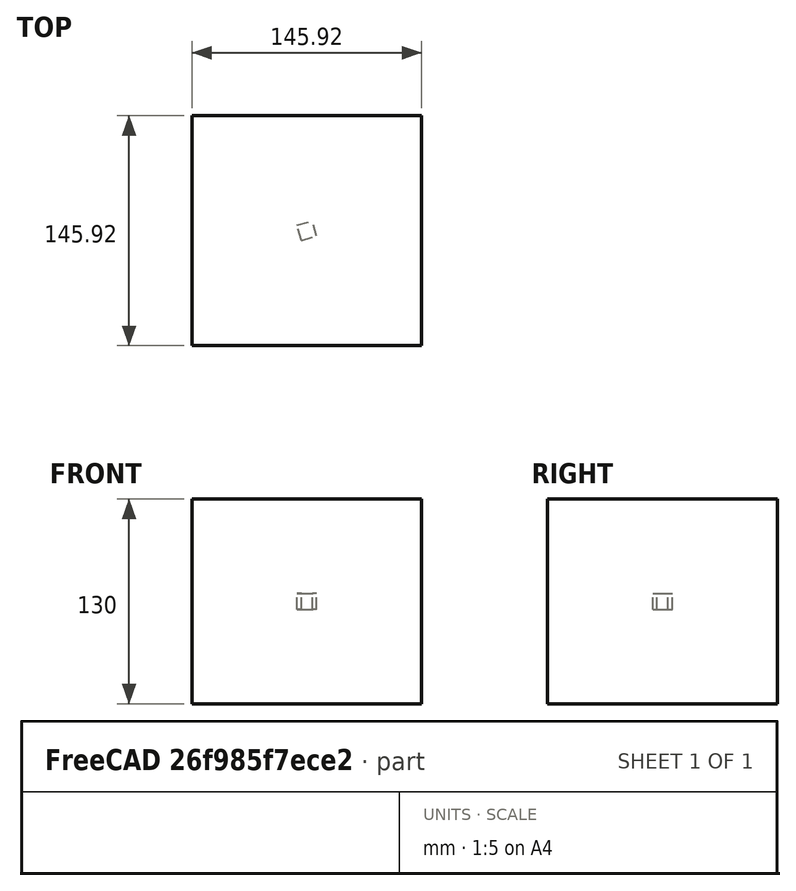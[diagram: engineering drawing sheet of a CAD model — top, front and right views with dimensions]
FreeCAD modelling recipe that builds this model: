
FCSTD DOCUMENT  (FreeCAD 0.20RUnknown)
Label: array-rotation-test-c
License: All rights reserved
objects: App::DocumentObjectGroupPython×1251, Part::FeaturePython×3, App::Part×2
note: 2 computed .brp shape members not serialized (recipe doc carries the construction recipe); baked Part::Feature solids carry a one-line shape summary decoded from their .brp

FEATURE [App::DocumentObjectGroupPython] HALFPI  # scripted group (container) (typed FeaturePython)
  name = HALFPI
  value = pi/2.
FEATURE [App::DocumentObjectGroupPython] PI  # scripted group (container) (typed FeaturePython)
  name = PI
  value = 1.*pi
FEATURE [App::DocumentObjectGroupPython] TWOPI  # scripted group (container) (typed FeaturePython)
  name = TWOPI
  value = 2.*pi
FEATURE [App::DocumentObjectGroupPython] Constants  # scripted group (container) (typed FeaturePython)
  Group = -> [HALFPI,PI,TWOPI]
FEATURE [App::DocumentObjectGroupPython] Variables  # scripted group (container) (typed FeaturePython)
FEATURE [App::DocumentObjectGroupPython] Quantities  # scripted group (container) (typed FeaturePython)
FEATURE [App::DocumentObjectGroupPython] Isotopes  # scripted group (container) (typed FeaturePython)
FEATURE [App::DocumentObjectGroupPython] Elements  # scripted group (container) (typed FeaturePython)
FEATURE [App::DocumentObjectGroupPython] Matrix  # scripted group (container) (typed FeaturePython)
FEATURE [App::DocumentObjectGroupPython] Surfaces  # scripted group (container) (typed FeaturePython)
FEATURE [App::DocumentObjectGroupPython] Opticals  # scripted group (container) (typed FeaturePython)
  Group = -> [Matrix,Surfaces]
FEATURE [App::DocumentObjectGroupPython] G4Isotopes  # scripted group (container) (typed FeaturePython)
FEATURE [App::DocumentObjectGroupPython] H_element  # scripted group (container) (typed FeaturePython)
  Z = 1
  atom_value = 1.008
  formula = H
  name = H_element
FEATURE [App::DocumentObjectGroupPython] He_element  # scripted group (container) (typed FeaturePython)
  Z = 2
  atom_value = 4.0026
  formula = He
  name = He_element
FEATURE [App::DocumentObjectGroupPython] Li_element  # scripted group (container) (typed FeaturePython)
  Z = 3
  atom_value = 6.94
  formula = Li
  name = Li_element
FEATURE [App::DocumentObjectGroupPython] Be_element  # scripted group (container) (typed FeaturePython)
  Z = 4
  atom_value = 9.01218
  formula = Be
  name = Be_element
FEATURE [App::DocumentObjectGroupPython] B_element  # scripted group (container) (typed FeaturePython)
  Z = 5
  atom_value = 10.81
  formula = B
  name = B_element
FEATURE [App::DocumentObjectGroupPython] C_element  # scripted group (container) (typed FeaturePython)
  Z = 6
  atom_value = 12.011
  formula = C
  name = C_element
FEATURE [App::DocumentObjectGroupPython] N_element  # scripted group (container) (typed FeaturePython)
  Z = 7
  atom_value = 14.007
  formula = N
  name = N_element
FEATURE [App::DocumentObjectGroupPython] O_element  # scripted group (container) (typed FeaturePython)
  Z = 8
  atom_value = 15.999
  formula = O
  name = O_element
FEATURE [App::DocumentObjectGroupPython] F_element  # scripted group (container) (typed FeaturePython)
  Z = 9
  atom_value = 18.9984
  formula = F
  name = F_element
FEATURE [App::DocumentObjectGroupPython] Ne_element  # scripted group (container) (typed FeaturePython)
  Z = 10
  atom_value = 20.1797
  formula = Ne
  name = Ne_element
FEATURE [App::DocumentObjectGroupPython] Na_element  # scripted group (container) (typed FeaturePython)
  Z = 11
  atom_value = 22.9898
  formula = Na
  name = Na_element
FEATURE [App::DocumentObjectGroupPython] Mg_element  # scripted group (container) (typed FeaturePython)
  Z = 12
  atom_value = 24.305
  formula = Mg
  name = Mg_element
FEATURE [App::DocumentObjectGroupPython] Al_element  # scripted group (container) (typed FeaturePython)
  Z = 13
  atom_value = 26.9815
  formula = Al
  name = Al_element
FEATURE [App::DocumentObjectGroupPython] Si_element  # scripted group (container) (typed FeaturePython)
  Z = 14
  atom_value = 28.085
  formula = Si
  name = Si_element
FEATURE [App::DocumentObjectGroupPython] P_element  # scripted group (container) (typed FeaturePython)
  Z = 15
  atom_value = 30.9738
  formula = P
  name = P_element
FEATURE [App::DocumentObjectGroupPython] S_element  # scripted group (container) (typed FeaturePython)
  Z = 16
  atom_value = 32.06
  formula = S
  name = S_element
FEATURE [App::DocumentObjectGroupPython] Cl_element  # scripted group (container) (typed FeaturePython)
  Z = 17
  atom_value = 35.45
  formula = Cl
  name = Cl_element
FEATURE [App::DocumentObjectGroupPython] Ar_element  # scripted group (container) (typed FeaturePython)
  Z = 18
  atom_value = 39.95
  formula = Ar
  name = Ar_element
FEATURE [App::DocumentObjectGroupPython] K_element  # scripted group (container) (typed FeaturePython)
  Z = 19
  atom_value = 39.0983
  formula = K
  name = K_element
FEATURE [App::DocumentObjectGroupPython] Ca_element  # scripted group (container) (typed FeaturePython)
  Z = 20
  atom_value = 40.078
  formula = Ca
  name = Ca_element
FEATURE [App::DocumentObjectGroupPython] Sc_element  # scripted group (container) (typed FeaturePython)
  Z = 21
  atom_value = 44.9559
  formula = Sc
  name = Sc_element
FEATURE [App::DocumentObjectGroupPython] Ti_element  # scripted group (container) (typed FeaturePython)
  Z = 22
  atom_value = 47.867
  formula = Ti
  name = Ti_element
FEATURE [App::DocumentObjectGroupPython] V_element  # scripted group (container) (typed FeaturePython)
  Z = 23
  atom_value = 50.9415
  formula = V
  name = V_element
FEATURE [App::DocumentObjectGroupPython] Cr_element  # scripted group (container) (typed FeaturePython)
  Z = 24
  atom_value = 51.9961
  formula = Cr
  name = Cr_element
FEATURE [App::DocumentObjectGroupPython] Mn_element  # scripted group (container) (typed FeaturePython)
  Z = 25
  atom_value = 54.938
  formula = Mn
  name = Mn_element
FEATURE [App::DocumentObjectGroupPython] Fe_element  # scripted group (container) (typed FeaturePython)
  Z = 26
  atom_value = 55.845
  formula = Fe
  name = Fe_element
FEATURE [App::DocumentObjectGroupPython] Co_element  # scripted group (container) (typed FeaturePython)
  Z = 27
  atom_value = 58.9332
  formula = Co
  name = Co_element
FEATURE [App::DocumentObjectGroupPython] Ni_element  # scripted group (container) (typed FeaturePython)
  Z = 28
  atom_value = 58.6934
  formula = Ni
  name = Ni_element
FEATURE [App::DocumentObjectGroupPython] Cu_element  # scripted group (container) (typed FeaturePython)
  Z = 29
  atom_value = 63.546
  formula = Cu
  name = Cu_element
FEATURE [App::DocumentObjectGroupPython] Zn_element  # scripted group (container) (typed FeaturePython)
  Z = 30
  atom_value = 65.38
  formula = Zn
  name = Zn_element
FEATURE [App::DocumentObjectGroupPython] Ga_element  # scripted group (container) (typed FeaturePython)
  Z = 31
  atom_value = 69.723
  formula = Ga
  name = Ga_element
FEATURE [App::DocumentObjectGroupPython] Ge_element  # scripted group (container) (typed FeaturePython)
  Z = 32
  atom_value = 72.63
  formula = Ge
  name = Ge_element
FEATURE [App::DocumentObjectGroupPython] As_element  # scripted group (container) (typed FeaturePython)
  Z = 33
  atom_value = 74.9216
  formula = As
  name = As_element
FEATURE [App::DocumentObjectGroupPython] Se_element  # scripted group (container) (typed FeaturePython)
  Z = 34
  atom_value = 78.971
  formula = Se
  name = Se_element
FEATURE [App::DocumentObjectGroupPython] Br_element  # scripted group (container) (typed FeaturePython)
  Z = 35
  atom_value = 79.904
  formula = Br
  name = Br_element
FEATURE [App::DocumentObjectGroupPython] Kr_element  # scripted group (container) (typed FeaturePython)
  Z = 36
  atom_value = 83.798
  formula = Kr
  name = Kr_element
FEATURE [App::DocumentObjectGroupPython] Rb_element  # scripted group (container) (typed FeaturePython)
  Z = 37
  atom_value = 85.4678
  formula = Rb
  name = Rb_element
FEATURE [App::DocumentObjectGroupPython] Sr_element  # scripted group (container) (typed FeaturePython)
  Z = 38
  atom_value = 87.62
  formula = Sr
  name = Sr_element
FEATURE [App::DocumentObjectGroupPython] Y_element  # scripted group (container) (typed FeaturePython)
  Z = 39
  atom_value = 88.9058
  formula = Y
  name = Y_element
FEATURE [App::DocumentObjectGroupPython] Zr_element  # scripted group (container) (typed FeaturePython)
  Z = 40
  atom_value = 91.224
  formula = Zr
  name = Zr_element
FEATURE [App::DocumentObjectGroupPython] Nb_element  # scripted group (container) (typed FeaturePython)
  Z = 41
  atom_value = 92.9064
  formula = Nb
  name = Nb_element
FEATURE [App::DocumentObjectGroupPython] Mo_element  # scripted group (container) (typed FeaturePython)
  Z = 42
  atom_value = 95.95
  formula = Mo
  name = Mo_element
FEATURE [App::DocumentObjectGroupPython] Tc_element  # scripted group (container) (typed FeaturePython)
  Z = 43
  atom_value = 97
  formula = Tc
  name = Tc_element
FEATURE [App::DocumentObjectGroupPython] Ru_element  # scripted group (container) (typed FeaturePython)
  Z = 44
  atom_value = 101.07
  formula = Ru
  name = Ru_element
FEATURE [App::DocumentObjectGroupPython] Rh_element  # scripted group (container) (typed FeaturePython)
  Z = 45
  atom_value = 102.905
  formula = Rh
  name = Rh_element
FEATURE [App::DocumentObjectGroupPython] Pd_element  # scripted group (container) (typed FeaturePython)
  Z = 46
  atom_value = 106.42
  formula = Pd
  name = Pd_element
FEATURE [App::DocumentObjectGroupPython] Ag_element  # scripted group (container) (typed FeaturePython)
  Z = 47
  atom_value = 107.868
  formula = Ag
  name = Ag_element
FEATURE [App::DocumentObjectGroupPython] Cd_element  # scripted group (container) (typed FeaturePython)
  Z = 48
  atom_value = 112.414
  formula = Cd
  name = Cd_element
FEATURE [App::DocumentObjectGroupPython] In_element  # scripted group (container) (typed FeaturePython)
  Z = 49
  atom_value = 114.818
  formula = In
  name = In_element
FEATURE [App::DocumentObjectGroupPython] Sn_element  # scripted group (container) (typed FeaturePython)
  Z = 50
  atom_value = 118.71
  formula = Sn
  name = Sn_element
FEATURE [App::DocumentObjectGroupPython] Sb_element  # scripted group (container) (typed FeaturePython)
  Z = 51
  atom_value = 121.76
  formula = Sb
  name = Sb_element
FEATURE [App::DocumentObjectGroupPython] Te_element  # scripted group (container) (typed FeaturePython)
  Z = 52
  atom_value = 127.6
  formula = Te
  name = Te_element
FEATURE [App::DocumentObjectGroupPython] I_element  # scripted group (container) (typed FeaturePython)
  Z = 53
  atom_value = 126.904
  formula = I
  name = I_element
FEATURE [App::DocumentObjectGroupPython] Xe_element  # scripted group (container) (typed FeaturePython)
  Z = 54
  atom_value = 131.293
  formula = Xe
  name = Xe_element
FEATURE [App::DocumentObjectGroupPython] Cs_element  # scripted group (container) (typed FeaturePython)
  Z = 55
  atom_value = 132.905
  formula = Cs
  name = Cs_element
FEATURE [App::DocumentObjectGroupPython] Ba_element  # scripted group (container) (typed FeaturePython)
  Z = 56
  atom_value = 137.327
  formula = Ba
  name = Ba_element
FEATURE [App::DocumentObjectGroupPython] La_element  # scripted group (container) (typed FeaturePython)
  Z = 57
  atom_value = 138.905
  formula = La
  name = La_element
FEATURE [App::DocumentObjectGroupPython] Ce_element  # scripted group (container) (typed FeaturePython)
  Z = 58
  atom_value = 140.116
  formula = Ce
  name = Ce_element
FEATURE [App::DocumentObjectGroupPython] Pr_element  # scripted group (container) (typed FeaturePython)
  Z = 59
  atom_value = 140.908
  formula = Pr
  name = Pr_element
FEATURE [App::DocumentObjectGroupPython] Nd_element  # scripted group (container) (typed FeaturePython)
  Z = 60
  atom_value = 144.242
  formula = Nd
  name = Nd_element
FEATURE [App::DocumentObjectGroupPython] Pm_element  # scripted group (container) (typed FeaturePython)
  Z = 61
  atom_value = 145
  formula = Pm
  name = Pm_element
FEATURE [App::DocumentObjectGroupPython] Sm_element  # scripted group (container) (typed FeaturePython)
  Z = 62
  atom_value = 150.36
  formula = Sm
  name = Sm_element
FEATURE [App::DocumentObjectGroupPython] Eu_element  # scripted group (container) (typed FeaturePython)
  Z = 63
  atom_value = 151.964
  formula = Eu
  name = Eu_element
FEATURE [App::DocumentObjectGroupPython] Gd_element  # scripted group (container) (typed FeaturePython)
  Z = 64
  atom_value = 157.25
  formula = Gd
  name = Gd_element
FEATURE [App::DocumentObjectGroupPython] Tb_element  # scripted group (container) (typed FeaturePython)
  Z = 65
  atom_value = 158.925
  formula = Tb
  name = Tb_element
FEATURE [App::DocumentObjectGroupPython] Dy_element  # scripted group (container) (typed FeaturePython)
  Z = 66
  atom_value = 162.5
  formula = Dy
  name = Dy_element
FEATURE [App::DocumentObjectGroupPython] Ho_element  # scripted group (container) (typed FeaturePython)
  Z = 67
  atom_value = 164.93
  formula = Ho
  name = Ho_element
FEATURE [App::DocumentObjectGroupPython] Er_element  # scripted group (container) (typed FeaturePython)
  Z = 68
  atom_value = 167.259
  formula = Er
  name = Er_element
FEATURE [App::DocumentObjectGroupPython] Tm_element  # scripted group (container) (typed FeaturePython)
  Z = 69
  atom_value = 168.934
  formula = Tm
  name = Tm_element
FEATURE [App::DocumentObjectGroupPython] Yb_element  # scripted group (container) (typed FeaturePython)
  Z = 70
  atom_value = 173.045
  formula = Yb
  name = Yb_element
FEATURE [App::DocumentObjectGroupPython] Lu_element  # scripted group (container) (typed FeaturePython)
  Z = 71
  atom_value = 174.967
  formula = Lu
  name = Lu_element
FEATURE [App::DocumentObjectGroupPython] Hf_element  # scripted group (container) (typed FeaturePython)
  Z = 72
  atom_value = 178.49
  formula = Hf
  name = Hf_element
FEATURE [App::DocumentObjectGroupPython] Ta_element  # scripted group (container) (typed FeaturePython)
  Z = 73
  atom_value = 180.948
  formula = Ta
  name = Ta_element
FEATURE [App::DocumentObjectGroupPython] W_element  # scripted group (container) (typed FeaturePython)
  Z = 74
  atom_value = 183.84
  formula = W
  name = W_element
FEATURE [App::DocumentObjectGroupPython] Re_element  # scripted group (container) (typed FeaturePython)
  Z = 75
  atom_value = 186.207
  formula = Re
  name = Re_element
FEATURE [App::DocumentObjectGroupPython] Os_element  # scripted group (container) (typed FeaturePython)
  Z = 76
  atom_value = 190.23
  formula = Os
  name = Os_element
FEATURE [App::DocumentObjectGroupPython] Ir_element  # scripted group (container) (typed FeaturePython)
  Z = 77
  atom_value = 192.217
  formula = Ir
  name = Ir_element
FEATURE [App::DocumentObjectGroupPython] Pt_element  # scripted group (container) (typed FeaturePython)
  Z = 78
  atom_value = 195.084
  formula = Pt
  name = Pt_element
FEATURE [App::DocumentObjectGroupPython] Au_element  # scripted group (container) (typed FeaturePython)
  Z = 79
  atom_value = 196.967
  formula = Au
  name = Au_element
FEATURE [App::DocumentObjectGroupPython] Hg_element  # scripted group (container) (typed FeaturePython)
  Z = 80
  atom_value = 200.592
  formula = Hg
  name = Hg_element
FEATURE [App::DocumentObjectGroupPython] Tl_element  # scripted group (container) (typed FeaturePython)
  Z = 81
  atom_value = 204.38
  formula = Tl
  name = Tl_element
FEATURE [App::DocumentObjectGroupPython] Pb_element  # scripted group (container) (typed FeaturePython)
  Z = 82
  atom_value = 207.2
  formula = Pb
  name = Pb_element
FEATURE [App::DocumentObjectGroupPython] Bi_element  # scripted group (container) (typed FeaturePython)
  Z = 83
  atom_value = 208.98
  formula = Bi
  name = Bi_element
FEATURE [App::DocumentObjectGroupPython] Po_element  # scripted group (container) (typed FeaturePython)
  Z = 84
  atom_value = 209
  formula = Po
  name = Po_element
FEATURE [App::DocumentObjectGroupPython] At_element  # scripted group (container) (typed FeaturePython)
  Z = 85
  atom_value = 210
  formula = At
  name = At_element
FEATURE [App::DocumentObjectGroupPython] Rn_element  # scripted group (container) (typed FeaturePython)
  Z = 86
  atom_value = 222
  formula = Rn
  name = Rn_element
FEATURE [App::DocumentObjectGroupPython] Fr_element  # scripted group (container) (typed FeaturePython)
  Z = 87
  atom_value = 223
  formula = Fr
  name = Fr_element
FEATURE [App::DocumentObjectGroupPython] Ra_element  # scripted group (container) (typed FeaturePython)
  Z = 88
  atom_value = 226
  formula = Ra
  name = Ra_element
FEATURE [App::DocumentObjectGroupPython] Ac_element  # scripted group (container) (typed FeaturePython)
  Z = 89
  atom_value = 227
  formula = Ac
  name = Ac_element
FEATURE [App::DocumentObjectGroupPython] Th_element  # scripted group (container) (typed FeaturePython)
  Z = 90
  atom_value = 232.038
  formula = Th
  name = Th_element
FEATURE [App::DocumentObjectGroupPython] Pa_element  # scripted group (container) (typed FeaturePython)
  Z = 91
  atom_value = 231.036
  formula = Pa
  name = Pa_element
FEATURE [App::DocumentObjectGroupPython] U_element  # scripted group (container) (typed FeaturePython)
  Z = 92
  atom_value = 238.029
  formula = U
  name = U_element
FEATURE [App::DocumentObjectGroupPython] Np_element  # scripted group (container) (typed FeaturePython)
  Z = 93
  atom_value = 237
  formula = Np
  name = Np_element
FEATURE [App::DocumentObjectGroupPython] Pu_element  # scripted group (container) (typed FeaturePython)
  Z = 94
  atom_value = 244
  formula = Pu
  name = Pu_element
FEATURE [App::DocumentObjectGroupPython] Am_element  # scripted group (container) (typed FeaturePython)
  Z = 95
  atom_value = 243
  formula = Am
  name = Am_element
FEATURE [App::DocumentObjectGroupPython] Cm_element  # scripted group (container) (typed FeaturePython)
  Z = 96
  atom_value = 247
  formula = Cm
  name = Cm_element
FEATURE [App::DocumentObjectGroupPython] Bk_element  # scripted group (container) (typed FeaturePython)
  Z = 97
  atom_value = 247
  formula = Bk
  name = Bk_element
FEATURE [App::DocumentObjectGroupPython] Cf_element  # scripted group (container) (typed FeaturePython)
  Z = 98
  atom_value = 251
  formula = Cf
  name = Cf_element
FEATURE [App::DocumentObjectGroupPython] G4Elements  # scripted group (container) (typed FeaturePython)
  Group = -> [H_element,He_element,Li_element,Be_element,B_element,C_element,N_element,O_element,F_element,Ne_element,Na_element,Mg_element,Al_element,Si_element,P_element,S_element,Cl_element,Ar_element,K_element,Ca_element,Sc_element,Ti_element,V_element,Cr_element,Mn_element,Fe_element,Co_element,Ni_element,Cu_element,Zn_element,Ga_element,Ge_element,As_element,Se_element,Br_element,Kr_element,Rb_element,+61 more]
FEATURE [App::DocumentObjectGroupPython] H_element001  label="H_element : 0.101"  # scripted group (container) (typed FeaturePython)
  n = 0.101327
FEATURE [App::DocumentObjectGroupPython] C_element001  label="C_element : 0.775"  # scripted group (container) (typed FeaturePython)
  n = 0.7755
FEATURE [App::DocumentObjectGroupPython] N_element001  label="N_element : 0.035"  # scripted group (container) (typed FeaturePython)
  n = 0.035057
FEATURE [App::DocumentObjectGroupPython] O_element001  label="O_element : 0.052"  # scripted group (container) (typed FeaturePython)
  n = 0.0523159
FEATURE [App::DocumentObjectGroupPython] F_element001  label="F_element : 0.017"  # scripted group (container) (typed FeaturePython)
  n = 0.017422
FEATURE [App::DocumentObjectGroupPython] Ca_element001  label="Ca_element : 0.018"  # scripted group (container) (typed FeaturePython)
  n = 0.018378
FEATURE [App::DocumentObjectGroupPython] G4_A_150_TISSUE  label="G4_A-150_TISSUE"  # scripted group (container) (typed FeaturePython)
  Dunit = g/cm3
  Dvalue = 1.127
  Group = -> [H_element001,C_element001,N_element001,O_element001,F_element001,Ca_element001]
  conduct = 2
  density = 1
  expand = 3
  formula = G4_A-150_TISSUE
  name = G4_A-150_TISSUE
  specific = 4
FEATURE [App::DocumentObjectGroupPython] C_element002  label="C_element : 3"  # scripted group (container) (typed FeaturePython)
  n = 3
  ref = C_element
FEATURE [App::DocumentObjectGroupPython] H_element002  label="H_element : 6"  # scripted group (container) (typed FeaturePython)
  n = 6
  ref = H_element
FEATURE [App::DocumentObjectGroupPython] O_element002  label="O_element : 1"  # scripted group (container) (typed FeaturePython)
  n = 1
  ref = O_element
FEATURE [App::DocumentObjectGroupPython] G4_ACETONE  # scripted group (container) (typed FeaturePython)
  Dunit = g/cm3
  Dvalue = 0.7899
  Group = -> [C_element002,H_element002,O_element002]
  conduct = 2
  density = 1
  expand = 3
  formula = G4_ACETONE
  name = G4_ACETONE
  specific = 4
FEATURE [App::DocumentObjectGroupPython] C_element003  label="C_element : 2"  # scripted group (container) (typed FeaturePython)
  n = 2
  ref = C_element
FEATURE [App::DocumentObjectGroupPython] H_element003  label="H_element : 2"  # scripted group (container) (typed FeaturePython)
  n = 2
  ref = H_element
FEATURE [App::DocumentObjectGroupPython] G4_ACETYLENE  # scripted group (container) (typed FeaturePython)
  Dunit = g/cm3
  Dvalue = 0.0010967
  Group = -> [C_element003,H_element003]
  conduct = 2
  density = 1
  expand = 3
  formula = G4_ACETYLENE
  name = G4_ACETYLENE
  specific = 4
FEATURE [App::DocumentObjectGroupPython] C_element004  label="C_element : 5"  # scripted group (container) (typed FeaturePython)
  n = 5
  ref = C_element
FEATURE [App::DocumentObjectGroupPython] H_element004  label="H_element : 5"  # scripted group (container) (typed FeaturePython)
  n = 5
  ref = H_element
FEATURE [App::DocumentObjectGroupPython] N_element002  label="N_element : 5"  # scripted group (container) (typed FeaturePython)
  n = 5
  ref = N_element
FEATURE [App::DocumentObjectGroupPython] G4_ADENINE  # scripted group (container) (typed FeaturePython)
  Dunit = g/cm3
  Dvalue = 1.6
  Group = -> [C_element004,H_element004,N_element002]
  conduct = 2
  density = 1
  expand = 3
  formula = G4_ADENINE
  name = G4_ADENINE
  specific = 4
FEATURE [App::DocumentObjectGroupPython] H_element005  label="H_element : 0.114"  # scripted group (container) (typed FeaturePython)
  n = 0.114
FEATURE [App::DocumentObjectGroupPython] C_element005  label="C_element : 0.598"  # scripted group (container) (typed FeaturePython)
  n = 0.598
FEATURE [App::DocumentObjectGroupPython] N_element003  label="N_element : 0.007"  # scripted group (container) (typed FeaturePython)
  n = 0.007
FEATURE [App::DocumentObjectGroupPython] O_element003  label="O_element : 0.278"  # scripted group (container) (typed FeaturePython)
  n = 0.278
FEATURE [App::DocumentObjectGroupPython] Na_element001  label="Na_element : 0.001"  # scripted group (container) (typed FeaturePython)
  n = 0.001
FEATURE [App::DocumentObjectGroupPython] S_element001  label="S_element : 0.001"  # scripted group (container) (typed FeaturePython)
  n = 0.001
FEATURE [App::DocumentObjectGroupPython] Cl_element001  label="Cl_element : 0.001"  # scripted group (container) (typed FeaturePython)
  n = 0.001
FEATURE [App::DocumentObjectGroupPython] G4_ADIPOSE_TISSUE_ICRP  # scripted group (container) (typed FeaturePython)
  Dunit = g/cm3
  Dvalue = 0.95
  Group = -> [H_element005,C_element005,N_element003,O_element003,Na_element001,S_element001,Cl_element001]
  conduct = 2
  density = 1
  expand = 3
  formula = G4_ADIPOSE_TISSUE_ICRP
  name = G4_ADIPOSE_TISSUE_ICRP
  specific = 4
FEATURE [App::DocumentObjectGroupPython] C_element006  label="C_element : 0.000"  # scripted group (container) (typed FeaturePython)
  n = 0.000124
FEATURE [App::DocumentObjectGroupPython] N_element004  label="N_element : 0.755"  # scripted group (container) (typed FeaturePython)
  n = 0.755268
FEATURE [App::DocumentObjectGroupPython] O_element004  label="O_element : 0.232"  # scripted group (container) (typed FeaturePython)
  n = 0.231781
FEATURE [App::DocumentObjectGroupPython] Ar_element001  label="Ar_element : 0.013"  # scripted group (container) (typed FeaturePython)
  n = 0.012827
FEATURE [App::DocumentObjectGroupPython] G4_AIR  # scripted group (container) (typed FeaturePython)
  Dunit = g/cm3
  Dvalue = 0.00120479
  Group = -> [C_element006,N_element004,O_element004,Ar_element001]
  conduct = 2
  density = 1
  expand = 3
  formula = G4_AIR
  name = G4_AIR
  specific = 4
FEATURE [App::DocumentObjectGroupPython] C_element007  label="C_element : 006"  # scripted group (container) (typed FeaturePython)
  n = 3
  ref = C_element
FEATURE [App::DocumentObjectGroupPython] H_element006  label="H_element : 7"  # scripted group (container) (typed FeaturePython)
  n = 7
  ref = H_element
FEATURE [App::DocumentObjectGroupPython] N_element005  label="N_element : 1"  # scripted group (container) (typed FeaturePython)
  n = 1
  ref = N_element
FEATURE [App::DocumentObjectGroupPython] O_element005  label="O_element : 2"  # scripted group (container) (typed FeaturePython)
  n = 2
  ref = O_element
FEATURE [App::DocumentObjectGroupPython] G4_ALANINE  # scripted group (container) (typed FeaturePython)
  Dunit = g/cm3
  Dvalue = 1.42
  Group = -> [C_element007,H_element006,N_element005,O_element005]
  conduct = 2
  density = 1
  expand = 3
  formula = G4_ALANINE
  name = G4_ALANINE
  specific = 4
FEATURE [App::DocumentObjectGroupPython] Al_element001  label="Al_element : 2"  # scripted group (container) (typed FeaturePython)
  n = 2
  ref = Al_element
FEATURE [App::DocumentObjectGroupPython] O_element006  label="O_element : 3"  # scripted group (container) (typed FeaturePython)
  n = 3
  ref = O_element
FEATURE [App::DocumentObjectGroupPython] G4_ALUMINUM_OXIDE  # scripted group (container) (typed FeaturePython)
  Dunit = g/cm3
  Dvalue = 3.97
  Group = -> [Al_element001,O_element006]
  conduct = 2
  density = 1
  expand = 3
  formula = G4_ALUMINUM_OXIDE
  name = G4_ALUMINUM_OXIDE
  specific = 4
FEATURE [App::DocumentObjectGroupPython] H_element007  label="H_element : 0.106"  # scripted group (container) (typed FeaturePython)
  n = 0.10593
FEATURE [App::DocumentObjectGroupPython] C_element008  label="C_element : 0.789"  # scripted group (container) (typed FeaturePython)
  n = 0.788974
FEATURE [App::DocumentObjectGroupPython] O_element007  label="O_element : 0.105"  # scripted group (container) (typed FeaturePython)
  n = 0.105096
FEATURE [App::DocumentObjectGroupPython] G4_AMBER  # scripted group (container) (typed FeaturePython)
  Dunit = g/cm3
  Dvalue = 1.1
  Group = -> [H_element007,C_element008,O_element007]
  conduct = 2
  density = 1
  expand = 3
  formula = G4_AMBER
  name = G4_AMBER
  specific = 4
FEATURE [App::DocumentObjectGroupPython] N_element006  label="N_element : 006"  # scripted group (container) (typed FeaturePython)
  n = 1
  ref = N_element
FEATURE [App::DocumentObjectGroupPython] H_element008  label="H_element : 3"  # scripted group (container) (typed FeaturePython)
  n = 3
  ref = H_element
FEATURE [App::DocumentObjectGroupPython] G4_AMMONIA  # scripted group (container) (typed FeaturePython)
  Dunit = g/cm3
  Dvalue = 0.000826019
  Group = -> [N_element006,H_element008]
  conduct = 2
  density = 1
  expand = 3
  formula = G4_AMMONIA
  name = G4_AMMONIA
  specific = 4
FEATURE [App::DocumentObjectGroupPython] C_element009  label="C_element : 6"  # scripted group (container) (typed FeaturePython)
  n = 6
  ref = C_element
FEATURE [App::DocumentObjectGroupPython] H_element009  label="H_element : 008"  # scripted group (container) (typed FeaturePython)
  n = 7
  ref = H_element
FEATURE [App::DocumentObjectGroupPython] N_element007  label="N_element : 007"  # scripted group (container) (typed FeaturePython)
  n = 1
  ref = N_element
FEATURE [App::DocumentObjectGroupPython] G4_ANILINE  # scripted group (container) (typed FeaturePython)
  Dunit = g/cm3
  Dvalue = 1.0235
  Group = -> [C_element009,H_element009,N_element007]
  conduct = 2
  density = 1
  expand = 3
  formula = G4_ANILINE
  name = G4_ANILINE
  specific = 4
FEATURE [App::DocumentObjectGroupPython] C_element010  label="C_element : 14"  # scripted group (container) (typed FeaturePython)
  n = 14
  ref = C_element
FEATURE [App::DocumentObjectGroupPython] H_element010  label="H_element : 10"  # scripted group (container) (typed FeaturePython)
  n = 10
  ref = H_element
FEATURE [App::DocumentObjectGroupPython] G4_ANTHRACENE  # scripted group (container) (typed FeaturePython)
  Dunit = g/cm3
  Dvalue = 1.283
  Group = -> [C_element010,H_element010]
  conduct = 2
  density = 1
  expand = 3
  formula = G4_ANTHRACENE
  name = G4_ANTHRACENE
  specific = 4
FEATURE [App::DocumentObjectGroupPython] H_element011  label="H_element : 0.065"  # scripted group (container) (typed FeaturePython)
  n = 0.0654709
FEATURE [App::DocumentObjectGroupPython] C_element011  label="C_element : 0.537"  # scripted group (container) (typed FeaturePython)
  n = 0.536944
FEATURE [App::DocumentObjectGroupPython] N_element008  label="N_element : 0.021"  # scripted group (container) (typed FeaturePython)
  n = 0.0215
FEATURE [App::DocumentObjectGroupPython] O_element008  label="O_element : 0.032"  # scripted group (container) (typed FeaturePython)
  n = 0.032085
FEATURE [App::DocumentObjectGroupPython] F_element002  label="F_element : 0.167"  # scripted group (container) (typed FeaturePython)
  n = 0.167411
FEATURE [App::DocumentObjectGroupPython] Ca_element002  label="Ca_element : 0.177"  # scripted group (container) (typed FeaturePython)
  n = 0.176589
FEATURE [App::DocumentObjectGroupPython] G4_B_100_BONE  label="G4_B-100_BONE"  # scripted group (container) (typed FeaturePython)
  Dunit = g/cm3
  Dvalue = 1.45
  Group = -> [H_element011,C_element011,N_element008,O_element008,F_element002,Ca_element002]
  conduct = 2
  density = 1
  expand = 3
  formula = G4_B-100_BONE
  name = G4_B-100_BONE
  specific = 4
FEATURE [App::DocumentObjectGroupPython] H_element012  label="H_element : 0.057"  # scripted group (container) (typed FeaturePython)
  n = 0.057441
FEATURE [App::DocumentObjectGroupPython] C_element012  label="C_element : 0.790"  # scripted group (container) (typed FeaturePython)
  n = 0.774591
FEATURE [App::DocumentObjectGroupPython] O_element009  label="O_element : 0.168"  # scripted group (container) (typed FeaturePython)
  n = 0.167968
FEATURE [App::DocumentObjectGroupPython] G4_BAKELITE  # scripted group (container) (typed FeaturePython)
  Dunit = g/cm3
  Dvalue = 1.25
  Group = -> [H_element012,C_element012,O_element009]
  conduct = 2
  density = 1
  expand = 3
  formula = G4_BAKELITE
  name = G4_BAKELITE
  specific = 4
FEATURE [App::DocumentObjectGroupPython] Ba_element001  label="Ba_element : 1"  # scripted group (container) (typed FeaturePython)
  n = 1
  ref = Ba_element
FEATURE [App::DocumentObjectGroupPython] F_element003  label="F_element : 2"  # scripted group (container) (typed FeaturePython)
  n = 2
  ref = F_element
FEATURE [App::DocumentObjectGroupPython] G4_BARIUM_FLUORIDE  # scripted group (container) (typed FeaturePython)
  Dunit = g/cm3
  Dvalue = 4.89
  Group = -> [Ba_element001,F_element003]
  conduct = 2
  density = 1
  expand = 3
  formula = G4_BARIUM_FLUORIDE
  name = G4_BARIUM_FLUORIDE
  specific = 4
FEATURE [App::DocumentObjectGroupPython] Ba_element002  label="Ba_element : 002"  # scripted group (container) (typed FeaturePython)
  n = 1
  ref = Ba_element
FEATURE [App::DocumentObjectGroupPython] S_element002  label="S_element : 1"  # scripted group (container) (typed FeaturePython)
  n = 1
  ref = S_element
FEATURE [App::DocumentObjectGroupPython] O_element010  label="O_element : 4"  # scripted group (container) (typed FeaturePython)
  n = 4
  ref = O_element
FEATURE [App::DocumentObjectGroupPython] G4_BARIUM_SULFATE  # scripted group (container) (typed FeaturePython)
  Dunit = g/cm3
  Dvalue = 4.5
  Group = -> [Ba_element002,S_element002,O_element010]
  conduct = 2
  density = 1
  expand = 3
  formula = G4_BARIUM_SULFATE
  name = G4_BARIUM_SULFATE
  specific = 4
FEATURE [App::DocumentObjectGroupPython] C_element013  label="C_element : 007"  # scripted group (container) (typed FeaturePython)
  n = 6
  ref = C_element
FEATURE [App::DocumentObjectGroupPython] H_element013  label="H_element : 009"  # scripted group (container) (typed FeaturePython)
  n = 6
  ref = H_element
FEATURE [App::DocumentObjectGroupPython] G4_BENZENE  # scripted group (container) (typed FeaturePython)
  Dunit = g/cm3
  Dvalue = 0.87865
  Group = -> [C_element013,H_element013]
  conduct = 2
  density = 1
  expand = 3
  formula = G4_BENZENE
  name = G4_BENZENE
  specific = 4
FEATURE [App::DocumentObjectGroupPython] Be_element001  label="Be_element : 1"  # scripted group (container) (typed FeaturePython)
  n = 1
  ref = Be_element
FEATURE [App::DocumentObjectGroupPython] O_element011  label="O_element : 005"  # scripted group (container) (typed FeaturePython)
  n = 1
  ref = O_element
FEATURE [App::DocumentObjectGroupPython] G4_BERYLLIUM_OXIDE  # scripted group (container) (typed FeaturePython)
  Dunit = g/cm3
  Dvalue = 3.01
  Group = -> [Be_element001,O_element011]
  conduct = 2
  density = 1
  expand = 3
  formula = G4_BERYLLIUM_OXIDE
  name = G4_BERYLLIUM_OXIDE
  specific = 4
FEATURE [App::DocumentObjectGroupPython] Bi_element001  label="Bi_element : 4"  # scripted group (container) (typed FeaturePython)
  n = 4
  ref = Bi_element
FEATURE [App::DocumentObjectGroupPython] Ge_element001  label="Ge_element : 3"  # scripted group (container) (typed FeaturePython)
  n = 3
  ref = Ge_element
FEATURE [App::DocumentObjectGroupPython] O_element012  label="O_element : 12"  # scripted group (container) (typed FeaturePython)
  n = 12
  ref = O_element
FEATURE [App::DocumentObjectGroupPython] G4_BGO  # scripted group (container) (typed FeaturePython)
  Dunit = g/cm3
  Dvalue = 7.13
  Group = -> [Bi_element001,Ge_element001,O_element012]
  conduct = 2
  density = 1
  expand = 3
  formula = G4_BGO
  name = G4_BGO
  specific = 4
FEATURE [App::DocumentObjectGroupPython] H_element014  label="H_element : 0.102"  # scripted group (container) (typed FeaturePython)
  n = 0.102
FEATURE [App::DocumentObjectGroupPython] C_element014  label="C_element : 0.110"  # scripted group (container) (typed FeaturePython)
  n = 0.11
FEATURE [App::DocumentObjectGroupPython] N_element009  label="N_element : 0.033"  # scripted group (container) (typed FeaturePython)
  n = 0.033
FEATURE [App::DocumentObjectGroupPython] O_element013  label="O_element : 0.745"  # scripted group (container) (typed FeaturePython)
  n = 0.745
FEATURE [App::DocumentObjectGroupPython] Na_element002  label="Na_element : 0.002"  # scripted group (container) (typed FeaturePython)
  n = 0.001
FEATURE [App::DocumentObjectGroupPython] P_element001  label="P_element : 0.001"  # scripted group (container) (typed FeaturePython)
  n = 0.001
FEATURE [App::DocumentObjectGroupPython] S_element003  label="S_element : 0.002"  # scripted group (container) (typed FeaturePython)
  n = 0.002
FEATURE [App::DocumentObjectGroupPython] Cl_element002  label="Cl_element : 0.003"  # scripted group (container) (typed FeaturePython)
  n = 0.003
FEATURE [App::DocumentObjectGroupPython] K_element001  label="K_element : 0.002"  # scripted group (container) (typed FeaturePython)
  n = 0.002
FEATURE [App::DocumentObjectGroupPython] Fe_element001  label="Fe_element : 0.001"  # scripted group (container) (typed FeaturePython)
  n = 0.001
FEATURE [App::DocumentObjectGroupPython] G4_BLOOD_ICRP  # scripted group (container) (typed FeaturePython)
  Dunit = g/cm3
  Dvalue = 1.06
  Group = -> [H_element014,C_element014,N_element009,O_element013,Na_element002,P_element001,S_element003,Cl_element002,K_element001,Fe_element001]
  conduct = 2
  density = 1
  expand = 3
  formula = G4_BLOOD_ICRP
  name = G4_BLOOD_ICRP
  specific = 4
FEATURE [App::DocumentObjectGroupPython] H_element015  label="H_element : 0.064"  # scripted group (container) (typed FeaturePython)
  n = 0.064
FEATURE [App::DocumentObjectGroupPython] C_element015  label="C_element : 0.278"  # scripted group (container) (typed FeaturePython)
  n = 0.278
FEATURE [App::DocumentObjectGroupPython] N_element010  label="N_element : 0.027"  # scripted group (container) (typed FeaturePython)
  n = 0.027
FEATURE [App::DocumentObjectGroupPython] O_element014  label="O_element : 0.410"  # scripted group (container) (typed FeaturePython)
  n = 0.41
FEATURE [App::DocumentObjectGroupPython] Mg_element001  label="Mg_element : 0.002"  # scripted group (container) (typed FeaturePython)
  n = 0.002
FEATURE [App::DocumentObjectGroupPython] P_element002  label="P_element : 0.070"  # scripted group (container) (typed FeaturePython)
  n = 0.07
FEATURE [App::DocumentObjectGroupPython] S_element004  label="S_element : 0.003"  # scripted group (container) (typed FeaturePython)
  n = 0.002
FEATURE [App::DocumentObjectGroupPython] Ca_element003  label="Ca_element : 0.147"  # scripted group (container) (typed FeaturePython)
  n = 0.147
FEATURE [App::DocumentObjectGroupPython] G4_BONE_COMPACT_ICRU  # scripted group (container) (typed FeaturePython)
  Dunit = g/cm3
  Dvalue = 1.85
  Group = -> [H_element015,C_element015,N_element010,O_element014,Mg_element001,P_element002,S_element004,Ca_element003]
  conduct = 2
  density = 1
  expand = 3
  formula = G4_BONE_COMPACT_ICRU
  name = G4_BONE_COMPACT_ICRU
  specific = 4
FEATURE [App::DocumentObjectGroupPython] H_element016  label="H_element : 0.034"  # scripted group (container) (typed FeaturePython)
  n = 0.034
FEATURE [App::DocumentObjectGroupPython] C_element016  label="C_element : 0.155"  # scripted group (container) (typed FeaturePython)
  n = 0.155
FEATURE [App::DocumentObjectGroupPython] N_element011  label="N_element : 0.042"  # scripted group (container) (typed FeaturePython)
  n = 0.042
FEATURE [App::DocumentObjectGroupPython] O_element015  label="O_element : 0.435"  # scripted group (container) (typed FeaturePython)
  n = 0.435
FEATURE [App::DocumentObjectGroupPython] Na_element003  label="Na_element : 0.003"  # scripted group (container) (typed FeaturePython)
  n = 0.001
FEATURE [App::DocumentObjectGroupPython] Mg_element002  label="Mg_element : 0.003"  # scripted group (container) (typed FeaturePython)
  n = 0.002
FEATURE [App::DocumentObjectGroupPython] P_element003  label="P_element : 0.103"  # scripted group (container) (typed FeaturePython)
  n = 0.103
FEATURE [App::DocumentObjectGroupPython] S_element005  label="S_element : 0.004"  # scripted group (container) (typed FeaturePython)
  n = 0.003
FEATURE [App::DocumentObjectGroupPython] Ca_element004  label="Ca_element : 0.225"  # scripted group (container) (typed FeaturePython)
  n = 0.225
FEATURE [App::DocumentObjectGroupPython] G4_BONE_CORTICAL_ICRP  # scripted group (container) (typed FeaturePython)
  Dunit = g/cm3
  Dvalue = 1.92
  Group = -> [H_element016,C_element016,N_element011,O_element015,Na_element003,Mg_element002,P_element003,S_element005,Ca_element004]
  conduct = 2
  density = 1
  expand = 3
  formula = G4_BONE_CORTICAL_ICRP
  name = G4_BONE_CORTICAL_ICRP
  specific = 4
FEATURE [App::DocumentObjectGroupPython] B_element001  label="B_element : 4"  # scripted group (container) (typed FeaturePython)
  n = 4
  ref = B_element
FEATURE [App::DocumentObjectGroupPython] C_element017  label="C_element : 1"  # scripted group (container) (typed FeaturePython)
  n = 1
  ref = C_element
FEATURE [App::DocumentObjectGroupPython] G4_BORON_CARBIDE  # scripted group (container) (typed FeaturePython)
  Dunit = g/cm3
  Dvalue = 2.52
  Group = -> [B_element001,C_element017]
  conduct = 2
  density = 1
  expand = 3
  formula = G4_BORON_CARBIDE
  name = G4_BORON_CARBIDE
  specific = 4
FEATURE [App::DocumentObjectGroupPython] B_element002  label="B_element : 2"  # scripted group (container) (typed FeaturePython)
  n = 2
  ref = B_element
FEATURE [App::DocumentObjectGroupPython] O_element016  label="O_element : 006"  # scripted group (container) (typed FeaturePython)
  n = 3
  ref = O_element
FEATURE [App::DocumentObjectGroupPython] G4_BORON_OXIDE  # scripted group (container) (typed FeaturePython)
  Dunit = g/cm3
  Dvalue = 1.812
  Group = -> [B_element002,O_element016]
  conduct = 2
  density = 1
  expand = 3
  formula = G4_BORON_OXIDE
  name = G4_BORON_OXIDE
  specific = 4
FEATURE [App::DocumentObjectGroupPython] H_element017  label="H_element : 0.107"  # scripted group (container) (typed FeaturePython)
  n = 0.107
FEATURE [App::DocumentObjectGroupPython] C_element018  label="C_element : 0.145"  # scripted group (container) (typed FeaturePython)
  n = 0.145
FEATURE [App::DocumentObjectGroupPython] N_element012  label="N_element : 0.022"  # scripted group (container) (typed FeaturePython)
  n = 0.022
FEATURE [App::DocumentObjectGroupPython] O_element017  label="O_element : 0.712"  # scripted group (container) (typed FeaturePython)
  n = 0.712
FEATURE [App::DocumentObjectGroupPython] Na_element004  label="Na_element : 0.004"  # scripted group (container) (typed FeaturePython)
  n = 0.002
FEATURE [App::DocumentObjectGroupPython] P_element004  label="P_element : 0.004"  # scripted group (container) (typed FeaturePython)
  n = 0.004
FEATURE [App::DocumentObjectGroupPython] S_element006  label="S_element : 0.005"  # scripted group (container) (typed FeaturePython)
  n = 0.002
FEATURE [App::DocumentObjectGroupPython] Cl_element003  label="Cl_element : 0.004"  # scripted group (container) (typed FeaturePython)
  n = 0.003
FEATURE [App::DocumentObjectGroupPython] K_element002  label="K_element : 0.003"  # scripted group (container) (typed FeaturePython)
  n = 0.003
FEATURE [App::DocumentObjectGroupPython] G4_BRAIN_ICRP  # scripted group (container) (typed FeaturePython)
  Dunit = g/cm3
  Dvalue = 1.04
  Group = -> [H_element017,C_element018,N_element012,O_element017,Na_element004,P_element004,S_element006,Cl_element003,K_element002]
  conduct = 2
  density = 1
  expand = 3
  formula = G4_BRAIN_ICRP
  name = G4_BRAIN_ICRP
  specific = 4
FEATURE [App::DocumentObjectGroupPython] C_element019  label="C_element : 4"  # scripted group (container) (typed FeaturePython)
  n = 4
  ref = C_element
FEATURE [App::DocumentObjectGroupPython] H_element018  label="H_element : 010"  # scripted group (container) (typed FeaturePython)
  n = 10
  ref = H_element
FEATURE [App::DocumentObjectGroupPython] G4_BUTANE  # scripted group (container) (typed FeaturePython)
  Dunit = g/cm3
  Dvalue = 0.00249343
  Group = -> [C_element019,H_element018]
  conduct = 2
  density = 1
  expand = 3
  formula = G4_BUTANE
  name = G4_BUTANE
  specific = 4
FEATURE [App::DocumentObjectGroupPython] C_element020  label="C_element : 008"  # scripted group (container) (typed FeaturePython)
  n = 4
  ref = C_element
FEATURE [App::DocumentObjectGroupPython] H_element019  label="H_element : 011"  # scripted group (container) (typed FeaturePython)
  n = 10
  ref = H_element
FEATURE [App::DocumentObjectGroupPython] O_element018  label="O_element : 007"  # scripted group (container) (typed FeaturePython)
  n = 1
  ref = O_element
FEATURE [App::DocumentObjectGroupPython] G4_N_BUTYL_ALCOHOL  label="G4_N-BUTYL_ALCOHOL"  # scripted group (container) (typed FeaturePython)
  Dunit = g/cm3
  Dvalue = 0.8098
  Group = -> [C_element020,H_element019,O_element018]
  conduct = 2
  density = 1
  expand = 3
  formula = G4_N-BUTYL_ALCOHOL
  name = G4_N-BUTYL_ALCOHOL
  specific = 4
FEATURE [App::DocumentObjectGroupPython] H_element020  label="H_element : 0.025"  # scripted group (container) (typed FeaturePython)
  n = 0.02468
FEATURE [App::DocumentObjectGroupPython] C_element021  label="C_element : 0.502"  # scripted group (container) (typed FeaturePython)
  n = 0.501611
FEATURE [App::DocumentObjectGroupPython] O_element019  label="O_element : 0.005"  # scripted group (container) (typed FeaturePython)
  n = 0.004527
FEATURE [App::DocumentObjectGroupPython] F_element004  label="F_element : 0.465"  # scripted group (container) (typed FeaturePython)
  n = 0.465209
FEATURE [App::DocumentObjectGroupPython] Si_element001  label="Si_element : 0.004"  # scripted group (container) (typed FeaturePython)
  n = 0.003973
FEATURE [App::DocumentObjectGroupPython] G4_C_552  label="G4_C-552"  # scripted group (container) (typed FeaturePython)
  Dunit = g/cm3
  Dvalue = 1.76
  Group = -> [H_element020,C_element021,O_element019,F_element004,Si_element001]
  conduct = 2
  density = 1
  expand = 3
  formula = G4_C-552
  name = G4_C-552
  specific = 4
FEATURE [App::DocumentObjectGroupPython] Cd_element001  label="Cd_element : 1"  # scripted group (container) (typed FeaturePython)
  n = 1
  ref = Cd_element
FEATURE [App::DocumentObjectGroupPython] Te_element001  label="Te_element : 1"  # scripted group (container) (typed FeaturePython)
  n = 1
  ref = Te_element
FEATURE [App::DocumentObjectGroupPython] G4_CADMIUM_TELLURIDE  # scripted group (container) (typed FeaturePython)
  Dunit = g/cm3
  Dvalue = 6.2
  Group = -> [Cd_element001,Te_element001]
  conduct = 2
  density = 1
  expand = 3
  formula = G4_CADMIUM_TELLURIDE
  name = G4_CADMIUM_TELLURIDE
  specific = 4
FEATURE [App::DocumentObjectGroupPython] Cd_element002  label="Cd_element : 002"  # scripted group (container) (typed FeaturePython)
  n = 1
  ref = Cd_element
FEATURE [App::DocumentObjectGroupPython] W_element001  label="W_element : 1"  # scripted group (container) (typed FeaturePython)
  n = 1
  ref = W_element
FEATURE [App::DocumentObjectGroupPython] O_element020  label="O_element : 008"  # scripted group (container) (typed FeaturePython)
  n = 4
  ref = O_element
FEATURE [App::DocumentObjectGroupPython] G4_CADMIUM_TUNGSTATE  # scripted group (container) (typed FeaturePython)
  Dunit = g/cm3
  Dvalue = 7.9
  Group = -> [Cd_element002,W_element001,O_element020]
  conduct = 2
  density = 1
  expand = 3
  formula = G4_CADMIUM_TUNGSTATE
  name = G4_CADMIUM_TUNGSTATE
  specific = 4
FEATURE [App::DocumentObjectGroupPython] Ca_element005  label="Ca_element : 1"  # scripted group (container) (typed FeaturePython)
  n = 1
  ref = Ca_element
FEATURE [App::DocumentObjectGroupPython] C_element022  label="C_element : 009"  # scripted group (container) (typed FeaturePython)
  n = 1
  ref = C_element
FEATURE [App::DocumentObjectGroupPython] O_element021  label="O_element : 009"  # scripted group (container) (typed FeaturePython)
  n = 3
  ref = O_element
FEATURE [App::DocumentObjectGroupPython] G4_CALCIUM_CARBONATE  # scripted group (container) (typed FeaturePython)
  Dunit = g/cm3
  Dvalue = 2.8
  Group = -> [Ca_element005,C_element022,O_element021]
  conduct = 2
  density = 1
  expand = 3
  formula = G4_CALCIUM_CARBONATE
  name = G4_CALCIUM_CARBONATE
  specific = 4
FEATURE [App::DocumentObjectGroupPython] Ca_element006  label="Ca_element : 002"  # scripted group (container) (typed FeaturePython)
  n = 1
  ref = Ca_element
FEATURE [App::DocumentObjectGroupPython] F_element005  label="F_element : 003"  # scripted group (container) (typed FeaturePython)
  n = 2
  ref = F_element
FEATURE [App::DocumentObjectGroupPython] G4_CALCIUM_FLUORIDE  # scripted group (container) (typed FeaturePython)
  Dunit = g/cm3
  Dvalue = 3.18
  Group = -> [Ca_element006,F_element005]
  conduct = 2
  density = 1
  expand = 3
  formula = G4_CALCIUM_FLUORIDE
  name = G4_CALCIUM_FLUORIDE
  specific = 4
FEATURE [App::DocumentObjectGroupPython] Ca_element007  label="Ca_element : 003"  # scripted group (container) (typed FeaturePython)
  n = 1
  ref = Ca_element
FEATURE [App::DocumentObjectGroupPython] O_element022  label="O_element : 010"  # scripted group (container) (typed FeaturePython)
  n = 1
  ref = O_element
FEATURE [App::DocumentObjectGroupPython] G4_CALCIUM_OXIDE  # scripted group (container) (typed FeaturePython)
  Dunit = g/cm3
  Dvalue = 3.3
  Group = -> [Ca_element007,O_element022]
  conduct = 2
  density = 1
  expand = 3
  formula = G4_CALCIUM_OXIDE
  name = G4_CALCIUM_OXIDE
  specific = 4
FEATURE [App::DocumentObjectGroupPython] Ca_element008  label="Ca_element : 004"  # scripted group (container) (typed FeaturePython)
  n = 1
  ref = Ca_element
FEATURE [App::DocumentObjectGroupPython] S_element007  label="S_element : 002"  # scripted group (container) (typed FeaturePython)
  n = 1
  ref = S_element
FEATURE [App::DocumentObjectGroupPython] O_element023  label="O_element : 011"  # scripted group (container) (typed FeaturePython)
  n = 4
  ref = O_element
FEATURE [App::DocumentObjectGroupPython] G4_CALCIUM_SULFATE  # scripted group (container) (typed FeaturePython)
  Dunit = g/cm3
  Dvalue = 2.96
  Group = -> [Ca_element008,S_element007,O_element023]
  conduct = 2
  density = 1
  expand = 3
  formula = G4_CALCIUM_SULFATE
  name = G4_CALCIUM_SULFATE
  specific = 4
FEATURE [App::DocumentObjectGroupPython] Ca_element009  label="Ca_element : 005"  # scripted group (container) (typed FeaturePython)
  n = 1
  ref = Ca_element
FEATURE [App::DocumentObjectGroupPython] W_element002  label="W_element : 002"  # scripted group (container) (typed FeaturePython)
  n = 1
  ref = W_element
FEATURE [App::DocumentObjectGroupPython] O_element024  label="O_element : 012"  # scripted group (container) (typed FeaturePython)
  n = 4
  ref = O_element
FEATURE [App::DocumentObjectGroupPython] G4_CALCIUM_TUNGSTATE  # scripted group (container) (typed FeaturePython)
  Dunit = g/cm3
  Dvalue = 6.062
  Group = -> [Ca_element009,W_element002,O_element024]
  conduct = 2
  density = 1
  expand = 3
  formula = G4_CALCIUM_TUNGSTATE
  name = G4_CALCIUM_TUNGSTATE
  specific = 4
FEATURE [App::DocumentObjectGroupPython] C_element023  label="C_element : 010"  # scripted group (container) (typed FeaturePython)
  n = 1
  ref = C_element
FEATURE [App::DocumentObjectGroupPython] O_element025  label="O_element : 013"  # scripted group (container) (typed FeaturePython)
  n = 2
  ref = O_element
FEATURE [App::DocumentObjectGroupPython] G4_CARBON_DIOXIDE  # scripted group (container) (typed FeaturePython)
  Dunit = g/cm3
  Dvalue = 0.00184212
  Group = -> [C_element023,O_element025]
  conduct = 2
  density = 1
  expand = 3
  formula = G4_CARBON_DIOXIDE
  name = G4_CARBON_DIOXIDE
  specific = 4
FEATURE [App::DocumentObjectGroupPython] C_element024  label="C_element : 011"  # scripted group (container) (typed FeaturePython)
  n = 1
  ref = C_element
FEATURE [App::DocumentObjectGroupPython] Cl_element004  label="Cl_element : 4"  # scripted group (container) (typed FeaturePython)
  n = 4
  ref = Cl_element
FEATURE [App::DocumentObjectGroupPython] G4_CARBON_TETRACHLORIDE  # scripted group (container) (typed FeaturePython)
  Dunit = g/cm3
  Dvalue = 1.594
  Group = -> [C_element024,Cl_element004]
  conduct = 2
  density = 1
  expand = 3
  formula = G4_CARBON_TETRACHLORIDE
  name = G4_CARBON_TETRACHLORIDE
  specific = 4
FEATURE [App::DocumentObjectGroupPython] C_element025  label="C_element : 012"  # scripted group (container) (typed FeaturePython)
  n = 6
  ref = C_element
FEATURE [App::DocumentObjectGroupPython] H_element021  label="H_element : 012"  # scripted group (container) (typed FeaturePython)
  n = 10
  ref = H_element
FEATURE [App::DocumentObjectGroupPython] O_element026  label="O_element : 5"  # scripted group (container) (typed FeaturePython)
  n = 5
  ref = O_element
FEATURE [App::DocumentObjectGroupPython] G4_CELLULOSE_CELLOPHANE  # scripted group (container) (typed FeaturePython)
  Dunit = g/cm3
  Dvalue = 1.42
  Group = -> [C_element025,H_element021,O_element026]
  conduct = 2
  density = 1
  expand = 3
  formula = G4_CELLULOSE_CELLOPHANE
  name = G4_CELLULOSE_CELLOPHANE
  specific = 4
FEATURE [App::DocumentObjectGroupPython] H_element022  label="H_element : 0.067"  # scripted group (container) (typed FeaturePython)
  n = 0.067125
FEATURE [App::DocumentObjectGroupPython] C_element026  label="C_element : 0.545"  # scripted group (container) (typed FeaturePython)
  n = 0.545403
FEATURE [App::DocumentObjectGroupPython] O_element027  label="O_element : 0.387"  # scripted group (container) (typed FeaturePython)
  n = 0.387472
FEATURE [App::DocumentObjectGroupPython] G4_CELLULOSE_BUTYRATE  # scripted group (container) (typed FeaturePython)
  Dunit = g/cm3
  Dvalue = 1.2
  Group = -> [H_element022,C_element026,O_element027]
  conduct = 2
  density = 1
  expand = 3
  formula = G4_CELLULOSE_BUTYRATE
  name = G4_CELLULOSE_BUTYRATE
  specific = 4
FEATURE [App::DocumentObjectGroupPython] H_element023  label="H_element : 0.029"  # scripted group (container) (typed FeaturePython)
  n = 0.029216
FEATURE [App::DocumentObjectGroupPython] C_element027  label="C_element : 0.271"  # scripted group (container) (typed FeaturePython)
  n = 0.271296
FEATURE [App::DocumentObjectGroupPython] N_element013  label="N_element : 0.121"  # scripted group (container) (typed FeaturePython)
  n = 0.121276
FEATURE [App::DocumentObjectGroupPython] O_element028  label="O_element : 0.578"  # scripted group (container) (typed FeaturePython)
  n = 0.578212
FEATURE [App::DocumentObjectGroupPython] G4_CELLULOSE_NITRATE  # scripted group (container) (typed FeaturePython)
  Dunit = g/cm3
  Dvalue = 1.49
  Group = -> [H_element023,C_element027,N_element013,O_element028]
  conduct = 2
  density = 1
  expand = 3
  formula = G4_CELLULOSE_NITRATE
  name = G4_CELLULOSE_NITRATE
  specific = 4
FEATURE [App::DocumentObjectGroupPython] H_element024  label="H_element : 0.108"  # scripted group (container) (typed FeaturePython)
  n = 0.107596
FEATURE [App::DocumentObjectGroupPython] N_element014  label="N_element : 0.001"  # scripted group (container) (typed FeaturePython)
  n = 0.0008
FEATURE [App::DocumentObjectGroupPython] O_element029  label="O_element : 0.875"  # scripted group (container) (typed FeaturePython)
  n = 0.874976
FEATURE [App::DocumentObjectGroupPython] S_element008  label="S_element : 0.015"  # scripted group (container) (typed FeaturePython)
  n = 0.014627
FEATURE [App::DocumentObjectGroupPython] Ce_element001  label="Ce_element : 0.002"  # scripted group (container) (typed FeaturePython)
  n = 0.002001
FEATURE [App::DocumentObjectGroupPython] G4_CERIC_SULFATE  # scripted group (container) (typed FeaturePython)
  Dunit = g/cm3
  Dvalue = 1.03
  Group = -> [H_element024,N_element014,O_element029,S_element008,Ce_element001]
  conduct = 2
  density = 1
  expand = 3
  formula = G4_CERIC_SULFATE
  name = G4_CERIC_SULFATE
  specific = 4
FEATURE [App::DocumentObjectGroupPython] Cs_element001  label="Cs_element : 1"  # scripted group (container) (typed FeaturePython)
  n = 1
  ref = Cs_element
FEATURE [App::DocumentObjectGroupPython] F_element006  label="F_element : 1"  # scripted group (container) (typed FeaturePython)
  n = 1
  ref = F_element
FEATURE [App::DocumentObjectGroupPython] G4_CESIUM_FLUORIDE  # scripted group (container) (typed FeaturePython)
  Dunit = g/cm3
  Dvalue = 4.115
  Group = -> [Cs_element001,F_element006]
  conduct = 2
  density = 1
  expand = 3
  formula = G4_CESIUM_FLUORIDE
  name = G4_CESIUM_FLUORIDE
  specific = 4
FEATURE [App::DocumentObjectGroupPython] Cs_element002  label="Cs_element : 002"  # scripted group (container) (typed FeaturePython)
  n = 1
  ref = Cs_element
FEATURE [App::DocumentObjectGroupPython] I_element001  label="I_element : 1"  # scripted group (container) (typed FeaturePython)
  n = 1
  ref = I_element
FEATURE [App::DocumentObjectGroupPython] G4_CESIUM_IODIDE  # scripted group (container) (typed FeaturePython)
  Dunit = g/cm3
  Dvalue = 4.51
  Group = -> [Cs_element002,I_element001]
  conduct = 2
  density = 1
  expand = 3
  formula = G4_CESIUM_IODIDE
  name = G4_CESIUM_IODIDE
  specific = 4
FEATURE [App::DocumentObjectGroupPython] C_element028  label="C_element : 013"  # scripted group (container) (typed FeaturePython)
  n = 6
  ref = C_element
FEATURE [App::DocumentObjectGroupPython] H_element025  label="H_element : 013"  # scripted group (container) (typed FeaturePython)
  n = 5
  ref = H_element
FEATURE [App::DocumentObjectGroupPython] Cl_element005  label="Cl_element : 1"  # scripted group (container) (typed FeaturePython)
  n = 1
  ref = Cl_element
FEATURE [App::DocumentObjectGroupPython] G4_CHLOROBENZENE  # scripted group (container) (typed FeaturePython)
  Dunit = g/cm3
  Dvalue = 1.1058
  Group = -> [C_element028,H_element025,Cl_element005]
  conduct = 2
  density = 1
  expand = 3
  formula = G4_CHLOROBENZENE
  name = G4_CHLOROBENZENE
  specific = 4
FEATURE [App::DocumentObjectGroupPython] C_element029  label="C_element : 014"  # scripted group (container) (typed FeaturePython)
  n = 1
  ref = C_element
FEATURE [App::DocumentObjectGroupPython] H_element026  label="H_element : 1"  # scripted group (container) (typed FeaturePython)
  n = 1
  ref = H_element
FEATURE [App::DocumentObjectGroupPython] Cl_element006  label="Cl_element : 3"  # scripted group (container) (typed FeaturePython)
  n = 3
  ref = Cl_element
FEATURE [App::DocumentObjectGroupPython] G4_CHLOROFORM  # scripted group (container) (typed FeaturePython)
  Dunit = g/cm3
  Dvalue = 1.4832
  Group = -> [C_element029,H_element026,Cl_element006]
  conduct = 2
  density = 1
  expand = 3
  formula = G4_CHLOROFORM
  name = G4_CHLOROFORM
  specific = 4
FEATURE [App::DocumentObjectGroupPython] H_element027  label="H_element : 0.010"  # scripted group (container) (typed FeaturePython)
  n = 0.01
FEATURE [App::DocumentObjectGroupPython] C_element030  label="C_element : 0.001"  # scripted group (container) (typed FeaturePython)
  n = 0.001
FEATURE [App::DocumentObjectGroupPython] O_element030  label="O_element : 0.529"  # scripted group (container) (typed FeaturePython)
  n = 0.529107
FEATURE [App::DocumentObjectGroupPython] Na_element005  label="Na_element : 0.016"  # scripted group (container) (typed FeaturePython)
  n = 0.016
FEATURE [App::DocumentObjectGroupPython] Mg_element003  label="Mg_element : 0.004"  # scripted group (container) (typed FeaturePython)
  n = 0.002
FEATURE [App::DocumentObjectGroupPython] Al_element002  label="Al_element : 0.034"  # scripted group (container) (typed FeaturePython)
  n = 0.033872
FEATURE [App::DocumentObjectGroupPython] Si_element002  label="Si_element : 0.337"  # scripted group (container) (typed FeaturePython)
  n = 0.337021
FEATURE [App::DocumentObjectGroupPython] K_element003  label="K_element : 0.013"  # scripted group (container) (typed FeaturePython)
  n = 0.013
FEATURE [App::DocumentObjectGroupPython] Ca_element010  label="Ca_element : 0.044"  # scripted group (container) (typed FeaturePython)
  n = 0.044
FEATURE [App::DocumentObjectGroupPython] Fe_element002  label="Fe_element : 0.014"  # scripted group (container) (typed FeaturePython)
  n = 0.014
FEATURE [App::DocumentObjectGroupPython] G4_CONCRETE  # scripted group (container) (typed FeaturePython)
  Dunit = g/cm3
  Dvalue = 2.3
  Group = -> [H_element027,C_element030,O_element030,Na_element005,Mg_element003,Al_element002,Si_element002,K_element003,Ca_element010,Fe_element002]
  conduct = 2
  density = 1
  expand = 3
  formula = G4_CONCRETE
  name = G4_CONCRETE
  specific = 4
FEATURE [App::DocumentObjectGroupPython] C_element031  label="C_element : 015"  # scripted group (container) (typed FeaturePython)
  n = 6
  ref = C_element
FEATURE [App::DocumentObjectGroupPython] H_element028  label="H_element : 12"  # scripted group (container) (typed FeaturePython)
  n = 12
  ref = H_element
FEATURE [App::DocumentObjectGroupPython] G4_CYCLOHEXANE  # scripted group (container) (typed FeaturePython)
  Dunit = g/cm3
  Dvalue = 0.779
  Group = -> [C_element031,H_element028]
  conduct = 2
  density = 1
  expand = 3
  formula = G4_CYCLOHEXANE
  name = G4_CYCLOHEXANE
  specific = 4
FEATURE [App::DocumentObjectGroupPython] C_element032  label="C_element : 016"  # scripted group (container) (typed FeaturePython)
  n = 6
  ref = C_element
FEATURE [App::DocumentObjectGroupPython] H_element029  label="H_element : 4"  # scripted group (container) (typed FeaturePython)
  n = 4
  ref = H_element
FEATURE [App::DocumentObjectGroupPython] Cl_element007  label="Cl_element : 2"  # scripted group (container) (typed FeaturePython)
  n = 2
  ref = Cl_element
FEATURE [App::DocumentObjectGroupPython] G4_1_2_DICHLOROBENZENE  label="G4_1.2-DICHLOROBENZENE"  # scripted group (container) (typed FeaturePython)
  Dunit = g/cm3
  Dvalue = 1.3048
  Group = -> [C_element032,H_element029,Cl_element007]
  conduct = 2
  density = 1
  expand = 3
  formula = G4_1.2-DICHLOROBENZENE
  name = G4_1.2-DICHLOROBENZENE
  specific = 4
FEATURE [App::DocumentObjectGroupPython] C_element033  label="C_element : 017"  # scripted group (container) (typed FeaturePython)
  n = 4
  ref = C_element
FEATURE [App::DocumentObjectGroupPython] H_element030  label="H_element : 8"  # scripted group (container) (typed FeaturePython)
  n = 8
  ref = H_element
FEATURE [App::DocumentObjectGroupPython] O_element031  label="O_element : 014"  # scripted group (container) (typed FeaturePython)
  n = 1
  ref = O_element
FEATURE [App::DocumentObjectGroupPython] Cl_element008  label="Cl_element : 005"  # scripted group (container) (typed FeaturePython)
  n = 2
  ref = Cl_element
FEATURE [App::DocumentObjectGroupPython] G4_DICHLORODIETHYL_ETHER  # scripted group (container) (typed FeaturePython)
  Dunit = g/cm3
  Dvalue = 1.2199
  Group = -> [C_element033,H_element030,O_element031,Cl_element008]
  conduct = 2
  density = 1
  expand = 3
  formula = G4_DICHLORODIETHYL_ETHER
  name = G4_DICHLORODIETHYL_ETHER
  specific = 4
FEATURE [App::DocumentObjectGroupPython] C_element034  label="C_element : 018"  # scripted group (container) (typed FeaturePython)
  n = 2
  ref = C_element
FEATURE [App::DocumentObjectGroupPython] H_element031  label="H_element : 014"  # scripted group (container) (typed FeaturePython)
  n = 4
  ref = H_element
FEATURE [App::DocumentObjectGroupPython] Cl_element009  label="Cl_element : 006"  # scripted group (container) (typed FeaturePython)
  n = 2
  ref = Cl_element
FEATURE [App::DocumentObjectGroupPython] G4_1_2_DICHLOROETHANE  label="G4_1.2-DICHLOROETHANE"  # scripted group (container) (typed FeaturePython)
  Dunit = g/cm3
  Dvalue = 1.2351
  Group = -> [C_element034,H_element031,Cl_element009]
  conduct = 2
  density = 1
  expand = 3
  formula = G4_1.2-DICHLOROETHANE
  name = G4_1.2-DICHLOROETHANE
  specific = 4
FEATURE [App::DocumentObjectGroupPython] C_element035  label="C_element : 019"  # scripted group (container) (typed FeaturePython)
  n = 4
  ref = C_element
FEATURE [App::DocumentObjectGroupPython] H_element032  label="H_element : 015"  # scripted group (container) (typed FeaturePython)
  n = 10
  ref = H_element
FEATURE [App::DocumentObjectGroupPython] O_element032  label="O_element : 015"  # scripted group (container) (typed FeaturePython)
  n = 1
  ref = O_element
FEATURE [App::DocumentObjectGroupPython] G4_DIETHYL_ETHER  # scripted group (container) (typed FeaturePython)
  Dunit = g/cm3
  Dvalue = 0.71378
  Group = -> [C_element035,H_element032,O_element032]
  conduct = 2
  density = 1
  expand = 3
  formula = G4_DIETHYL_ETHER
  name = G4_DIETHYL_ETHER
  specific = 4
FEATURE [App::DocumentObjectGroupPython] C_element036  label="C_element : 020"  # scripted group (container) (typed FeaturePython)
  n = 3
  ref = C_element
FEATURE [App::DocumentObjectGroupPython] H_element033  label="H_element : 016"  # scripted group (container) (typed FeaturePython)
  n = 7
  ref = H_element
FEATURE [App::DocumentObjectGroupPython] N_element015  label="N_element : 008"  # scripted group (container) (typed FeaturePython)
  n = 1
  ref = N_element
FEATURE [App::DocumentObjectGroupPython] O_element033  label="O_element : 016"  # scripted group (container) (typed FeaturePython)
  n = 1
  ref = O_element
FEATURE [App::DocumentObjectGroupPython] G4_N_N_DIMETHYL_FORMAMIDE  label="G4_N.N-DIMETHYL_FORMAMIDE"  # scripted group (container) (typed FeaturePython)
  Dunit = g/cm3
  Dvalue = 0.9487
  Group = -> [C_element036,H_element033,N_element015,O_element033]
  conduct = 2
  density = 1
  expand = 3
  formula = G4_N.N-DIMETHYL_FORMAMIDE
  name = G4_N.N-DIMETHYL_FORMAMIDE
  specific = 4
FEATURE [App::DocumentObjectGroupPython] C_element037  label="C_element : 021"  # scripted group (container) (typed FeaturePython)
  n = 2
  ref = C_element
FEATURE [App::DocumentObjectGroupPython] H_element034  label="H_element : 017"  # scripted group (container) (typed FeaturePython)
  n = 6
  ref = H_element
FEATURE [App::DocumentObjectGroupPython] O_element034  label="O_element : 017"  # scripted group (container) (typed FeaturePython)
  n = 1
  ref = O_element
FEATURE [App::DocumentObjectGroupPython] S_element009  label="S_element : 003"  # scripted group (container) (typed FeaturePython)
  n = 1
  ref = S_element
FEATURE [App::DocumentObjectGroupPython] G4_DIMETHYL_SULFOXIDE  # scripted group (container) (typed FeaturePython)
  Dunit = g/cm3
  Dvalue = 1.1014
  Group = -> [C_element037,H_element034,O_element034,S_element009]
  conduct = 2
  density = 1
  expand = 3
  formula = G4_DIMETHYL_SULFOXIDE
  name = G4_DIMETHYL_SULFOXIDE
  specific = 4
FEATURE [App::DocumentObjectGroupPython] C_element038  label="C_element : 022"  # scripted group (container) (typed FeaturePython)
  n = 2
  ref = C_element
FEATURE [App::DocumentObjectGroupPython] H_element035  label="H_element : 018"  # scripted group (container) (typed FeaturePython)
  n = 6
  ref = H_element
FEATURE [App::DocumentObjectGroupPython] G4_ETHANE  # scripted group (container) (typed FeaturePython)
  Dunit = g/cm3
  Dvalue = 0.00125324
  Group = -> [C_element038,H_element035]
  conduct = 2
  density = 1
  expand = 3
  formula = G4_ETHANE
  name = G4_ETHANE
  specific = 4
FEATURE [App::DocumentObjectGroupPython] C_element039  label="C_element : 023"  # scripted group (container) (typed FeaturePython)
  n = 2
  ref = C_element
FEATURE [App::DocumentObjectGroupPython] H_element036  label="H_element : 019"  # scripted group (container) (typed FeaturePython)
  n = 6
  ref = H_element
FEATURE [App::DocumentObjectGroupPython] O_element035  label="O_element : 018"  # scripted group (container) (typed FeaturePython)
  n = 1
  ref = O_element
FEATURE [App::DocumentObjectGroupPython] G4_ETHYL_ALCOHOL  # scripted group (container) (typed FeaturePython)
  Dunit = g/cm3
  Dvalue = 0.7893
  Group = -> [C_element039,H_element036,O_element035]
  conduct = 2
  density = 1
  expand = 3
  formula = G4_ETHYL_ALCOHOL
  name = G4_ETHYL_ALCOHOL
  specific = 4
FEATURE [App::DocumentObjectGroupPython] H_element037  label="H_element : 0.090"  # scripted group (container) (typed FeaturePython)
  n = 0.090027
FEATURE [App::DocumentObjectGroupPython] C_element040  label="C_element : 0.585"  # scripted group (container) (typed FeaturePython)
  n = 0.585182
FEATURE [App::DocumentObjectGroupPython] O_element036  label="O_element : 0.325"  # scripted group (container) (typed FeaturePython)
  n = 0.324791
FEATURE [App::DocumentObjectGroupPython] G4_ETHYL_CELLULOSE  # scripted group (container) (typed FeaturePython)
  Dunit = g/cm3
  Dvalue = 1.13
  Group = -> [H_element037,C_element040,O_element036]
  conduct = 2
  density = 1
  expand = 3
  formula = G4_ETHYL_CELLULOSE
  name = G4_ETHYL_CELLULOSE
  specific = 4
FEATURE [App::DocumentObjectGroupPython] C_element041  label="C_element : 024"  # scripted group (container) (typed FeaturePython)
  n = 2
  ref = C_element
FEATURE [App::DocumentObjectGroupPython] H_element038  label="H_element : 020"  # scripted group (container) (typed FeaturePython)
  n = 4
  ref = H_element
FEATURE [App::DocumentObjectGroupPython] G4_ETHYLENE  # scripted group (container) (typed FeaturePython)
  Dunit = g/cm3
  Dvalue = 0.00117497
  Group = -> [C_element041,H_element038]
  conduct = 2
  density = 1
  expand = 3
  formula = G4_ETHYLENE
  name = G4_ETHYLENE
  specific = 4
FEATURE [App::DocumentObjectGroupPython] H_element039  label="H_element : 0.096"  # scripted group (container) (typed FeaturePython)
  n = 0.096
FEATURE [App::DocumentObjectGroupPython] C_element042  label="C_element : 0.195"  # scripted group (container) (typed FeaturePython)
  n = 0.195
FEATURE [App::DocumentObjectGroupPython] N_element016  label="N_element : 0.057"  # scripted group (container) (typed FeaturePython)
  n = 0.057
FEATURE [App::DocumentObjectGroupPython] O_element037  label="O_element : 0.646"  # scripted group (container) (typed FeaturePython)
  n = 0.646
FEATURE [App::DocumentObjectGroupPython] Na_element006  label="Na_element : 0.017"  # scripted group (container) (typed FeaturePython)
  n = 0.001
FEATURE [App::DocumentObjectGroupPython] P_element005  label="P_element : 0.104"  # scripted group (container) (typed FeaturePython)
  n = 0.001
FEATURE [App::DocumentObjectGroupPython] S_element010  label="S_element : 0.016"  # scripted group (container) (typed FeaturePython)
  n = 0.003
FEATURE [App::DocumentObjectGroupPython] Cl_element010  label="Cl_element : 0.005"  # scripted group (container) (typed FeaturePython)
  n = 0.001
FEATURE [App::DocumentObjectGroupPython] G4_EYE_LENS_ICRP  # scripted group (container) (typed FeaturePython)
  Dunit = g/cm3
  Dvalue = 1.07
  Group = -> [H_element039,C_element042,N_element016,O_element037,Na_element006,P_element005,S_element010,Cl_element010]
  conduct = 2
  density = 1
  expand = 3
  formula = G4_EYE_LENS_ICRP
  name = G4_EYE_LENS_ICRP
  specific = 4
FEATURE [App::DocumentObjectGroupPython] Fe_element003  label="Fe_element : 2"  # scripted group (container) (typed FeaturePython)
  n = 2
  ref = Fe_element
FEATURE [App::DocumentObjectGroupPython] O_element038  label="O_element : 019"  # scripted group (container) (typed FeaturePython)
  n = 3
  ref = O_element
FEATURE [App::DocumentObjectGroupPython] G4_FERRIC_OXIDE  # scripted group (container) (typed FeaturePython)
  Dunit = g/cm3
  Dvalue = 5.2
  Group = -> [Fe_element003,O_element038]
  conduct = 2
  density = 1
  expand = 3
  formula = G4_FERRIC_OXIDE
  name = G4_FERRIC_OXIDE
  specific = 4
FEATURE [App::DocumentObjectGroupPython] Fe_element004  label="Fe_element : 1"  # scripted group (container) (typed FeaturePython)
  n = 1
  ref = Fe_element
FEATURE [App::DocumentObjectGroupPython] B_element003  label="B_element : 1"  # scripted group (container) (typed FeaturePython)
  n = 1
  ref = B_element
FEATURE [App::DocumentObjectGroupPython] G4_FERROBORIDE  # scripted group (container) (typed FeaturePython)
  Dunit = g/cm3
  Dvalue = 7.15
  Group = -> [Fe_element004,B_element003]
  conduct = 2
  density = 1
  expand = 3
  formula = G4_FERROBORIDE
  name = G4_FERROBORIDE
  specific = 4
FEATURE [App::DocumentObjectGroupPython] Fe_element005  label="Fe_element : 003"  # scripted group (container) (typed FeaturePython)
  n = 1
  ref = Fe_element
FEATURE [App::DocumentObjectGroupPython] O_element039  label="O_element : 020"  # scripted group (container) (typed FeaturePython)
  n = 1
  ref = O_element
FEATURE [App::DocumentObjectGroupPython] G4_FERROUS_OXIDE  # scripted group (container) (typed FeaturePython)
  Dunit = g/cm3
  Dvalue = 5.7
  Group = -> [Fe_element005,O_element039]
  conduct = 2
  density = 1
  expand = 3
  formula = G4_FERROUS_OXIDE
  name = G4_FERROUS_OXIDE
  specific = 4
FEATURE [App::DocumentObjectGroupPython] H_element040  label="H_element : 0.115"  # scripted group (container) (typed FeaturePython)
  n = 0.108259
FEATURE [App::DocumentObjectGroupPython] N_element017  label="N_element : 0.000"  # scripted group (container) (typed FeaturePython)
  n = 2.7e-05
FEATURE [App::DocumentObjectGroupPython] O_element040  label="O_element : 0.879"  # scripted group (container) (typed FeaturePython)
  n = 0.878636
FEATURE [App::DocumentObjectGroupPython] Na_element007  label="Na_element : 0.000"  # scripted group (container) (typed FeaturePython)
  n = 2.2e-05
FEATURE [App::DocumentObjectGroupPython] S_element011  label="S_element : 0.013"  # scripted group (container) (typed FeaturePython)
  n = 0.012968
FEATURE [App::DocumentObjectGroupPython] Cl_element011  label="Cl_element : 0.000"  # scripted group (container) (typed FeaturePython)
  n = 3.4e-05
FEATURE [App::DocumentObjectGroupPython] Fe_element006  label="Fe_element : 0.000"  # scripted group (container) (typed FeaturePython)
  n = 5.4e-05
FEATURE [App::DocumentObjectGroupPython] G4_FERROUS_SULFATE  # scripted group (container) (typed FeaturePython)
  Dunit = g/cm3
  Dvalue = 1.024
  Group = -> [H_element040,N_element017,O_element040,Na_element007,S_element011,Cl_element011,Fe_element006]
  conduct = 2
  density = 1
  expand = 3
  formula = G4_FERROUS_SULFATE
  name = G4_FERROUS_SULFATE
  specific = 4
FEATURE [App::DocumentObjectGroupPython] C_element043  label="C_element : 0.099"  # scripted group (container) (typed FeaturePython)
  n = 0.099335
FEATURE [App::DocumentObjectGroupPython] F_element007  label="F_element : 0.314"  # scripted group (container) (typed FeaturePython)
  n = 0.314247
FEATURE [App::DocumentObjectGroupPython] Cl_element012  label="Cl_element : 0.586"  # scripted group (container) (typed FeaturePython)
  n = 0.586418
FEATURE [App::DocumentObjectGroupPython] G4_FREON_12  label="G4_FREON-12"  # scripted group (container) (typed FeaturePython)
  Dunit = g/cm3
  Dvalue = 1.12
  Group = -> [C_element043,F_element007,Cl_element012]
  conduct = 2
  density = 1
  expand = 3
  formula = G4_FREON-12
  name = G4_FREON-12
  specific = 4
FEATURE [App::DocumentObjectGroupPython] C_element044  label="C_element : 0.057"  # scripted group (container) (typed FeaturePython)
  n = 0.057245
FEATURE [App::DocumentObjectGroupPython] F_element008  label="F_element : 0.181"  # scripted group (container) (typed FeaturePython)
  n = 0.181096
FEATURE [App::DocumentObjectGroupPython] Br_element001  label="Br_element : 0.762"  # scripted group (container) (typed FeaturePython)
  n = 0.761659
FEATURE [App::DocumentObjectGroupPython] G4_FREON_12B2  label="G4_FREON-12B2"  # scripted group (container) (typed FeaturePython)
  Dunit = g/cm3
  Dvalue = 1.8
  Group = -> [C_element044,F_element008,Br_element001]
  conduct = 2
  density = 1
  expand = 3
  formula = G4_FREON-12B2
  name = G4_FREON-12B2
  specific = 4
FEATURE [App::DocumentObjectGroupPython] C_element045  label="C_element : 0.115"  # scripted group (container) (typed FeaturePython)
  n = 0.114983
FEATURE [App::DocumentObjectGroupPython] F_element009  label="F_element : 0.546"  # scripted group (container) (typed FeaturePython)
  n = 0.545621
FEATURE [App::DocumentObjectGroupPython] Cl_element013  label="Cl_element : 0.339"  # scripted group (container) (typed FeaturePython)
  n = 0.339396
FEATURE [App::DocumentObjectGroupPython] G4_FREON_13  label="G4_FREON-13"  # scripted group (container) (typed FeaturePython)
  Dunit = g/cm3
  Dvalue = 0.95
  Group = -> [C_element045,F_element009,Cl_element013]
  conduct = 2
  density = 1
  expand = 3
  formula = G4_FREON-13
  name = G4_FREON-13
  specific = 4
FEATURE [App::DocumentObjectGroupPython] C_element046  label="C_element : 025"  # scripted group (container) (typed FeaturePython)
  n = 1
  ref = C_element
FEATURE [App::DocumentObjectGroupPython] F_element010  label="F_element : 3"  # scripted group (container) (typed FeaturePython)
  n = 3
  ref = F_element
FEATURE [App::DocumentObjectGroupPython] Br_element002  label="Br_element : 1"  # scripted group (container) (typed FeaturePython)
  n = 1
  ref = Br_element
FEATURE [App::DocumentObjectGroupPython] G4_FREON_13B1  label="G4_FREON-13B1"  # scripted group (container) (typed FeaturePython)
  Dunit = g/cm3
  Dvalue = 1.5
  Group = -> [C_element046,F_element010,Br_element002]
  conduct = 2
  density = 1
  expand = 3
  formula = G4_FREON-13B1
  name = G4_FREON-13B1
  specific = 4
FEATURE [App::DocumentObjectGroupPython] C_element047  label="C_element : 0.061"  # scripted group (container) (typed FeaturePython)
  n = 0.061309
FEATURE [App::DocumentObjectGroupPython] F_element011  label="F_element : 0.291"  # scripted group (container) (typed FeaturePython)
  n = 0.290924
FEATURE [App::DocumentObjectGroupPython] I_element002  label="I_element : 0.648"  # scripted group (container) (typed FeaturePython)
  n = 0.647767
FEATURE [App::DocumentObjectGroupPython] G4_FREON_13I1  label="G4_FREON-13I1"  # scripted group (container) (typed FeaturePython)
  Dunit = g/cm3
  Dvalue = 1.8
  Group = -> [C_element047,F_element011,I_element002]
  conduct = 2
  density = 1
  expand = 3
  formula = G4_FREON-13I1
  name = G4_FREON-13I1
  specific = 4
FEATURE [App::DocumentObjectGroupPython] Gd_element001  label="Gd_element : 2"  # scripted group (container) (typed FeaturePython)
  n = 2
  ref = Gd_element
FEATURE [App::DocumentObjectGroupPython] O_element041  label="O_element : 021"  # scripted group (container) (typed FeaturePython)
  n = 2
  ref = O_element
FEATURE [App::DocumentObjectGroupPython] S_element012  label="S_element : 004"  # scripted group (container) (typed FeaturePython)
  n = 1
  ref = S_element
FEATURE [App::DocumentObjectGroupPython] G4_GADOLINIUM_OXYSULFIDE  # scripted group (container) (typed FeaturePython)
  Dunit = g/cm3
  Dvalue = 7.44
  Group = -> [Gd_element001,O_element041,S_element012]
  conduct = 2
  density = 1
  expand = 3
  formula = G4_GADOLINIUM_OXYSULFIDE
  name = G4_GADOLINIUM_OXYSULFIDE
  specific = 4
FEATURE [App::DocumentObjectGroupPython] Ga_element001  label="Ga_element : 1"  # scripted group (container) (typed FeaturePython)
  n = 1
  ref = Ga_element
FEATURE [App::DocumentObjectGroupPython] As_element001  label="As_element : 1"  # scripted group (container) (typed FeaturePython)
  n = 1
  ref = As_element
FEATURE [App::DocumentObjectGroupPython] G4_GALLIUM_ARSENIDE  # scripted group (container) (typed FeaturePython)
  Dunit = g/cm3
  Dvalue = 5.31
  Group = -> [Ga_element001,As_element001]
  conduct = 2
  density = 1
  expand = 3
  formula = G4_GALLIUM_ARSENIDE
  name = G4_GALLIUM_ARSENIDE
  specific = 4
FEATURE [App::DocumentObjectGroupPython] H_element041  label="H_element : 0.081"  # scripted group (container) (typed FeaturePython)
  n = 0.08118
FEATURE [App::DocumentObjectGroupPython] C_element048  label="C_element : 0.416"  # scripted group (container) (typed FeaturePython)
  n = 0.41606
FEATURE [App::DocumentObjectGroupPython] N_element018  label="N_element : 0.111"  # scripted group (container) (typed FeaturePython)
  n = 0.11124
FEATURE [App::DocumentObjectGroupPython] O_element042  label="O_element : 0.381"  # scripted group (container) (typed FeaturePython)
  n = 0.38064
FEATURE [App::DocumentObjectGroupPython] S_element013  label="S_element : 0.011"  # scripted group (container) (typed FeaturePython)
  n = 0.01088
FEATURE [App::DocumentObjectGroupPython] G4_GEL_PHOTO_EMULSION  # scripted group (container) (typed FeaturePython)
  Dunit = g/cm3
  Dvalue = 1.2914
  Group = -> [H_element041,C_element048,N_element018,O_element042,S_element013]
  conduct = 2
  density = 1
  expand = 3
  formula = G4_GEL_PHOTO_EMULSION
  name = G4_GEL_PHOTO_EMULSION
  specific = 4
FEATURE [App::DocumentObjectGroupPython] B_element004  label="B_element : 0.040"  # scripted group (container) (typed FeaturePython)
  n = 0.0400639
FEATURE [App::DocumentObjectGroupPython] O_element043  label="O_element : 0.540"  # scripted group (container) (typed FeaturePython)
  n = 0.539561
FEATURE [App::DocumentObjectGroupPython] Na_element008  label="Na_element : 0.028"  # scripted group (container) (typed FeaturePython)
  n = 0.0281909
FEATURE [App::DocumentObjectGroupPython] Al_element003  label="Al_element : 0.012"  # scripted group (container) (typed FeaturePython)
  n = 0.011644
FEATURE [App::DocumentObjectGroupPython] Si_element003  label="Si_element : 0.377"  # scripted group (container) (typed FeaturePython)
  n = 0.377219
FEATURE [App::DocumentObjectGroupPython] K_element004  label="K_element : 0.014"  # scripted group (container) (typed FeaturePython)
  n = 0.00332099
FEATURE [App::DocumentObjectGroupPython] G4_Pyrex_Glass  # scripted group (container) (typed FeaturePython)
  Dunit = g/cm3
  Dvalue = 2.23
  Group = -> [B_element004,O_element043,Na_element008,Al_element003,Si_element003,K_element004]
  conduct = 2
  density = 1
  expand = 3
  formula = G4_Pyrex_Glass
  name = G4_Pyrex_Glass
  specific = 4
FEATURE [App::DocumentObjectGroupPython] O_element044  label="O_element : 0.156"  # scripted group (container) (typed FeaturePython)
  n = 0.156453
FEATURE [App::DocumentObjectGroupPython] Si_element004  label="Si_element : 0.081"  # scripted group (container) (typed FeaturePython)
  n = 0.080866
FEATURE [App::DocumentObjectGroupPython] Ti_element001  label="Ti_element : 0.008"  # scripted group (container) (typed FeaturePython)
  n = 0.008092
FEATURE [App::DocumentObjectGroupPython] As_element002  label="As_element : 0.003"  # scripted group (container) (typed FeaturePython)
  n = 0.002651
FEATURE [App::DocumentObjectGroupPython] Pb_element001  label="Pb_element : 0.752"  # scripted group (container) (typed FeaturePython)
  n = 0.751938
FEATURE [App::DocumentObjectGroupPython] G4_GLASS_LEAD  # scripted group (container) (typed FeaturePython)
  Dunit = g/cm3
  Dvalue = 6.22
  Group = -> [O_element044,Si_element004,Ti_element001,As_element002,Pb_element001]
  conduct = 2
  density = 1
  expand = 3
  formula = G4_GLASS_LEAD
  name = G4_GLASS_LEAD
  specific = 4
FEATURE [App::DocumentObjectGroupPython] O_element045  label="O_element : 0.460"  # scripted group (container) (typed FeaturePython)
  n = 0.4598
FEATURE [App::DocumentObjectGroupPython] Na_element009  label="Na_element : 0.096"  # scripted group (container) (typed FeaturePython)
  n = 0.0964411
FEATURE [App::DocumentObjectGroupPython] Si_element005  label="Si_element : 0.378"  # scripted group (container) (typed FeaturePython)
  n = 0.336553
FEATURE [App::DocumentObjectGroupPython] Ca_element011  label="Ca_element : 0.107"  # scripted group (container) (typed FeaturePython)
  n = 0.107205
FEATURE [App::DocumentObjectGroupPython] G4_GLASS_PLATE  # scripted group (container) (typed FeaturePython)
  Dunit = g/cm3
  Dvalue = 2.4
  Group = -> [O_element045,Na_element009,Si_element005,Ca_element011]
  conduct = 2
  density = 1
  expand = 3
  formula = G4_GLASS_PLATE
  name = G4_GLASS_PLATE
  specific = 4
FEATURE [App::DocumentObjectGroupPython] C_element049  label="C_element : 026"  # scripted group (container) (typed FeaturePython)
  n = 5
  ref = C_element
FEATURE [App::DocumentObjectGroupPython] H_element042  label="H_element : 021"  # scripted group (container) (typed FeaturePython)
  n = 10
  ref = H_element
FEATURE [App::DocumentObjectGroupPython] N_element019  label="N_element : 2"  # scripted group (container) (typed FeaturePython)
  n = 2
  ref = N_element
FEATURE [App::DocumentObjectGroupPython] O_element046  label="O_element : 022"  # scripted group (container) (typed FeaturePython)
  n = 3
  ref = O_element
FEATURE [App::DocumentObjectGroupPython] G4_GLUTAMINE  # scripted group (container) (typed FeaturePython)
  Dunit = g/cm3
  Dvalue = 1.46
  Group = -> [C_element049,H_element042,N_element019,O_element046]
  conduct = 2
  density = 1
  expand = 3
  formula = G4_GLUTAMINE
  name = G4_GLUTAMINE
  specific = 4
FEATURE [App::DocumentObjectGroupPython] C_element050  label="C_element : 027"  # scripted group (container) (typed FeaturePython)
  n = 3
  ref = C_element
FEATURE [App::DocumentObjectGroupPython] H_element043  label="H_element : 022"  # scripted group (container) (typed FeaturePython)
  n = 8
  ref = H_element
FEATURE [App::DocumentObjectGroupPython] O_element047  label="O_element : 023"  # scripted group (container) (typed FeaturePython)
  n = 3
  ref = O_element
FEATURE [App::DocumentObjectGroupPython] G4_GLYCEROL  # scripted group (container) (typed FeaturePython)
  Dunit = g/cm3
  Dvalue = 1.2613
  Group = -> [C_element050,H_element043,O_element047]
  conduct = 2
  density = 1
  expand = 3
  formula = G4_GLYCEROL
  name = G4_GLYCEROL
  specific = 4
FEATURE [App::DocumentObjectGroupPython] C_element051  label="C_element : 028"  # scripted group (container) (typed FeaturePython)
  n = 5
  ref = C_element
FEATURE [App::DocumentObjectGroupPython] H_element044  label="H_element : 023"  # scripted group (container) (typed FeaturePython)
  n = 5
  ref = H_element
FEATURE [App::DocumentObjectGroupPython] N_element020  label="N_element : 009"  # scripted group (container) (typed FeaturePython)
  n = 5
  ref = N_element
FEATURE [App::DocumentObjectGroupPython] O_element048  label="O_element : 024"  # scripted group (container) (typed FeaturePython)
  n = 1
  ref = O_element
FEATURE [App::DocumentObjectGroupPython] G4_GUANINE  # scripted group (container) (typed FeaturePython)
  Dunit = g/cm3
  Dvalue = 2.2
  Group = -> [C_element051,H_element044,N_element020,O_element048]
  conduct = 2
  density = 1
  expand = 3
  formula = G4_GUANINE
  name = G4_GUANINE
  specific = 4
FEATURE [App::DocumentObjectGroupPython] Ca_element012  label="Ca_element : 006"  # scripted group (container) (typed FeaturePython)
  n = 1
  ref = Ca_element
FEATURE [App::DocumentObjectGroupPython] S_element014  label="S_element : 005"  # scripted group (container) (typed FeaturePython)
  n = 1
  ref = S_element
FEATURE [App::DocumentObjectGroupPython] O_element049  label="O_element : 6"  # scripted group (container) (typed FeaturePython)
  n = 6
  ref = O_element
FEATURE [App::DocumentObjectGroupPython] H_element045  label="H_element : 024"  # scripted group (container) (typed FeaturePython)
  n = 4
  ref = H_element
FEATURE [App::DocumentObjectGroupPython] G4_GYPSUM  # scripted group (container) (typed FeaturePython)
  Dunit = g/cm3
  Dvalue = 2.32
  Group = -> [Ca_element012,S_element014,O_element049,H_element045]
  conduct = 2
  density = 1
  expand = 3
  formula = G4_GYPSUM
  name = G4_GYPSUM
  specific = 4
FEATURE [App::DocumentObjectGroupPython] C_element052  label="C_element : 7"  # scripted group (container) (typed FeaturePython)
  n = 7
  ref = C_element
FEATURE [App::DocumentObjectGroupPython] H_element046  label="H_element : 16"  # scripted group (container) (typed FeaturePython)
  n = 16
  ref = H_element
FEATURE [App::DocumentObjectGroupPython] G4_N_HEPTANE  label="G4_N-HEPTANE"  # scripted group (container) (typed FeaturePython)
  Dunit = g/cm3
  Dvalue = 0.68376
  Group = -> [C_element052,H_element046]
  conduct = 2
  density = 1
  expand = 3
  formula = G4_N-HEPTANE
  name = G4_N-HEPTANE
  specific = 4
FEATURE [App::DocumentObjectGroupPython] C_element053  label="C_element : 029"  # scripted group (container) (typed FeaturePython)
  n = 6
  ref = C_element
FEATURE [App::DocumentObjectGroupPython] H_element047  label="H_element : 14"  # scripted group (container) (typed FeaturePython)
  n = 14
  ref = H_element
FEATURE [App::DocumentObjectGroupPython] G4_N_HEXANE  label="G4_N-HEXANE"  # scripted group (container) (typed FeaturePython)
  Dunit = g/cm3
  Dvalue = 0.6603
  Group = -> [C_element053,H_element047]
  conduct = 2
  density = 1
  expand = 3
  formula = G4_N-HEXANE
  name = G4_N-HEXANE
  specific = 4
FEATURE [App::DocumentObjectGroupPython] C_element054  label="C_element : 22"  # scripted group (container) (typed FeaturePython)
  n = 22
  ref = C_element
FEATURE [App::DocumentObjectGroupPython] H_element048  label="H_element : 025"  # scripted group (container) (typed FeaturePython)
  n = 10
  ref = H_element
FEATURE [App::DocumentObjectGroupPython] N_element021  label="N_element : 010"  # scripted group (container) (typed FeaturePython)
  n = 2
  ref = N_element
FEATURE [App::DocumentObjectGroupPython] O_element050  label="O_element : 025"  # scripted group (container) (typed FeaturePython)
  n = 5
  ref = O_element
FEATURE [App::DocumentObjectGroupPython] G4_KAPTON  # scripted group (container) (typed FeaturePython)
  Dunit = g/cm3
  Dvalue = 1.42
  Group = -> [C_element054,H_element048,N_element021,O_element050]
  conduct = 2
  density = 1
  expand = 3
  formula = G4_KAPTON
  name = G4_KAPTON
  specific = 4
FEATURE [App::DocumentObjectGroupPython] La_element001  label="La_element : 1"  # scripted group (container) (typed FeaturePython)
  n = 1
  ref = La_element
FEATURE [App::DocumentObjectGroupPython] Br_element003  label="Br_element : 002"  # scripted group (container) (typed FeaturePython)
  n = 1
  ref = Br_element
FEATURE [App::DocumentObjectGroupPython] O_element051  label="O_element : 026"  # scripted group (container) (typed FeaturePython)
  n = 1
  ref = O_element
FEATURE [App::DocumentObjectGroupPython] G4_LANTHANUM_OXYBROMIDE  # scripted group (container) (typed FeaturePython)
  Dunit = g/cm3
  Dvalue = 6.28
  Group = -> [La_element001,Br_element003,O_element051]
  conduct = 2
  density = 1
  expand = 3
  formula = G4_LANTHANUM_OXYBROMIDE
  name = G4_LANTHANUM_OXYBROMIDE
  specific = 4
FEATURE [App::DocumentObjectGroupPython] La_element002  label="La_element : 2"  # scripted group (container) (typed FeaturePython)
  n = 2
  ref = La_element
FEATURE [App::DocumentObjectGroupPython] O_element052  label="O_element : 027"  # scripted group (container) (typed FeaturePython)
  n = 2
  ref = O_element
FEATURE [App::DocumentObjectGroupPython] S_element015  label="S_element : 006"  # scripted group (container) (typed FeaturePython)
  n = 1
  ref = S_element
FEATURE [App::DocumentObjectGroupPython] G4_LANTHANUM_OXYSULFIDE  # scripted group (container) (typed FeaturePython)
  Dunit = g/cm3
  Dvalue = 5.86
  Group = -> [La_element002,O_element052,S_element015]
  conduct = 2
  density = 1
  expand = 3
  formula = G4_LANTHANUM_OXYSULFIDE
  name = G4_LANTHANUM_OXYSULFIDE
  specific = 4
FEATURE [App::DocumentObjectGroupPython] O_element053  label="O_element : 0.072"  # scripted group (container) (typed FeaturePython)
  n = 0.071682
FEATURE [App::DocumentObjectGroupPython] Pb_element002  label="Pb_element : 0.928"  # scripted group (container) (typed FeaturePython)
  n = 0.928318
FEATURE [App::DocumentObjectGroupPython] G4_LEAD_OXIDE  # scripted group (container) (typed FeaturePython)
  Dunit = g/cm3
  Dvalue = 9.53
  Group = -> [O_element053,Pb_element002]
  conduct = 2
  density = 1
  expand = 3
  formula = G4_LEAD_OXIDE
  name = G4_LEAD_OXIDE
  specific = 4
FEATURE [App::DocumentObjectGroupPython] Li_element001  label="Li_element : 1"  # scripted group (container) (typed FeaturePython)
  n = 1
  ref = Li_element
FEATURE [App::DocumentObjectGroupPython] N_element022  label="N_element : 011"  # scripted group (container) (typed FeaturePython)
  n = 1
  ref = N_element
FEATURE [App::DocumentObjectGroupPython] H_element049  label="H_element : 026"  # scripted group (container) (typed FeaturePython)
  n = 2
  ref = H_element
FEATURE [App::DocumentObjectGroupPython] G4_LITHIUM_AMIDE  # scripted group (container) (typed FeaturePython)
  Dunit = g/cm3
  Dvalue = 1.178
  Group = -> [Li_element001,N_element022,H_element049]
  conduct = 2
  density = 1
  expand = 3
  formula = G4_LITHIUM_AMIDE
  name = G4_LITHIUM_AMIDE
  specific = 4
FEATURE [App::DocumentObjectGroupPython] Li_element002  label="Li_element : 2"  # scripted group (container) (typed FeaturePython)
  n = 2
  ref = Li_element
FEATURE [App::DocumentObjectGroupPython] C_element055  label="C_element : 030"  # scripted group (container) (typed FeaturePython)
  n = 1
  ref = C_element
FEATURE [App::DocumentObjectGroupPython] O_element054  label="O_element : 028"  # scripted group (container) (typed FeaturePython)
  n = 3
  ref = O_element
FEATURE [App::DocumentObjectGroupPython] G4_LITHIUM_CARBONATE  # scripted group (container) (typed FeaturePython)
  Dunit = g/cm3
  Dvalue = 2.11
  Group = -> [Li_element002,C_element055,O_element054]
  conduct = 2
  density = 1
  expand = 3
  formula = G4_LITHIUM_CARBONATE
  name = G4_LITHIUM_CARBONATE
  specific = 4
FEATURE [App::DocumentObjectGroupPython] Li_element003  label="Li_element : 003"  # scripted group (container) (typed FeaturePython)
  n = 1
  ref = Li_element
FEATURE [App::DocumentObjectGroupPython] F_element012  label="F_element : 004"  # scripted group (container) (typed FeaturePython)
  n = 1
  ref = F_element
FEATURE [App::DocumentObjectGroupPython] G4_LITHIUM_FLUORIDE  # scripted group (container) (typed FeaturePython)
  Dunit = g/cm3
  Dvalue = 2.635
  Group = -> [Li_element003,F_element012]
  conduct = 2
  density = 1
  expand = 3
  formula = G4_LITHIUM_FLUORIDE
  name = G4_LITHIUM_FLUORIDE
  specific = 4
FEATURE [App::DocumentObjectGroupPython] Li_element004  label="Li_element : 004"  # scripted group (container) (typed FeaturePython)
  n = 1
  ref = Li_element
FEATURE [App::DocumentObjectGroupPython] H_element050  label="H_element : 027"  # scripted group (container) (typed FeaturePython)
  n = 1
  ref = H_element
FEATURE [App::DocumentObjectGroupPython] G4_LITHIUM_HYDRIDE  # scripted group (container) (typed FeaturePython)
  Dunit = g/cm3
  Dvalue = 0.82
  Group = -> [Li_element004,H_element050]
  conduct = 2
  density = 1
  expand = 3
  formula = G4_LITHIUM_HYDRIDE
  name = G4_LITHIUM_HYDRIDE
  specific = 4
FEATURE [App::DocumentObjectGroupPython] Li_element005  label="Li_element : 005"  # scripted group (container) (typed FeaturePython)
  n = 1
  ref = Li_element
FEATURE [App::DocumentObjectGroupPython] I_element003  label="I_element : 002"  # scripted group (container) (typed FeaturePython)
  n = 1
  ref = I_element
FEATURE [App::DocumentObjectGroupPython] G4_LITHIUM_IODIDE  # scripted group (container) (typed FeaturePython)
  Dunit = g/cm3
  Dvalue = 3.494
  Group = -> [Li_element005,I_element003]
  conduct = 2
  density = 1
  expand = 3
  formula = G4_LITHIUM_IODIDE
  name = G4_LITHIUM_IODIDE
  specific = 4
FEATURE [App::DocumentObjectGroupPython] Li_element006  label="Li_element : 006"  # scripted group (container) (typed FeaturePython)
  n = 2
  ref = Li_element
FEATURE [App::DocumentObjectGroupPython] O_element055  label="O_element : 029"  # scripted group (container) (typed FeaturePython)
  n = 1
  ref = O_element
FEATURE [App::DocumentObjectGroupPython] G4_LITHIUM_OXIDE  # scripted group (container) (typed FeaturePython)
  Dunit = g/cm3
  Dvalue = 2.013
  Group = -> [Li_element006,O_element055]
  conduct = 2
  density = 1
  expand = 3
  formula = G4_LITHIUM_OXIDE
  name = G4_LITHIUM_OXIDE
  specific = 4
FEATURE [App::DocumentObjectGroupPython] Li_element007  label="Li_element : 007"  # scripted group (container) (typed FeaturePython)
  n = 2
  ref = Li_element
FEATURE [App::DocumentObjectGroupPython] B_element005  label="B_element : 005"  # scripted group (container) (typed FeaturePython)
  n = 4
  ref = B_element
FEATURE [App::DocumentObjectGroupPython] O_element056  label="O_element : 7"  # scripted group (container) (typed FeaturePython)
  n = 7
  ref = O_element
FEATURE [App::DocumentObjectGroupPython] G4_LITHIUM_TETRABORATE  # scripted group (container) (typed FeaturePython)
  Dunit = g/cm3
  Dvalue = 2.44
  Group = -> [Li_element007,B_element005,O_element056]
  conduct = 2
  density = 1
  expand = 3
  formula = G4_LITHIUM_TETRABORATE
  name = G4_LITHIUM_TETRABORATE
  specific = 4
FEATURE [App::DocumentObjectGroupPython] H_element051  label="H_element : 0.105"  # scripted group (container) (typed FeaturePython)
  n = 0.105
FEATURE [App::DocumentObjectGroupPython] C_element056  label="C_element : 0.083"  # scripted group (container) (typed FeaturePython)
  n = 0.083
FEATURE [App::DocumentObjectGroupPython] N_element023  label="N_element : 0.023"  # scripted group (container) (typed FeaturePython)
  n = 0.023
FEATURE [App::DocumentObjectGroupPython] O_element057  label="O_element : 0.779"  # scripted group (container) (typed FeaturePython)
  n = 0.779
FEATURE [App::DocumentObjectGroupPython] Na_element010  label="Na_element : 0.097"  # scripted group (container) (typed FeaturePython)
  n = 0.002
FEATURE [App::DocumentObjectGroupPython] P_element006  label="P_element : 0.105"  # scripted group (container) (typed FeaturePython)
  n = 0.001
FEATURE [App::DocumentObjectGroupPython] S_element016  label="S_element : 0.017"  # scripted group (container) (typed FeaturePython)
  n = 0.002
FEATURE [App::DocumentObjectGroupPython] Cl_element014  label="Cl_element : 0.587"  # scripted group (container) (typed FeaturePython)
  n = 0.003
FEATURE [App::DocumentObjectGroupPython] K_element005  label="K_element : 0.015"  # scripted group (container) (typed FeaturePython)
  n = 0.002
FEATURE [App::DocumentObjectGroupPython] G4_LUNG_ICRP  # scripted group (container) (typed FeaturePython)
  Dunit = g/cm3
  Dvalue = 1.04
  Group = -> [H_element051,C_element056,N_element023,O_element057,Na_element010,P_element006,S_element016,Cl_element014,K_element005]
  conduct = 2
  density = 1
  expand = 3
  formula = G4_LUNG_ICRP
  name = G4_LUNG_ICRP
  specific = 4
FEATURE [App::DocumentObjectGroupPython] H_element052  label="H_element : 0.116"  # scripted group (container) (typed FeaturePython)
  n = 0.114318
FEATURE [App::DocumentObjectGroupPython] C_element057  label="C_element : 0.656"  # scripted group (container) (typed FeaturePython)
  n = 0.655824
FEATURE [App::DocumentObjectGroupPython] O_element058  label="O_element : 0.092"  # scripted group (container) (typed FeaturePython)
  n = 0.0921831
FEATURE [App::DocumentObjectGroupPython] Mg_element004  label="Mg_element : 0.135"  # scripted group (container) (typed FeaturePython)
  n = 0.134792
FEATURE [App::DocumentObjectGroupPython] Ca_element013  label="Ca_element : 0.003"  # scripted group (container) (typed FeaturePython)
  n = 0.002883
FEATURE [App::DocumentObjectGroupPython] G4_M3_WAX  # scripted group (container) (typed FeaturePython)
  Dunit = g/cm3
  Dvalue = 1.05
  Group = -> [H_element052,C_element057,O_element058,Mg_element004,Ca_element013]
  conduct = 2
  density = 1
  expand = 3
  formula = G4_M3_WAX
  name = G4_M3_WAX
  specific = 4
FEATURE [App::DocumentObjectGroupPython] Mg_element005  label="Mg_element : 1"  # scripted group (container) (typed FeaturePython)
  n = 1
  ref = Mg_element
FEATURE [App::DocumentObjectGroupPython] C_element058  label="C_element : 031"  # scripted group (container) (typed FeaturePython)
  n = 1
  ref = C_element
FEATURE [App::DocumentObjectGroupPython] O_element059  label="O_element : 030"  # scripted group (container) (typed FeaturePython)
  n = 3
  ref = O_element
FEATURE [App::DocumentObjectGroupPython] G4_MAGNESIUM_CARBONATE  # scripted group (container) (typed FeaturePython)
  Dunit = g/cm3
  Dvalue = 2.958
  Group = -> [Mg_element005,C_element058,O_element059]
  conduct = 2
  density = 1
  expand = 3
  formula = G4_MAGNESIUM_CARBONATE
  name = G4_MAGNESIUM_CARBONATE
  specific = 4
FEATURE [App::DocumentObjectGroupPython] Mg_element006  label="Mg_element : 002"  # scripted group (container) (typed FeaturePython)
  n = 1
  ref = Mg_element
FEATURE [App::DocumentObjectGroupPython] F_element013  label="F_element : 005"  # scripted group (container) (typed FeaturePython)
  n = 2
  ref = F_element
FEATURE [App::DocumentObjectGroupPython] G4_MAGNESIUM_FLUORIDE  # scripted group (container) (typed FeaturePython)
  Dunit = g/cm3
  Dvalue = 3
  Group = -> [Mg_element006,F_element013]
  conduct = 2
  density = 1
  expand = 3
  formula = G4_MAGNESIUM_FLUORIDE
  name = G4_MAGNESIUM_FLUORIDE
  specific = 4
FEATURE [App::DocumentObjectGroupPython] Mg_element007  label="Mg_element : 003"  # scripted group (container) (typed FeaturePython)
  n = 1
  ref = Mg_element
FEATURE [App::DocumentObjectGroupPython] O_element060  label="O_element : 031"  # scripted group (container) (typed FeaturePython)
  n = 1
  ref = O_element
FEATURE [App::DocumentObjectGroupPython] G4_MAGNESIUM_OXIDE  # scripted group (container) (typed FeaturePython)
  Dunit = g/cm3
  Dvalue = 3.58
  Group = -> [Mg_element007,O_element060]
  conduct = 2
  density = 1
  expand = 3
  formula = G4_MAGNESIUM_OXIDE
  name = G4_MAGNESIUM_OXIDE
  specific = 4
FEATURE [App::DocumentObjectGroupPython] Mg_element008  label="Mg_element : 004"  # scripted group (container) (typed FeaturePython)
  n = 1
  ref = Mg_element
FEATURE [App::DocumentObjectGroupPython] B_element006  label="B_element : 006"  # scripted group (container) (typed FeaturePython)
  n = 4
  ref = B_element
FEATURE [App::DocumentObjectGroupPython] O_element061  label="O_element : 032"  # scripted group (container) (typed FeaturePython)
  n = 7
  ref = O_element
FEATURE [App::DocumentObjectGroupPython] G4_MAGNESIUM_TETRABORATE  # scripted group (container) (typed FeaturePython)
  Dunit = g/cm3
  Dvalue = 2.53
  Group = -> [Mg_element008,B_element006,O_element061]
  conduct = 2
  density = 1
  expand = 3
  formula = G4_MAGNESIUM_TETRABORATE
  name = G4_MAGNESIUM_TETRABORATE
  specific = 4
FEATURE [App::DocumentObjectGroupPython] Hg_element001  label="Hg_element : 1"  # scripted group (container) (typed FeaturePython)
  n = 1
  ref = Hg_element
FEATURE [App::DocumentObjectGroupPython] I_element004  label="I_element : 2"  # scripted group (container) (typed FeaturePython)
  n = 2
  ref = I_element
FEATURE [App::DocumentObjectGroupPython] G4_MERCURIC_IODIDE  # scripted group (container) (typed FeaturePython)
  Dunit = g/cm3
  Dvalue = 6.36
  Group = -> [Hg_element001,I_element004]
  conduct = 2
  density = 1
  expand = 3
  formula = G4_MERCURIC_IODIDE
  name = G4_MERCURIC_IODIDE
  specific = 4
FEATURE [App::DocumentObjectGroupPython] C_element059  label="C_element : 032"  # scripted group (container) (typed FeaturePython)
  n = 1
  ref = C_element
FEATURE [App::DocumentObjectGroupPython] H_element053  label="H_element : 028"  # scripted group (container) (typed FeaturePython)
  n = 4
  ref = H_element
FEATURE [App::DocumentObjectGroupPython] G4_METHANE  # scripted group (container) (typed FeaturePython)
  Dunit = g/cm3
  Dvalue = 0.000667151
  Group = -> [C_element059,H_element053]
  conduct = 2
  density = 1
  expand = 3
  formula = G4_METHANE
  name = G4_METHANE
  specific = 4
FEATURE [App::DocumentObjectGroupPython] C_element060  label="C_element : 033"  # scripted group (container) (typed FeaturePython)
  n = 1
  ref = C_element
FEATURE [App::DocumentObjectGroupPython] H_element054  label="H_element : 029"  # scripted group (container) (typed FeaturePython)
  n = 4
  ref = H_element
FEATURE [App::DocumentObjectGroupPython] O_element062  label="O_element : 033"  # scripted group (container) (typed FeaturePython)
  n = 1
  ref = O_element
FEATURE [App::DocumentObjectGroupPython] G4_METHANOL  # scripted group (container) (typed FeaturePython)
  Dunit = g/cm3
  Dvalue = 0.7914
  Group = -> [C_element060,H_element054,O_element062]
  conduct = 2
  density = 1
  expand = 3
  formula = G4_METHANOL
  name = G4_METHANOL
  specific = 4
FEATURE [App::DocumentObjectGroupPython] H_element055  label="H_element : 0.134"  # scripted group (container) (typed FeaturePython)
  n = 0.13404
FEATURE [App::DocumentObjectGroupPython] C_element061  label="C_element : 0.778"  # scripted group (container) (typed FeaturePython)
  n = 0.77796
FEATURE [App::DocumentObjectGroupPython] O_element063  label="O_element : 0.035"  # scripted group (container) (typed FeaturePython)
  n = 0.03502
FEATURE [App::DocumentObjectGroupPython] Mg_element009  label="Mg_element : 0.039"  # scripted group (container) (typed FeaturePython)
  n = 0.038594
FEATURE [App::DocumentObjectGroupPython] Ti_element002  label="Ti_element : 0.014"  # scripted group (container) (typed FeaturePython)
  n = 0.014386
FEATURE [App::DocumentObjectGroupPython] G4_MIX_D_WAX  # scripted group (container) (typed FeaturePython)
  Dunit = g/cm3
  Dvalue = 0.99
  Group = -> [H_element055,C_element061,O_element063,Mg_element009,Ti_element002]
  conduct = 2
  density = 1
  expand = 3
  formula = G4_MIX_D_WAX
  name = G4_MIX_D_WAX
  specific = 4
FEATURE [App::DocumentObjectGroupPython] H_element056  label="H_element : 0.135"  # scripted group (container) (typed FeaturePython)
  n = 0.081192
FEATURE [App::DocumentObjectGroupPython] C_element062  label="C_element : 0.583"  # scripted group (container) (typed FeaturePython)
  n = 0.583442
FEATURE [App::DocumentObjectGroupPython] N_element024  label="N_element : 0.018"  # scripted group (container) (typed FeaturePython)
  n = 0.017798
FEATURE [App::DocumentObjectGroupPython] O_element064  label="O_element : 0.186"  # scripted group (container) (typed FeaturePython)
  n = 0.186381
FEATURE [App::DocumentObjectGroupPython] Mg_element010  label="Mg_element : 0.130"  # scripted group (container) (typed FeaturePython)
  n = 0.130287
FEATURE [App::DocumentObjectGroupPython] Cl_element015  label="Cl_element : 0.588"  # scripted group (container) (typed FeaturePython)
  n = 0.0009
FEATURE [App::DocumentObjectGroupPython] G4_MS20_TISSUE  # scripted group (container) (typed FeaturePython)
  Dunit = g/cm3
  Dvalue = 1
  Group = -> [H_element056,C_element062,N_element024,O_element064,Mg_element010,Cl_element015]
  conduct = 2
  density = 1
  expand = 3
  formula = G4_MS20_TISSUE
  name = G4_MS20_TISSUE
  specific = 4
FEATURE [App::DocumentObjectGroupPython] H_element057  label="H_element : 0.136"  # scripted group (container) (typed FeaturePython)
  n = 0.102
FEATURE [App::DocumentObjectGroupPython] C_element063  label="C_element : 0.143"  # scripted group (container) (typed FeaturePython)
  n = 0.143
FEATURE [App::DocumentObjectGroupPython] N_element025  label="N_element : 0.034"  # scripted group (container) (typed FeaturePython)
  n = 0.034
FEATURE [App::DocumentObjectGroupPython] O_element065  label="O_element : 0.710"  # scripted group (container) (typed FeaturePython)
  n = 0.71
FEATURE [App::DocumentObjectGroupPython] Na_element011  label="Na_element : 0.098"  # scripted group (container) (typed FeaturePython)
  n = 0.001
FEATURE [App::DocumentObjectGroupPython] P_element007  label="P_element : 0.002"  # scripted group (container) (typed FeaturePython)
  n = 0.002
FEATURE [App::DocumentObjectGroupPython] S_element017  label="S_element : 0.018"  # scripted group (container) (typed FeaturePython)
  n = 0.003
FEATURE [App::DocumentObjectGroupPython] Cl_element016  label="Cl_element : 0.589"  # scripted group (container) (typed FeaturePython)
  n = 0.001
FEATURE [App::DocumentObjectGroupPython] K_element006  label="K_element : 0.004"  # scripted group (container) (typed FeaturePython)
  n = 0.004
FEATURE [App::DocumentObjectGroupPython] G4_MUSCLE_SKELETAL_ICRP  # scripted group (container) (typed FeaturePython)
  Dunit = g/cm3
  Dvalue = 1.05
  Group = -> [H_element057,C_element063,N_element025,O_element065,Na_element011,P_element007,S_element017,Cl_element016,K_element006]
  conduct = 2
  density = 1
  expand = 3
  formula = G4_MUSCLE_SKELETAL_ICRP
  name = G4_MUSCLE_SKELETAL_ICRP
  specific = 4
FEATURE [App::DocumentObjectGroupPython] H_element058  label="H_element : 0.137"  # scripted group (container) (typed FeaturePython)
  n = 0.102102
FEATURE [App::DocumentObjectGroupPython] C_element064  label="C_element : 0.123"  # scripted group (container) (typed FeaturePython)
  n = 0.123123
FEATURE [App::DocumentObjectGroupPython] N_element026  label="N_element : 0.756"  # scripted group (container) (typed FeaturePython)
  n = 0.035035
FEATURE [App::DocumentObjectGroupPython] O_element066  label="O_element : 0.730"  # scripted group (container) (typed FeaturePython)
  n = 0.72973
FEATURE [App::DocumentObjectGroupPython] Na_element012  label="Na_element : 0.099"  # scripted group (container) (typed FeaturePython)
  n = 0.001001
FEATURE [App::DocumentObjectGroupPython] P_element008  label="P_element : 0.106"  # scripted group (container) (typed FeaturePython)
  n = 0.002002
FEATURE [App::DocumentObjectGroupPython] S_element018  label="S_element : 0.019"  # scripted group (container) (typed FeaturePython)
  n = 0.004004
FEATURE [App::DocumentObjectGroupPython] K_element007  label="K_element : 0.016"  # scripted group (container) (typed FeaturePython)
  n = 0.003003
FEATURE [App::DocumentObjectGroupPython] G4_MUSCLE_STRIATED_ICRU  # scripted group (container) (typed FeaturePython)
  Dunit = g/cm3
  Dvalue = 1.04
  Group = -> [H_element058,C_element064,N_element026,O_element066,Na_element012,P_element008,S_element018,K_element007]
  conduct = 2
  density = 1
  expand = 3
  formula = G4_MUSCLE_STRIATED_ICRU
  name = G4_MUSCLE_STRIATED_ICRU
  specific = 4
FEATURE [App::DocumentObjectGroupPython] H_element059  label="H_element : 0.098"  # scripted group (container) (typed FeaturePython)
  n = 0.0982341
FEATURE [App::DocumentObjectGroupPython] C_element065  label="C_element : 0.156"  # scripted group (container) (typed FeaturePython)
  n = 0.156214
FEATURE [App::DocumentObjectGroupPython] N_element027  label="N_element : 0.757"  # scripted group (container) (typed FeaturePython)
  n = 0.035451
FEATURE [App::DocumentObjectGroupPython] O_element067  label="O_element : 0.880"  # scripted group (container) (typed FeaturePython)
  n = 0.710101
FEATURE [App::DocumentObjectGroupPython] G4_MUSCLE_WITH_SUCROSE  # scripted group (container) (typed FeaturePython)
  Dunit = g/cm3
  Dvalue = 1.11
  Group = -> [H_element059,C_element065,N_element027,O_element067]
  conduct = 2
  density = 1
  expand = 3
  formula = G4_MUSCLE_WITH_SUCROSE
  name = G4_MUSCLE_WITH_SUCROSE
  specific = 4
FEATURE [App::DocumentObjectGroupPython] H_element060  label="H_element : 0.138"  # scripted group (container) (typed FeaturePython)
  n = 0.101969
FEATURE [App::DocumentObjectGroupPython] C_element066  label="C_element : 0.120"  # scripted group (container) (typed FeaturePython)
  n = 0.120058
FEATURE [App::DocumentObjectGroupPython] N_element028  label="N_element : 0.758"  # scripted group (container) (typed FeaturePython)
  n = 0.035451
FEATURE [App::DocumentObjectGroupPython] O_element068  label="O_element : 0.743"  # scripted group (container) (typed FeaturePython)
  n = 0.742522
FEATURE [App::DocumentObjectGroupPython] G4_MUSCLE_WITHOUT_SUCROSE  # scripted group (container) (typed FeaturePython)
  Dunit = g/cm3
  Dvalue = 1.07
  Group = -> [H_element060,C_element066,N_element028,O_element068]
  conduct = 2
  density = 1
  expand = 3
  formula = G4_MUSCLE_WITHOUT_SUCROSE
  name = G4_MUSCLE_WITHOUT_SUCROSE
  specific = 4
FEATURE [App::DocumentObjectGroupPython] C_element067  label="C_element : 10"  # scripted group (container) (typed FeaturePython)
  n = 10
  ref = C_element
FEATURE [App::DocumentObjectGroupPython] H_element061  label="H_element : 030"  # scripted group (container) (typed FeaturePython)
  n = 8
  ref = H_element
FEATURE [App::DocumentObjectGroupPython] G4_NAPHTHALENE  # scripted group (container) (typed FeaturePython)
  Dunit = g/cm3
  Dvalue = 1.145
  Group = -> [C_element067,H_element061]
  conduct = 2
  density = 1
  expand = 3
  formula = G4_NAPHTHALENE
  name = G4_NAPHTHALENE
  specific = 4
FEATURE [App::DocumentObjectGroupPython] C_element068  label="C_element : 034"  # scripted group (container) (typed FeaturePython)
  n = 6
  ref = C_element
FEATURE [App::DocumentObjectGroupPython] H_element062  label="H_element : 031"  # scripted group (container) (typed FeaturePython)
  n = 5
  ref = H_element
FEATURE [App::DocumentObjectGroupPython] N_element029  label="N_element : 012"  # scripted group (container) (typed FeaturePython)
  n = 1
  ref = N_element
FEATURE [App::DocumentObjectGroupPython] O_element069  label="O_element : 034"  # scripted group (container) (typed FeaturePython)
  n = 2
  ref = O_element
FEATURE [App::DocumentObjectGroupPython] G4_NITROBENZENE  # scripted group (container) (typed FeaturePython)
  Dunit = g/cm3
  Dvalue = 1.19867
  Group = -> [C_element068,H_element062,N_element029,O_element069]
  conduct = 2
  density = 1
  expand = 3
  formula = G4_NITROBENZENE
  name = G4_NITROBENZENE
  specific = 4
FEATURE [App::DocumentObjectGroupPython] N_element030  label="N_element : 013"  # scripted group (container) (typed FeaturePython)
  n = 2
  ref = N_element
FEATURE [App::DocumentObjectGroupPython] O_element070  label="O_element : 035"  # scripted group (container) (typed FeaturePython)
  n = 1
  ref = O_element
FEATURE [App::DocumentObjectGroupPython] G4_NITROUS_OXIDE  # scripted group (container) (typed FeaturePython)
  Dunit = g/cm3
  Dvalue = 0.00183094
  Group = -> [N_element030,O_element070]
  conduct = 2
  density = 1
  expand = 3
  formula = G4_NITROUS_OXIDE
  name = G4_NITROUS_OXIDE
  specific = 4
FEATURE [App::DocumentObjectGroupPython] H_element063  label="H_element : 0.104"  # scripted group (container) (typed FeaturePython)
  n = 0.103509
FEATURE [App::DocumentObjectGroupPython] C_element069  label="C_element : 0.648"  # scripted group (container) (typed FeaturePython)
  n = 0.648416
FEATURE [App::DocumentObjectGroupPython] N_element031  label="N_element : 0.100"  # scripted group (container) (typed FeaturePython)
  n = 0.0995361
FEATURE [App::DocumentObjectGroupPython] O_element071  label="O_element : 0.149"  # scripted group (container) (typed FeaturePython)
  n = 0.148539
FEATURE [App::DocumentObjectGroupPython] G4_NYLON_8062  label="G4_NYLON-8062"  # scripted group (container) (typed FeaturePython)
  Dunit = g/cm3
  Dvalue = 1.08
  Group = -> [H_element063,C_element069,N_element031,O_element071]
  conduct = 2
  density = 1
  expand = 3
  formula = G4_NYLON-8062
  name = G4_NYLON-8062
  specific = 4
FEATURE [App::DocumentObjectGroupPython] C_element070  label="C_element : 035"  # scripted group (container) (typed FeaturePython)
  n = 6
  ref = C_element
FEATURE [App::DocumentObjectGroupPython] H_element064  label="H_element : 11"  # scripted group (container) (typed FeaturePython)
  n = 11
  ref = H_element
FEATURE [App::DocumentObjectGroupPython] N_element032  label="N_element : 014"  # scripted group (container) (typed FeaturePython)
  n = 1
  ref = N_element
FEATURE [App::DocumentObjectGroupPython] O_element072  label="O_element : 036"  # scripted group (container) (typed FeaturePython)
  n = 1
  ref = O_element
FEATURE [App::DocumentObjectGroupPython] G4_NYLON_6_6  label="G4_NYLON-6-6"  # scripted group (container) (typed FeaturePython)
  Dunit = g/cm3
  Dvalue = 1.14
  Group = -> [C_element070,H_element064,N_element032,O_element072]
  conduct = 2
  density = 1
  expand = 3
  formula = G4_NYLON-6-6
  name = G4_NYLON-6-6
  specific = 4
FEATURE [App::DocumentObjectGroupPython] H_element065  label="H_element : 0.139"  # scripted group (container) (typed FeaturePython)
  n = 0.107062
FEATURE [App::DocumentObjectGroupPython] C_element071  label="C_element : 0.680"  # scripted group (container) (typed FeaturePython)
  n = 0.680449
FEATURE [App::DocumentObjectGroupPython] N_element033  label="N_element : 0.099"  # scripted group (container) (typed FeaturePython)
  n = 0.099189
FEATURE [App::DocumentObjectGroupPython] O_element073  label="O_element : 0.113"  # scripted group (container) (typed FeaturePython)
  n = 0.1133
FEATURE [App::DocumentObjectGroupPython] G4_NYLON_6_10  label="G4_NYLON-6-10"  # scripted group (container) (typed FeaturePython)
  Dunit = g/cm3
  Dvalue = 1.14
  Group = -> [H_element065,C_element071,N_element033,O_element073]
  conduct = 2
  density = 1
  expand = 3
  formula = G4_NYLON-6-10
  name = G4_NYLON-6-10
  specific = 4
FEATURE [App::DocumentObjectGroupPython] H_element066  label="H_element : 0.140"  # scripted group (container) (typed FeaturePython)
  n = 0.115476
FEATURE [App::DocumentObjectGroupPython] C_element072  label="C_element : 0.721"  # scripted group (container) (typed FeaturePython)
  n = 0.720818
FEATURE [App::DocumentObjectGroupPython] N_element034  label="N_element : 0.076"  # scripted group (container) (typed FeaturePython)
  n = 0.0764169
FEATURE [App::DocumentObjectGroupPython] O_element074  label="O_element : 0.087"  # scripted group (container) (typed FeaturePython)
  n = 0.0872889
FEATURE [App::DocumentObjectGroupPython] G4_NYLON_11_RILSAN  label="G4_NYLON-11_RILSAN"  # scripted group (container) (typed FeaturePython)
  Dunit = g/cm3
  Dvalue = 1.425
  Group = -> [H_element066,C_element072,N_element034,O_element074]
  conduct = 2
  density = 1
  expand = 3
  formula = G4_NYLON-11_RILSAN
  name = G4_NYLON-11_RILSAN
  specific = 4
FEATURE [App::DocumentObjectGroupPython] C_element073  label="C_element : 8"  # scripted group (container) (typed FeaturePython)
  n = 8
  ref = C_element
FEATURE [App::DocumentObjectGroupPython] H_element067  label="H_element : 18"  # scripted group (container) (typed FeaturePython)
  n = 18
  ref = H_element
FEATURE [App::DocumentObjectGroupPython] G4_OCTANE  # scripted group (container) (typed FeaturePython)
  Dunit = g/cm3
  Dvalue = 0.7026
  Group = -> [C_element073,H_element067]
  conduct = 2
  density = 1
  expand = 3
  formula = G4_OCTANE
  name = G4_OCTANE
  specific = 4
FEATURE [App::DocumentObjectGroupPython] C_element074  label="C_element : 25"  # scripted group (container) (typed FeaturePython)
  n = 25
  ref = C_element
FEATURE [App::DocumentObjectGroupPython] H_element068  label="H_element : 52"  # scripted group (container) (typed FeaturePython)
  n = 52
  ref = H_element
FEATURE [App::DocumentObjectGroupPython] G4_PARAFFIN  # scripted group (container) (typed FeaturePython)
  Dunit = g/cm3
  Dvalue = 0.93
  Group = -> [C_element074,H_element068]
  conduct = 2
  density = 1
  expand = 3
  formula = G4_PARAFFIN
  name = G4_PARAFFIN
  specific = 4
FEATURE [App::DocumentObjectGroupPython] C_element075  label="C_element : 036"  # scripted group (container) (typed FeaturePython)
  n = 5
  ref = C_element
FEATURE [App::DocumentObjectGroupPython] H_element069  label="H_element : 032"  # scripted group (container) (typed FeaturePython)
  n = 12
  ref = H_element
FEATURE [App::DocumentObjectGroupPython] G4_N_PENTANE  label="G4_N-PENTANE"  # scripted group (container) (typed FeaturePython)
  Dunit = g/cm3
  Dvalue = 0.6262
  Group = -> [C_element075,H_element069]
  conduct = 2
  density = 1
  expand = 3
  formula = G4_N-PENTANE
  name = G4_N-PENTANE
  specific = 4
FEATURE [App::DocumentObjectGroupPython] H_element070  label="H_element : 0.014"  # scripted group (container) (typed FeaturePython)
  n = 0.0141
FEATURE [App::DocumentObjectGroupPython] C_element076  label="C_element : 0.072"  # scripted group (container) (typed FeaturePython)
  n = 0.072261
FEATURE [App::DocumentObjectGroupPython] N_element035  label="N_element : 0.019"  # scripted group (container) (typed FeaturePython)
  n = 0.01932
FEATURE [App::DocumentObjectGroupPython] O_element075  label="O_element : 0.066"  # scripted group (container) (typed FeaturePython)
  n = 0.066101
FEATURE [App::DocumentObjectGroupPython] S_element019  label="S_element : 0.020"  # scripted group (container) (typed FeaturePython)
  n = 0.00189
FEATURE [App::DocumentObjectGroupPython] Br_element004  label="Br_element : 0.349"  # scripted group (container) (typed FeaturePython)
  n = 0.349103
FEATURE [App::DocumentObjectGroupPython] Ag_element001  label="Ag_element : 0.474"  # scripted group (container) (typed FeaturePython)
  n = 0.474105
FEATURE [App::DocumentObjectGroupPython] I_element005  label="I_element : 0.003"  # scripted group (container) (typed FeaturePython)
  n = 0.00312
FEATURE [App::DocumentObjectGroupPython] G4_PHOTO_EMULSION  # scripted group (container) (typed FeaturePython)
  Dunit = g/cm3
  Dvalue = 3.815
  Group = -> [H_element070,C_element076,N_element035,O_element075,S_element019,Br_element004,Ag_element001,I_element005]
  conduct = 2
  density = 1
  expand = 3
  formula = G4_PHOTO_EMULSION
  name = G4_PHOTO_EMULSION
  specific = 4
FEATURE [App::DocumentObjectGroupPython] C_element077  label="C_element : 9"  # scripted group (container) (typed FeaturePython)
  n = 9
  ref = C_element
FEATURE [App::DocumentObjectGroupPython] H_element071  label="H_element : 033"  # scripted group (container) (typed FeaturePython)
  n = 10
  ref = H_element
FEATURE [App::DocumentObjectGroupPython] G4_PLASTIC_SC_VINYLTOLUENE  # scripted group (container) (typed FeaturePython)
  Dunit = g/cm3
  Dvalue = 1.032
  Group = -> [C_element077,H_element071]
  conduct = 2
  density = 1
  expand = 3
  formula = G4_PLASTIC_SC_VINYLTOLUENE
  name = G4_PLASTIC_SC_VINYLTOLUENE
  specific = 4
FEATURE [App::DocumentObjectGroupPython] Pu_element001  label="Pu_element : 1"  # scripted group (container) (typed FeaturePython)
  n = 1
  ref = Pu_element
FEATURE [App::DocumentObjectGroupPython] O_element076  label="O_element : 037"  # scripted group (container) (typed FeaturePython)
  n = 2
  ref = O_element
FEATURE [App::DocumentObjectGroupPython] G4_PLUTONIUM_DIOXIDE  # scripted group (container) (typed FeaturePython)
  Dunit = g/cm3
  Dvalue = 11.46
  Group = -> [Pu_element001,O_element076]
  conduct = 2
  density = 1
  expand = 3
  formula = G4_PLUTONIUM_DIOXIDE
  name = G4_PLUTONIUM_DIOXIDE
  specific = 4
FEATURE [App::DocumentObjectGroupPython] C_element078  label="C_element : 037"  # scripted group (container) (typed FeaturePython)
  n = 3
  ref = C_element
FEATURE [App::DocumentObjectGroupPython] H_element072  label="H_element : 034"  # scripted group (container) (typed FeaturePython)
  n = 3
  ref = H_element
FEATURE [App::DocumentObjectGroupPython] N_element036  label="N_element : 015"  # scripted group (container) (typed FeaturePython)
  n = 1
  ref = N_element
FEATURE [App::DocumentObjectGroupPython] G4_POLYACRYLONITRILE  # scripted group (container) (typed FeaturePython)
  Dunit = g/cm3
  Dvalue = 1.17
  Group = -> [C_element078,H_element072,N_element036]
  conduct = 2
  density = 1
  expand = 3
  formula = G4_POLYACRYLONITRILE
  name = G4_POLYACRYLONITRILE
  specific = 4
FEATURE [App::DocumentObjectGroupPython] C_element079  label="C_element : 16"  # scripted group (container) (typed FeaturePython)
  n = 16
  ref = C_element
FEATURE [App::DocumentObjectGroupPython] H_element073  label="H_element : 035"  # scripted group (container) (typed FeaturePython)
  n = 14
  ref = H_element
FEATURE [App::DocumentObjectGroupPython] O_element077  label="O_element : 038"  # scripted group (container) (typed FeaturePython)
  n = 3
  ref = O_element
FEATURE [App::DocumentObjectGroupPython] G4_POLYCARBONATE  # scripted group (container) (typed FeaturePython)
  Dunit = g/cm3
  Dvalue = 1.2
  Group = -> [C_element079,H_element073,O_element077]
  conduct = 2
  density = 1
  expand = 3
  formula = G4_POLYCARBONATE
  name = G4_POLYCARBONATE
  specific = 4
FEATURE [App::DocumentObjectGroupPython] C_element080  label="C_element : 038"  # scripted group (container) (typed FeaturePython)
  n = 8
  ref = C_element
FEATURE [App::DocumentObjectGroupPython] H_element074  label="H_element : 036"  # scripted group (container) (typed FeaturePython)
  n = 7
  ref = H_element
FEATURE [App::DocumentObjectGroupPython] Cl_element017  label="Cl_element : 007"  # scripted group (container) (typed FeaturePython)
  n = 1
  ref = Cl_element
FEATURE [App::DocumentObjectGroupPython] G4_POLYCHLOROSTYRENE  # scripted group (container) (typed FeaturePython)
  Dunit = g/cm3
  Dvalue = 1.3
  Group = -> [C_element080,H_element074,Cl_element017]
  conduct = 2
  density = 1
  expand = 3
  formula = G4_POLYCHLOROSTYRENE
  name = G4_POLYCHLOROSTYRENE
  specific = 4
FEATURE [App::DocumentObjectGroupPython] C_element081  label="C_element : 039"  # scripted group (container) (typed FeaturePython)
  n = 1
  ref = C_element
FEATURE [App::DocumentObjectGroupPython] H_element075  label="H_element : 037"  # scripted group (container) (typed FeaturePython)
  n = 2
  ref = H_element
FEATURE [App::DocumentObjectGroupPython] G4_POLYETHYLENE  # scripted group (container) (typed FeaturePython)
  Dunit = g/cm3
  Dvalue = 0.94
  Group = -> [C_element081,H_element075]
  conduct = 2
  density = 1
  expand = 3
  formula = G4_POLYETHYLENE
  name = G4_POLYETHYLENE
  specific = 4
FEATURE [App::DocumentObjectGroupPython] C_element082  label="C_element : 040"  # scripted group (container) (typed FeaturePython)
  n = 10
  ref = C_element
FEATURE [App::DocumentObjectGroupPython] H_element076  label="H_element : 038"  # scripted group (container) (typed FeaturePython)
  n = 8
  ref = H_element
FEATURE [App::DocumentObjectGroupPython] O_element078  label="O_element : 039"  # scripted group (container) (typed FeaturePython)
  n = 4
  ref = O_element
FEATURE [App::DocumentObjectGroupPython] G4_MYLAR  # scripted group (container) (typed FeaturePython)
  Dunit = g/cm3
  Dvalue = 1.4
  Group = -> [C_element082,H_element076,O_element078]
  conduct = 2
  density = 1
  expand = 3
  formula = G4_MYLAR
  name = G4_MYLAR
  specific = 4
FEATURE [App::DocumentObjectGroupPython] C_element083  label="C_element : 041"  # scripted group (container) (typed FeaturePython)
  n = 5
  ref = C_element
FEATURE [App::DocumentObjectGroupPython] H_element077  label="H_element : 039"  # scripted group (container) (typed FeaturePython)
  n = 8
  ref = H_element
FEATURE [App::DocumentObjectGroupPython] O_element079  label="O_element : 040"  # scripted group (container) (typed FeaturePython)
  n = 2
  ref = O_element
FEATURE [App::DocumentObjectGroupPython] G4_PLEXIGLASS  # scripted group (container) (typed FeaturePython)
  Dunit = g/cm3
  Dvalue = 1.19
  Group = -> [C_element083,H_element077,O_element079]
  conduct = 2
  density = 1
  expand = 3
  formula = G4_PLEXIGLASS
  name = G4_PLEXIGLASS
  specific = 4
FEATURE [App::DocumentObjectGroupPython] C_element084  label="C_element : 042"  # scripted group (container) (typed FeaturePython)
  n = 1
  ref = C_element
FEATURE [App::DocumentObjectGroupPython] H_element078  label="H_element : 040"  # scripted group (container) (typed FeaturePython)
  n = 2
  ref = H_element
FEATURE [App::DocumentObjectGroupPython] O_element080  label="O_element : 041"  # scripted group (container) (typed FeaturePython)
  n = 1
  ref = O_element
FEATURE [App::DocumentObjectGroupPython] G4_POLYOXYMETHYLENE  # scripted group (container) (typed FeaturePython)
  Dunit = g/cm3
  Dvalue = 1.425
  Group = -> [C_element084,H_element078,O_element080]
  conduct = 2
  density = 1
  expand = 3
  formula = G4_POLYOXYMETHYLENE
  name = G4_POLYOXYMETHYLENE
  specific = 4
FEATURE [App::DocumentObjectGroupPython] C_element085  label="C_element : 043"  # scripted group (container) (typed FeaturePython)
  n = 2
  ref = C_element
FEATURE [App::DocumentObjectGroupPython] H_element079  label="H_element : 041"  # scripted group (container) (typed FeaturePython)
  n = 4
  ref = H_element
FEATURE [App::DocumentObjectGroupPython] G4_POLYPROPYLENE  # scripted group (container) (typed FeaturePython)
  Dunit = g/cm3
  Dvalue = 0.9
  Group = -> [C_element085,H_element079]
  conduct = 2
  density = 1
  expand = 3
  formula = G4_POLYPROPYLENE
  name = G4_POLYPROPYLENE
  specific = 4
FEATURE [App::DocumentObjectGroupPython] C_element086  label="C_element : 044"  # scripted group (container) (typed FeaturePython)
  n = 8
  ref = C_element
FEATURE [App::DocumentObjectGroupPython] H_element080  label="H_element : 042"  # scripted group (container) (typed FeaturePython)
  n = 8
  ref = H_element
FEATURE [App::DocumentObjectGroupPython] G4_POLYSTYRENE  # scripted group (container) (typed FeaturePython)
  Dunit = g/cm3
  Dvalue = 1.06
  Group = -> [C_element086,H_element080]
  conduct = 2
  density = 1
  expand = 3
  formula = G4_POLYSTYRENE
  name = G4_POLYSTYRENE
  specific = 4
FEATURE [App::DocumentObjectGroupPython] C_element087  label="C_element : 045"  # scripted group (container) (typed FeaturePython)
  n = 2
  ref = C_element
FEATURE [App::DocumentObjectGroupPython] F_element014  label="F_element : 4"  # scripted group (container) (typed FeaturePython)
  n = 4
  ref = F_element
FEATURE [App::DocumentObjectGroupPython] G4_TEFLON  # scripted group (container) (typed FeaturePython)
  Dunit = g/cm3
  Dvalue = 2.2
  Group = -> [C_element087,F_element014]
  conduct = 2
  density = 1
  expand = 3
  formula = G4_TEFLON
  name = G4_TEFLON
  specific = 4
FEATURE [App::DocumentObjectGroupPython] C_element088  label="C_element : 046"  # scripted group (container) (typed FeaturePython)
  n = 2
  ref = C_element
FEATURE [App::DocumentObjectGroupPython] F_element015  label="F_element : 006"  # scripted group (container) (typed FeaturePython)
  n = 3
  ref = F_element
FEATURE [App::DocumentObjectGroupPython] Cl_element018  label="Cl_element : 008"  # scripted group (container) (typed FeaturePython)
  n = 1
  ref = Cl_element
FEATURE [App::DocumentObjectGroupPython] G4_POLYTRIFLUOROCHLOROETHYLENE  # scripted group (container) (typed FeaturePython)
  Dunit = g/cm3
  Dvalue = 2.1
  Group = -> [C_element088,F_element015,Cl_element018]
  conduct = 2
  density = 1
  expand = 3
  formula = G4_POLYTRIFLUOROCHLOROETHYLENE
  name = G4_POLYTRIFLUOROCHLOROETHYLENE
  specific = 4
FEATURE [App::DocumentObjectGroupPython] C_element089  label="C_element : 047"  # scripted group (container) (typed FeaturePython)
  n = 4
  ref = C_element
FEATURE [App::DocumentObjectGroupPython] H_element081  label="H_element : 043"  # scripted group (container) (typed FeaturePython)
  n = 6
  ref = H_element
FEATURE [App::DocumentObjectGroupPython] O_element081  label="O_element : 042"  # scripted group (container) (typed FeaturePython)
  n = 2
  ref = O_element
FEATURE [App::DocumentObjectGroupPython] G4_POLYVINYL_ACETATE  # scripted group (container) (typed FeaturePython)
  Dunit = g/cm3
  Dvalue = 1.19
  Group = -> [C_element089,H_element081,O_element081]
  conduct = 2
  density = 1
  expand = 3
  formula = G4_POLYVINYL_ACETATE
  name = G4_POLYVINYL_ACETATE
  specific = 4
FEATURE [App::DocumentObjectGroupPython] C_element090  label="C_element : 048"  # scripted group (container) (typed FeaturePython)
  n = 2
  ref = C_element
FEATURE [App::DocumentObjectGroupPython] H_element082  label="H_element : 044"  # scripted group (container) (typed FeaturePython)
  n = 4
  ref = H_element
FEATURE [App::DocumentObjectGroupPython] O_element082  label="O_element : 043"  # scripted group (container) (typed FeaturePython)
  n = 1
  ref = O_element
FEATURE [App::DocumentObjectGroupPython] G4_POLYVINYL_ALCOHOL  # scripted group (container) (typed FeaturePython)
  Dunit = g/cm3
  Dvalue = 1.3
  Group = -> [C_element090,H_element082,O_element082]
  conduct = 2
  density = 1
  expand = 3
  formula = G4_POLYVINYL_ALCOHOL
  name = G4_POLYVINYL_ALCOHOL
  specific = 4
FEATURE [App::DocumentObjectGroupPython] C_element091  label="C_element : 049"  # scripted group (container) (typed FeaturePython)
  n = 8
  ref = C_element
FEATURE [App::DocumentObjectGroupPython] H_element083  label="H_element : 045"  # scripted group (container) (typed FeaturePython)
  n = 14
  ref = H_element
FEATURE [App::DocumentObjectGroupPython] O_element083  label="O_element : 044"  # scripted group (container) (typed FeaturePython)
  n = 2
  ref = O_element
FEATURE [App::DocumentObjectGroupPython] G4_POLYVINYL_BUTYRAL  # scripted group (container) (typed FeaturePython)
  Dunit = g/cm3
  Dvalue = 1.12
  Group = -> [C_element091,H_element083,O_element083]
  conduct = 2
  density = 1
  expand = 3
  formula = G4_POLYVINYL_BUTYRAL
  name = G4_POLYVINYL_BUTYRAL
  specific = 4
FEATURE [App::DocumentObjectGroupPython] C_element092  label="C_element : 050"  # scripted group (container) (typed FeaturePython)
  n = 2
  ref = C_element
FEATURE [App::DocumentObjectGroupPython] H_element084  label="H_element : 046"  # scripted group (container) (typed FeaturePython)
  n = 3
  ref = H_element
FEATURE [App::DocumentObjectGroupPython] Cl_element019  label="Cl_element : 009"  # scripted group (container) (typed FeaturePython)
  n = 1
  ref = Cl_element
FEATURE [App::DocumentObjectGroupPython] G4_POLYVINYL_CHLORIDE  # scripted group (container) (typed FeaturePython)
  Dunit = g/cm3
  Dvalue = 1.3
  Group = -> [C_element092,H_element084,Cl_element019]
  conduct = 2
  density = 1
  expand = 3
  formula = G4_POLYVINYL_CHLORIDE
  name = G4_POLYVINYL_CHLORIDE
  specific = 4
FEATURE [App::DocumentObjectGroupPython] C_element093  label="C_element : 051"  # scripted group (container) (typed FeaturePython)
  n = 2
  ref = C_element
FEATURE [App::DocumentObjectGroupPython] H_element085  label="H_element : 047"  # scripted group (container) (typed FeaturePython)
  n = 2
  ref = H_element
FEATURE [App::DocumentObjectGroupPython] Cl_element020  label="Cl_element : 010"  # scripted group (container) (typed FeaturePython)
  n = 2
  ref = Cl_element
FEATURE [App::DocumentObjectGroupPython] G4_POLYVINYLIDENE_CHLORIDE  # scripted group (container) (typed FeaturePython)
  Dunit = g/cm3
  Dvalue = 1.7
  Group = -> [C_element093,H_element085,Cl_element020]
  conduct = 2
  density = 1
  expand = 3
  formula = G4_POLYVINYLIDENE_CHLORIDE
  name = G4_POLYVINYLIDENE_CHLORIDE
  specific = 4
FEATURE [App::DocumentObjectGroupPython] C_element094  label="C_element : 052"  # scripted group (container) (typed FeaturePython)
  n = 2
  ref = C_element
FEATURE [App::DocumentObjectGroupPython] H_element086  label="H_element : 048"  # scripted group (container) (typed FeaturePython)
  n = 2
  ref = H_element
FEATURE [App::DocumentObjectGroupPython] F_element016  label="F_element : 007"  # scripted group (container) (typed FeaturePython)
  n = 2
  ref = F_element
FEATURE [App::DocumentObjectGroupPython] G4_POLYVINYLIDENE_FLUORIDE  # scripted group (container) (typed FeaturePython)
  Dunit = g/cm3
  Dvalue = 1.76
  Group = -> [C_element094,H_element086,F_element016]
  conduct = 2
  density = 1
  expand = 3
  formula = G4_POLYVINYLIDENE_FLUORIDE
  name = G4_POLYVINYLIDENE_FLUORIDE
  specific = 4
FEATURE [App::DocumentObjectGroupPython] C_element095  label="C_element : 053"  # scripted group (container) (typed FeaturePython)
  n = 6
  ref = C_element
FEATURE [App::DocumentObjectGroupPython] H_element087  label="H_element : 9"  # scripted group (container) (typed FeaturePython)
  n = 9
  ref = H_element
FEATURE [App::DocumentObjectGroupPython] N_element037  label="N_element : 016"  # scripted group (container) (typed FeaturePython)
  n = 1
  ref = N_element
FEATURE [App::DocumentObjectGroupPython] O_element084  label="O_element : 045"  # scripted group (container) (typed FeaturePython)
  n = 1
  ref = O_element
FEATURE [App::DocumentObjectGroupPython] G4_POLYVINYL_PYRROLIDONE  # scripted group (container) (typed FeaturePython)
  Dunit = g/cm3
  Dvalue = 1.25
  Group = -> [C_element095,H_element087,N_element037,O_element084]
  conduct = 2
  density = 1
  expand = 3
  formula = G4_POLYVINYL_PYRROLIDONE
  name = G4_POLYVINYL_PYRROLIDONE
  specific = 4
FEATURE [App::DocumentObjectGroupPython] K_element008  label="K_element : 1"  # scripted group (container) (typed FeaturePython)
  n = 1
  ref = K_element
FEATURE [App::DocumentObjectGroupPython] I_element006  label="I_element : 003"  # scripted group (container) (typed FeaturePython)
  n = 1
  ref = I_element
FEATURE [App::DocumentObjectGroupPython] G4_POTASSIUM_IODIDE  # scripted group (container) (typed FeaturePython)
  Dunit = g/cm3
  Dvalue = 3.13
  Group = -> [K_element008,I_element006]
  conduct = 2
  density = 1
  expand = 3
  formula = G4_POTASSIUM_IODIDE
  name = G4_POTASSIUM_IODIDE
  specific = 4
FEATURE [App::DocumentObjectGroupPython] K_element009  label="K_element : 2"  # scripted group (container) (typed FeaturePython)
  n = 2
  ref = K_element
FEATURE [App::DocumentObjectGroupPython] O_element085  label="O_element : 046"  # scripted group (container) (typed FeaturePython)
  n = 1
  ref = O_element
FEATURE [App::DocumentObjectGroupPython] G4_POTASSIUM_OXIDE  # scripted group (container) (typed FeaturePython)
  Dunit = g/cm3
  Dvalue = 2.32
  Group = -> [K_element009,O_element085]
  conduct = 2
  density = 1
  expand = 3
  formula = G4_POTASSIUM_OXIDE
  name = G4_POTASSIUM_OXIDE
  specific = 4
FEATURE [App::DocumentObjectGroupPython] C_element096  label="C_element : 054"  # scripted group (container) (typed FeaturePython)
  n = 3
  ref = C_element
FEATURE [App::DocumentObjectGroupPython] H_element088  label="H_element : 049"  # scripted group (container) (typed FeaturePython)
  n = 8
  ref = H_element
FEATURE [App::DocumentObjectGroupPython] G4_PROPANE  # scripted group (container) (typed FeaturePython)
  Dunit = g/cm3
  Dvalue = 0.00187939
  Group = -> [C_element096,H_element088]
  conduct = 2
  density = 1
  expand = 3
  formula = G4_PROPANE
  name = G4_PROPANE
  specific = 4
FEATURE [App::DocumentObjectGroupPython] C_element097  label="C_element : 055"  # scripted group (container) (typed FeaturePython)
  n = 3
  ref = C_element
FEATURE [App::DocumentObjectGroupPython] H_element089  label="H_element : 050"  # scripted group (container) (typed FeaturePython)
  n = 8
  ref = H_element
FEATURE [App::DocumentObjectGroupPython] G4_lPROPANE  # scripted group (container) (typed FeaturePython)
  Dunit = g/cm3
  Dvalue = 0.43
  Group = -> [C_element097,H_element089]
  conduct = 2
  density = 1
  expand = 3
  formula = G4_lPROPANE
  name = G4_lPROPANE
  specific = 4
FEATURE [App::DocumentObjectGroupPython] C_element098  label="C_element : 056"  # scripted group (container) (typed FeaturePython)
  n = 3
  ref = C_element
FEATURE [App::DocumentObjectGroupPython] H_element090  label="H_element : 051"  # scripted group (container) (typed FeaturePython)
  n = 8
  ref = H_element
FEATURE [App::DocumentObjectGroupPython] O_element086  label="O_element : 047"  # scripted group (container) (typed FeaturePython)
  n = 1
  ref = O_element
FEATURE [App::DocumentObjectGroupPython] G4_N_PROPYL_ALCOHOL  label="G4_N-PROPYL_ALCOHOL"  # scripted group (container) (typed FeaturePython)
  Dunit = g/cm3
  Dvalue = 0.8035
  Group = -> [C_element098,H_element090,O_element086]
  conduct = 2
  density = 1
  expand = 3
  formula = G4_N-PROPYL_ALCOHOL
  name = G4_N-PROPYL_ALCOHOL
  specific = 4
FEATURE [App::DocumentObjectGroupPython] C_element099  label="C_element : 057"  # scripted group (container) (typed FeaturePython)
  n = 5
  ref = C_element
FEATURE [App::DocumentObjectGroupPython] H_element091  label="H_element : 052"  # scripted group (container) (typed FeaturePython)
  n = 5
  ref = H_element
FEATURE [App::DocumentObjectGroupPython] N_element038  label="N_element : 017"  # scripted group (container) (typed FeaturePython)
  n = 1
  ref = N_element
FEATURE [App::DocumentObjectGroupPython] G4_PYRIDINE  # scripted group (container) (typed FeaturePython)
  Dunit = g/cm3
  Dvalue = 0.9819
  Group = -> [C_element099,H_element091,N_element038]
  conduct = 2
  density = 1
  expand = 3
  formula = G4_PYRIDINE
  name = G4_PYRIDINE
  specific = 4
FEATURE [App::DocumentObjectGroupPython] H_element092  label="H_element : 0.144"  # scripted group (container) (typed FeaturePython)
  n = 0.143711
FEATURE [App::DocumentObjectGroupPython] C_element100  label="C_element : 0.856"  # scripted group (container) (typed FeaturePython)
  n = 0.856289
FEATURE [App::DocumentObjectGroupPython] G4_RUBBER_BUTYL  # scripted group (container) (typed FeaturePython)
  Dunit = g/cm3
  Dvalue = 0.92
  Group = -> [H_element092,C_element100]
  conduct = 2
  density = 1
  expand = 3
  formula = G4_RUBBER_BUTYL
  name = G4_RUBBER_BUTYL
  specific = 4
FEATURE [App::DocumentObjectGroupPython] H_element093  label="H_element : 0.118"  # scripted group (container) (typed FeaturePython)
  n = 0.118371
FEATURE [App::DocumentObjectGroupPython] C_element101  label="C_element : 0.882"  # scripted group (container) (typed FeaturePython)
  n = 0.881629
FEATURE [App::DocumentObjectGroupPython] G4_RUBBER_NATURAL  # scripted group (container) (typed FeaturePython)
  Dunit = g/cm3
  Dvalue = 0.92
  Group = -> [H_element093,C_element101]
  conduct = 2
  density = 1
  expand = 3
  formula = G4_RUBBER_NATURAL
  name = G4_RUBBER_NATURAL
  specific = 4
FEATURE [App::DocumentObjectGroupPython] H_element094  label="H_element : 0.145"  # scripted group (container) (typed FeaturePython)
  n = 0.05692
FEATURE [App::DocumentObjectGroupPython] C_element102  label="C_element : 0.543"  # scripted group (container) (typed FeaturePython)
  n = 0.542646
FEATURE [App::DocumentObjectGroupPython] Cl_element021  label="Cl_element : 0.400"  # scripted group (container) (typed FeaturePython)
  n = 0.400434
FEATURE [App::DocumentObjectGroupPython] G4_RUBBER_NEOPRENE  # scripted group (container) (typed FeaturePython)
  Dunit = g/cm3
  Dvalue = 1.23
  Group = -> [H_element094,C_element102,Cl_element021]
  conduct = 2
  density = 1
  expand = 3
  formula = G4_RUBBER_NEOPRENE
  name = G4_RUBBER_NEOPRENE
  specific = 4
FEATURE [App::DocumentObjectGroupPython] Si_element006  label="Si_element : 1"  # scripted group (container) (typed FeaturePython)
  n = 1
  ref = Si_element
FEATURE [App::DocumentObjectGroupPython] O_element087  label="O_element : 048"  # scripted group (container) (typed FeaturePython)
  n = 2
  ref = O_element
FEATURE [App::DocumentObjectGroupPython] G4_SILICON_DIOXIDE  # scripted group (container) (typed FeaturePython)
  Dunit = g/cm3
  Dvalue = 2.32
  Group = -> [Si_element006,O_element087]
  conduct = 2
  density = 1
  expand = 3
  formula = G4_SILICON_DIOXIDE
  name = G4_SILICON_DIOXIDE
  specific = 4
FEATURE [App::DocumentObjectGroupPython] Ag_element002  label="Ag_element : 1"  # scripted group (container) (typed FeaturePython)
  n = 1
  ref = Ag_element
FEATURE [App::DocumentObjectGroupPython] Br_element005  label="Br_element : 003"  # scripted group (container) (typed FeaturePython)
  n = 1
  ref = Br_element
FEATURE [App::DocumentObjectGroupPython] G4_SILVER_BROMIDE  # scripted group (container) (typed FeaturePython)
  Dunit = g/cm3
  Dvalue = 6.473
  Group = -> [Ag_element002,Br_element005]
  conduct = 2
  density = 1
  expand = 3
  formula = G4_SILVER_BROMIDE
  name = G4_SILVER_BROMIDE
  specific = 4
FEATURE [App::DocumentObjectGroupPython] Ag_element003  label="Ag_element : 002"  # scripted group (container) (typed FeaturePython)
  n = 1
  ref = Ag_element
FEATURE [App::DocumentObjectGroupPython] Cl_element022  label="Cl_element : 011"  # scripted group (container) (typed FeaturePython)
  n = 1
  ref = Cl_element
FEATURE [App::DocumentObjectGroupPython] G4_SILVER_CHLORIDE  # scripted group (container) (typed FeaturePython)
  Dunit = g/cm3
  Dvalue = 5.56
  Group = -> [Ag_element003,Cl_element022]
  conduct = 2
  density = 1
  expand = 3
  formula = G4_SILVER_CHLORIDE
  name = G4_SILVER_CHLORIDE
  specific = 4
FEATURE [App::DocumentObjectGroupPython] Br_element006  label="Br_element : 0.423"  # scripted group (container) (typed FeaturePython)
  n = 0.422895
FEATURE [App::DocumentObjectGroupPython] Ag_element004  label="Ag_element : 0.574"  # scripted group (container) (typed FeaturePython)
  n = 0.573748
FEATURE [App::DocumentObjectGroupPython] I_element007  label="I_element : 0.649"  # scripted group (container) (typed FeaturePython)
  n = 0.003357
FEATURE [App::DocumentObjectGroupPython] G4_SILVER_HALIDES  # scripted group (container) (typed FeaturePython)
  Dunit = g/cm3
  Dvalue = 6.47
  Group = -> [Br_element006,Ag_element004,I_element007]
  conduct = 2
  density = 1
  expand = 3
  formula = G4_SILVER_HALIDES
  name = G4_SILVER_HALIDES
  specific = 4
FEATURE [App::DocumentObjectGroupPython] Ag_element005  label="Ag_element : 003"  # scripted group (container) (typed FeaturePython)
  n = 1
  ref = Ag_element
FEATURE [App::DocumentObjectGroupPython] I_element008  label="I_element : 004"  # scripted group (container) (typed FeaturePython)
  n = 1
  ref = I_element
FEATURE [App::DocumentObjectGroupPython] G4_SILVER_IODIDE  # scripted group (container) (typed FeaturePython)
  Dunit = g/cm3
  Dvalue = 6.01
  Group = -> [Ag_element005,I_element008]
  conduct = 2
  density = 1
  expand = 3
  formula = G4_SILVER_IODIDE
  name = G4_SILVER_IODIDE
  specific = 4
FEATURE [App::DocumentObjectGroupPython] H_element095  label="H_element : 0.100"  # scripted group (container) (typed FeaturePython)
  n = 0.1
FEATURE [App::DocumentObjectGroupPython] C_element103  label="C_element : 0.204"  # scripted group (container) (typed FeaturePython)
  n = 0.204
FEATURE [App::DocumentObjectGroupPython] N_element039  label="N_element : 0.759"  # scripted group (container) (typed FeaturePython)
  n = 0.042
FEATURE [App::DocumentObjectGroupPython] O_element088  label="O_element : 0.645"  # scripted group (container) (typed FeaturePython)
  n = 0.645
FEATURE [App::DocumentObjectGroupPython] Na_element013  label="Na_element : 0.100"  # scripted group (container) (typed FeaturePython)
  n = 0.002
FEATURE [App::DocumentObjectGroupPython] P_element009  label="P_element : 0.107"  # scripted group (container) (typed FeaturePython)
  n = 0.001
FEATURE [App::DocumentObjectGroupPython] S_element020  label="S_element : 0.021"  # scripted group (container) (typed FeaturePython)
  n = 0.002
FEATURE [App::DocumentObjectGroupPython] Cl_element023  label="Cl_element : 0.590"  # scripted group (container) (typed FeaturePython)
  n = 0.003
FEATURE [App::DocumentObjectGroupPython] K_element010  label="K_element : 0.001"  # scripted group (container) (typed FeaturePython)
  n = 0.001
FEATURE [App::DocumentObjectGroupPython] G4_SKIN_ICRP  # scripted group (container) (typed FeaturePython)
  Dunit = g/cm3
  Dvalue = 1.09
  Group = -> [H_element095,C_element103,N_element039,O_element088,Na_element013,P_element009,S_element020,Cl_element023,K_element010]
  conduct = 2
  density = 1
  expand = 3
  formula = G4_SKIN_ICRP
  name = G4_SKIN_ICRP
  specific = 4
FEATURE [App::DocumentObjectGroupPython] Na_element014  label="Na_element : 2"  # scripted group (container) (typed FeaturePython)
  n = 2
  ref = Na_element
FEATURE [App::DocumentObjectGroupPython] C_element104  label="C_element : 058"  # scripted group (container) (typed FeaturePython)
  n = 1
  ref = C_element
FEATURE [App::DocumentObjectGroupPython] O_element089  label="O_element : 049"  # scripted group (container) (typed FeaturePython)
  n = 3
  ref = O_element
FEATURE [App::DocumentObjectGroupPython] G4_SODIUM_CARBONATE  # scripted group (container) (typed FeaturePython)
  Dunit = g/cm3
  Dvalue = 2.532
  Group = -> [Na_element014,C_element104,O_element089]
  conduct = 2
  density = 1
  expand = 3
  formula = G4_SODIUM_CARBONATE
  name = G4_SODIUM_CARBONATE
  specific = 4
FEATURE [App::DocumentObjectGroupPython] Na_element015  label="Na_element : 1"  # scripted group (container) (typed FeaturePython)
  n = 1
  ref = Na_element
FEATURE [App::DocumentObjectGroupPython] I_element009  label="I_element : 005"  # scripted group (container) (typed FeaturePython)
  n = 1
  ref = I_element
FEATURE [App::DocumentObjectGroupPython] G4_SODIUM_IODIDE  # scripted group (container) (typed FeaturePython)
  Dunit = g/cm3
  Dvalue = 3.667
  Group = -> [Na_element015,I_element009]
  conduct = 2
  density = 1
  expand = 3
  formula = G4_SODIUM_IODIDE
  name = G4_SODIUM_IODIDE
  specific = 4
FEATURE [App::DocumentObjectGroupPython] Na_element016  label="Na_element : 003"  # scripted group (container) (typed FeaturePython)
  n = 2
  ref = Na_element
FEATURE [App::DocumentObjectGroupPython] O_element090  label="O_element : 050"  # scripted group (container) (typed FeaturePython)
  n = 1
  ref = O_element
FEATURE [App::DocumentObjectGroupPython] G4_SODIUM_MONOXIDE  # scripted group (container) (typed FeaturePython)
  Dunit = g/cm3
  Dvalue = 2.27
  Group = -> [Na_element016,O_element090]
  conduct = 2
  density = 1
  expand = 3
  formula = G4_SODIUM_MONOXIDE
  name = G4_SODIUM_MONOXIDE
  specific = 4
FEATURE [App::DocumentObjectGroupPython] Na_element017  label="Na_element : 004"  # scripted group (container) (typed FeaturePython)
  n = 1
  ref = Na_element
FEATURE [App::DocumentObjectGroupPython] N_element040  label="N_element : 018"  # scripted group (container) (typed FeaturePython)
  n = 1
  ref = N_element
FEATURE [App::DocumentObjectGroupPython] O_element091  label="O_element : 051"  # scripted group (container) (typed FeaturePython)
  n = 3
  ref = O_element
FEATURE [App::DocumentObjectGroupPython] G4_SODIUM_NITRATE  # scripted group (container) (typed FeaturePython)
  Dunit = g/cm3
  Dvalue = 2.261
  Group = -> [Na_element017,N_element040,O_element091]
  conduct = 2
  density = 1
  expand = 3
  formula = G4_SODIUM_NITRATE
  name = G4_SODIUM_NITRATE
  specific = 4
FEATURE [App::DocumentObjectGroupPython] C_element105  label="C_element : 059"  # scripted group (container) (typed FeaturePython)
  n = 14
  ref = C_element
FEATURE [App::DocumentObjectGroupPython] H_element096  label="H_element : 053"  # scripted group (container) (typed FeaturePython)
  n = 12
  ref = H_element
FEATURE [App::DocumentObjectGroupPython] G4_STILBENE  # scripted group (container) (typed FeaturePython)
  Dunit = g/cm3
  Dvalue = 0.9707
  Group = -> [C_element105,H_element096]
  conduct = 2
  density = 1
  expand = 3
  formula = G4_STILBENE
  name = G4_STILBENE
  specific = 4
FEATURE [App::DocumentObjectGroupPython] C_element106  label="C_element : 12"  # scripted group (container) (typed FeaturePython)
  n = 12
  ref = C_element
FEATURE [App::DocumentObjectGroupPython] H_element097  label="H_element : 22"  # scripted group (container) (typed FeaturePython)
  n = 22
  ref = H_element
FEATURE [App::DocumentObjectGroupPython] O_element092  label="O_element : 11"  # scripted group (container) (typed FeaturePython)
  n = 11
  ref = O_element
FEATURE [App::DocumentObjectGroupPython] G4_SUCROSE  # scripted group (container) (typed FeaturePython)
  Dunit = g/cm3
  Dvalue = 1.5805
  Group = -> [C_element106,H_element097,O_element092]
  conduct = 2
  density = 1
  expand = 3
  formula = G4_SUCROSE
  name = G4_SUCROSE
  specific = 4
FEATURE [App::DocumentObjectGroupPython] C_element107  label="C_element : 18"  # scripted group (container) (typed FeaturePython)
  n = 18
  ref = C_element
FEATURE [App::DocumentObjectGroupPython] H_element098  label="H_element : 054"  # scripted group (container) (typed FeaturePython)
  n = 14
  ref = H_element
FEATURE [App::DocumentObjectGroupPython] G4_TERPHENYL  # scripted group (container) (typed FeaturePython)
  Dunit = g/cm3
  Dvalue = 1.24
  Group = -> [C_element107,H_element098]
  conduct = 2
  density = 1
  expand = 3
  formula = G4_TERPHENYL
  name = G4_TERPHENYL
  specific = 4
FEATURE [App::DocumentObjectGroupPython] H_element099  label="H_element : 0.146"  # scripted group (container) (typed FeaturePython)
  n = 0.106
FEATURE [App::DocumentObjectGroupPython] C_element108  label="C_element : 0.883"  # scripted group (container) (typed FeaturePython)
  n = 0.099
FEATURE [App::DocumentObjectGroupPython] N_element041  label="N_element : 0.020"  # scripted group (container) (typed FeaturePython)
  n = 0.02
FEATURE [App::DocumentObjectGroupPython] O_element093  label="O_element : 0.766"  # scripted group (container) (typed FeaturePython)
  n = 0.766
FEATURE [App::DocumentObjectGroupPython] Na_element018  label="Na_element : 0.101"  # scripted group (container) (typed FeaturePython)
  n = 0.002
FEATURE [App::DocumentObjectGroupPython] P_element010  label="P_element : 0.108"  # scripted group (container) (typed FeaturePython)
  n = 0.001
FEATURE [App::DocumentObjectGroupPython] S_element021  label="S_element : 0.022"  # scripted group (container) (typed FeaturePython)
  n = 0.002
FEATURE [App::DocumentObjectGroupPython] Cl_element024  label="Cl_element : 0.002"  # scripted group (container) (typed FeaturePython)
  n = 0.002
FEATURE [App::DocumentObjectGroupPython] K_element011  label="K_element : 0.017"  # scripted group (container) (typed FeaturePython)
  n = 0.002
FEATURE [App::DocumentObjectGroupPython] G4_TESTIS_ICRP  # scripted group (container) (typed FeaturePython)
  Dunit = g/cm3
  Dvalue = 1.04
  Group = -> [H_element099,C_element108,N_element041,O_element093,Na_element018,P_element010,S_element021,Cl_element024,K_element011]
  conduct = 2
  density = 1
  expand = 3
  formula = G4_TESTIS_ICRP
  name = G4_TESTIS_ICRP
  specific = 4
FEATURE [App::DocumentObjectGroupPython] C_element109  label="C_element : 060"  # scripted group (container) (typed FeaturePython)
  n = 2
  ref = C_element
FEATURE [App::DocumentObjectGroupPython] Cl_element025  label="Cl_element : 012"  # scripted group (container) (typed FeaturePython)
  n = 4
  ref = Cl_element
FEATURE [App::DocumentObjectGroupPython] G4_TETRACHLOROETHYLENE  # scripted group (container) (typed FeaturePython)
  Dunit = g/cm3
  Dvalue = 1.625
  Group = -> [C_element109,Cl_element025]
  conduct = 2
  density = 1
  expand = 3
  formula = G4_TETRACHLOROETHYLENE
  name = G4_TETRACHLOROETHYLENE
  specific = 4
FEATURE [App::DocumentObjectGroupPython] Tl_element001  label="Tl_element : 1"  # scripted group (container) (typed FeaturePython)
  n = 1
  ref = Tl_element
FEATURE [App::DocumentObjectGroupPython] Cl_element026  label="Cl_element : 013"  # scripted group (container) (typed FeaturePython)
  n = 1
  ref = Cl_element
FEATURE [App::DocumentObjectGroupPython] G4_THALLIUM_CHLORIDE  # scripted group (container) (typed FeaturePython)
  Dunit = g/cm3
  Dvalue = 7.004
  Group = -> [Tl_element001,Cl_element026]
  conduct = 2
  density = 1
  expand = 3
  formula = G4_THALLIUM_CHLORIDE
  name = G4_THALLIUM_CHLORIDE
  specific = 4
FEATURE [App::DocumentObjectGroupPython] H_element100  label="H_element : 0.147"  # scripted group (container) (typed FeaturePython)
  n = 0.105
FEATURE [App::DocumentObjectGroupPython] C_element110  label="C_element : 0.256"  # scripted group (container) (typed FeaturePython)
  n = 0.256
FEATURE [App::DocumentObjectGroupPython] N_element042  label="N_element : 0.760"  # scripted group (container) (typed FeaturePython)
  n = 0.027
FEATURE [App::DocumentObjectGroupPython] O_element094  label="O_element : 0.602"  # scripted group (container) (typed FeaturePython)
  n = 0.602
FEATURE [App::DocumentObjectGroupPython] Na_element019  label="Na_element : 0.102"  # scripted group (container) (typed FeaturePython)
  n = 0.001
FEATURE [App::DocumentObjectGroupPython] P_element011  label="P_element : 0.109"  # scripted group (container) (typed FeaturePython)
  n = 0.002
FEATURE [App::DocumentObjectGroupPython] S_element022  label="S_element : 0.023"  # scripted group (container) (typed FeaturePython)
  n = 0.003
FEATURE [App::DocumentObjectGroupPython] Cl_element027  label="Cl_element : 0.591"  # scripted group (container) (typed FeaturePython)
  n = 0.002
FEATURE [App::DocumentObjectGroupPython] K_element012  label="K_element : 0.018"  # scripted group (container) (typed FeaturePython)
  n = 0.002
FEATURE [App::DocumentObjectGroupPython] G4_TISSUE_SOFT_ICRP  # scripted group (container) (typed FeaturePython)
  Dunit = g/cm3
  Dvalue = 1.03
  Group = -> [H_element100,C_element110,N_element042,O_element094,Na_element019,P_element011,S_element022,Cl_element027,K_element012]
  conduct = 2
  density = 1
  expand = 3
  formula = G4_TISSUE_SOFT_ICRP
  name = G4_TISSUE_SOFT_ICRP
  specific = 4
FEATURE [App::DocumentObjectGroupPython] H_element101  label="H_element : 0.148"  # scripted group (container) (typed FeaturePython)
  n = 0.101
FEATURE [App::DocumentObjectGroupPython] C_element111  label="C_element : 0.111"  # scripted group (container) (typed FeaturePython)
  n = 0.111
FEATURE [App::DocumentObjectGroupPython] N_element043  label="N_element : 0.026"  # scripted group (container) (typed FeaturePython)
  n = 0.026
FEATURE [App::DocumentObjectGroupPython] O_element095  label="O_element : 0.762"  # scripted group (container) (typed FeaturePython)
  n = 0.762
FEATURE [App::DocumentObjectGroupPython] G4_TISSUE_SOFT_ICRU_4  label="G4_TISSUE_SOFT_ICRU-4"  # scripted group (container) (typed FeaturePython)
  Dunit = g/cm3
  Dvalue = 1
  Group = -> [H_element101,C_element111,N_element043,O_element095]
  conduct = 2
  density = 1
  expand = 3
  formula = G4_TISSUE_SOFT_ICRU-4
  name = G4_TISSUE_SOFT_ICRU-4
  specific = 4
FEATURE [App::DocumentObjectGroupPython] H_element102  label="H_element : 0.149"  # scripted group (container) (typed FeaturePython)
  n = 0.101869
FEATURE [App::DocumentObjectGroupPython] C_element112  label="C_element : 0.456"  # scripted group (container) (typed FeaturePython)
  n = 0.456179
FEATURE [App::DocumentObjectGroupPython] N_element044  label="N_element : 0.761"  # scripted group (container) (typed FeaturePython)
  n = 0.035172
FEATURE [App::DocumentObjectGroupPython] O_element096  label="O_element : 0.407"  # scripted group (container) (typed FeaturePython)
  n = 0.40678
FEATURE [App::DocumentObjectGroupPython] G4_TISSUE_METHANE  label="G4_TISSUE-METHANE"  # scripted group (container) (typed FeaturePython)
  Dunit = g/cm3
  Dvalue = 0.00106409
  Group = -> [H_element102,C_element112,N_element044,O_element096]
  conduct = 2
  density = 1
  expand = 3
  formula = G4_TISSUE-METHANE
  name = G4_TISSUE-METHANE
  specific = 4
FEATURE [App::DocumentObjectGroupPython] H_element103  label="H_element : 0.103"  # scripted group (container) (typed FeaturePython)
  n = 0.102672
FEATURE [App::DocumentObjectGroupPython] C_element113  label="C_element : 0.569"  # scripted group (container) (typed FeaturePython)
  n = 0.56894
FEATURE [App::DocumentObjectGroupPython] N_element045  label="N_element : 0.762"  # scripted group (container) (typed FeaturePython)
  n = 0.035022
FEATURE [App::DocumentObjectGroupPython] O_element097  label="O_element : 0.293"  # scripted group (container) (typed FeaturePython)
  n = 0.293366
FEATURE [App::DocumentObjectGroupPython] G4_TISSUE_PROPANE  label="G4_TISSUE-PROPANE"  # scripted group (container) (typed FeaturePython)
  Dunit = g/cm3
  Dvalue = 0.00182628
  Group = -> [H_element103,C_element113,N_element045,O_element097]
  conduct = 2
  density = 1
  expand = 3
  formula = G4_TISSUE-PROPANE
  name = G4_TISSUE-PROPANE
  specific = 4
FEATURE [App::DocumentObjectGroupPython] Ti_element003  label="Ti_element : 1"  # scripted group (container) (typed FeaturePython)
  n = 1
  ref = Ti_element
FEATURE [App::DocumentObjectGroupPython] O_element098  label="O_element : 052"  # scripted group (container) (typed FeaturePython)
  n = 2
  ref = O_element
FEATURE [App::DocumentObjectGroupPython] G4_TITANIUM_DIOXIDE  # scripted group (container) (typed FeaturePython)
  Dunit = g/cm3
  Dvalue = 4.26
  Group = -> [Ti_element003,O_element098]
  conduct = 2
  density = 1
  expand = 3
  formula = G4_TITANIUM_DIOXIDE
  name = G4_TITANIUM_DIOXIDE
  specific = 4
FEATURE [App::DocumentObjectGroupPython] C_element114  label="C_element : 061"  # scripted group (container) (typed FeaturePython)
  n = 7
  ref = C_element
FEATURE [App::DocumentObjectGroupPython] H_element104  label="H_element : 055"  # scripted group (container) (typed FeaturePython)
  n = 8
  ref = H_element
FEATURE [App::DocumentObjectGroupPython] G4_TOLUENE  # scripted group (container) (typed FeaturePython)
  Dunit = g/cm3
  Dvalue = 0.8669
  Group = -> [C_element114,H_element104]
  conduct = 2
  density = 1
  expand = 3
  formula = G4_TOLUENE
  name = G4_TOLUENE
  specific = 4
FEATURE [App::DocumentObjectGroupPython] C_element115  label="C_element : 062"  # scripted group (container) (typed FeaturePython)
  n = 2
  ref = C_element
FEATURE [App::DocumentObjectGroupPython] H_element105  label="H_element : 056"  # scripted group (container) (typed FeaturePython)
  n = 1
  ref = H_element
FEATURE [App::DocumentObjectGroupPython] Cl_element028  label="Cl_element : 014"  # scripted group (container) (typed FeaturePython)
  n = 3
  ref = Cl_element
FEATURE [App::DocumentObjectGroupPython] G4_TRICHLOROETHYLENE  # scripted group (container) (typed FeaturePython)
  Dunit = g/cm3
  Dvalue = 1.46
  Group = -> [C_element115,H_element105,Cl_element028]
  conduct = 2
  density = 1
  expand = 3
  formula = G4_TRICHLOROETHYLENE
  name = G4_TRICHLOROETHYLENE
  specific = 4
FEATURE [App::DocumentObjectGroupPython] C_element116  label="C_element : 063"  # scripted group (container) (typed FeaturePython)
  n = 6
  ref = C_element
FEATURE [App::DocumentObjectGroupPython] H_element106  label="H_element : 15"  # scripted group (container) (typed FeaturePython)
  n = 15
  ref = H_element
FEATURE [App::DocumentObjectGroupPython] O_element099  label="O_element : 053"  # scripted group (container) (typed FeaturePython)
  n = 4
  ref = O_element
FEATURE [App::DocumentObjectGroupPython] P_element012  label="P_element : 1"  # scripted group (container) (typed FeaturePython)
  n = 1
  ref = P_element
FEATURE [App::DocumentObjectGroupPython] G4_TRIETHYL_PHOSPHATE  # scripted group (container) (typed FeaturePython)
  Dunit = g/cm3
  Dvalue = 1.07
  Group = -> [C_element116,H_element106,O_element099,P_element012]
  conduct = 2
  density = 1
  expand = 3
  formula = G4_TRIETHYL_PHOSPHATE
  name = G4_TRIETHYL_PHOSPHATE
  specific = 4
FEATURE [App::DocumentObjectGroupPython] W_element003  label="W_element : 003"  # scripted group (container) (typed FeaturePython)
  n = 1
  ref = W_element
FEATURE [App::DocumentObjectGroupPython] F_element017  label="F_element : 6"  # scripted group (container) (typed FeaturePython)
  n = 6
  ref = F_element
FEATURE [App::DocumentObjectGroupPython] G4_TUNGSTEN_HEXAFLUORIDE  # scripted group (container) (typed FeaturePython)
  Dunit = g/cm3
  Dvalue = 2.4
  Group = -> [W_element003,F_element017]
  conduct = 2
  density = 1
  expand = 3
  formula = G4_TUNGSTEN_HEXAFLUORIDE
  name = G4_TUNGSTEN_HEXAFLUORIDE
  specific = 4
FEATURE [App::DocumentObjectGroupPython] U_element001  label="U_element : 1"  # scripted group (container) (typed FeaturePython)
  n = 1
  ref = U_element
FEATURE [App::DocumentObjectGroupPython] C_element117  label="C_element : 064"  # scripted group (container) (typed FeaturePython)
  n = 2
  ref = C_element
FEATURE [App::DocumentObjectGroupPython] G4_URANIUM_DICARBIDE  # scripted group (container) (typed FeaturePython)
  Dunit = g/cm3
  Dvalue = 11.28
  Group = -> [U_element001,C_element117]
  conduct = 2
  density = 1
  expand = 3
  formula = G4_URANIUM_DICARBIDE
  name = G4_URANIUM_DICARBIDE
  specific = 4
FEATURE [App::DocumentObjectGroupPython] U_element002  label="U_element : 002"  # scripted group (container) (typed FeaturePython)
  n = 1
  ref = U_element
FEATURE [App::DocumentObjectGroupPython] C_element118  label="C_element : 065"  # scripted group (container) (typed FeaturePython)
  n = 1
  ref = C_element
FEATURE [App::DocumentObjectGroupPython] G4_URANIUM_MONOCARBIDE  # scripted group (container) (typed FeaturePython)
  Dunit = g/cm3
  Dvalue = 13.63
  Group = -> [U_element002,C_element118]
  conduct = 2
  density = 1
  expand = 3
  formula = G4_URANIUM_MONOCARBIDE
  name = G4_URANIUM_MONOCARBIDE
  specific = 4
FEATURE [App::DocumentObjectGroupPython] U_element003  label="U_element : 003"  # scripted group (container) (typed FeaturePython)
  n = 1
  ref = U_element
FEATURE [App::DocumentObjectGroupPython] O_element100  label="O_element : 054"  # scripted group (container) (typed FeaturePython)
  n = 2
  ref = O_element
FEATURE [App::DocumentObjectGroupPython] G4_URANIUM_OXIDE  # scripted group (container) (typed FeaturePython)
  Dunit = g/cm3
  Dvalue = 10.96
  Group = -> [U_element003,O_element100]
  conduct = 2
  density = 1
  expand = 3
  formula = G4_URANIUM_OXIDE
  name = G4_URANIUM_OXIDE
  specific = 4
FEATURE [App::DocumentObjectGroupPython] C_element119  label="C_element : 066"  # scripted group (container) (typed FeaturePython)
  n = 1
  ref = C_element
FEATURE [App::DocumentObjectGroupPython] H_element107  label="H_element : 057"  # scripted group (container) (typed FeaturePython)
  n = 4
  ref = H_element
FEATURE [App::DocumentObjectGroupPython] N_element046  label="N_element : 019"  # scripted group (container) (typed FeaturePython)
  n = 2
  ref = N_element
FEATURE [App::DocumentObjectGroupPython] O_element101  label="O_element : 055"  # scripted group (container) (typed FeaturePython)
  n = 1
  ref = O_element
FEATURE [App::DocumentObjectGroupPython] G4_UREA  # scripted group (container) (typed FeaturePython)
  Dunit = g/cm3
  Dvalue = 1.323
  Group = -> [C_element119,H_element107,N_element046,O_element101]
  conduct = 2
  density = 1
  expand = 3
  formula = G4_UREA
  name = G4_UREA
  specific = 4
FEATURE [App::DocumentObjectGroupPython] C_element120  label="C_element : 067"  # scripted group (container) (typed FeaturePython)
  n = 5
  ref = C_element
FEATURE [App::DocumentObjectGroupPython] H_element108  label="H_element : 058"  # scripted group (container) (typed FeaturePython)
  n = 11
  ref = H_element
FEATURE [App::DocumentObjectGroupPython] N_element047  label="N_element : 020"  # scripted group (container) (typed FeaturePython)
  n = 1
  ref = N_element
FEATURE [App::DocumentObjectGroupPython] O_element102  label="O_element : 056"  # scripted group (container) (typed FeaturePython)
  n = 2
  ref = O_element
FEATURE [App::DocumentObjectGroupPython] G4_VALINE  # scripted group (container) (typed FeaturePython)
  Dunit = g/cm3
  Dvalue = 1.23
  Group = -> [C_element120,H_element108,N_element047,O_element102]
  conduct = 2
  density = 1
  expand = 3
  formula = G4_VALINE
  name = G4_VALINE
  specific = 4
FEATURE [App::DocumentObjectGroupPython] H_element109  label="H_element : 0.009"  # scripted group (container) (typed FeaturePython)
  n = 0.009417
FEATURE [App::DocumentObjectGroupPython] C_element121  label="C_element : 0.281"  # scripted group (container) (typed FeaturePython)
  n = 0.280555
FEATURE [App::DocumentObjectGroupPython] F_element018  label="F_element : 0.710"  # scripted group (container) (typed FeaturePython)
  n = 0.710028
FEATURE [App::DocumentObjectGroupPython] G4_VITON  # scripted group (container) (typed FeaturePython)
  Dunit = g/cm3
  Dvalue = 1.8
  Group = -> [H_element109,C_element121,F_element018]
  conduct = 2
  density = 1
  expand = 3
  formula = G4_VITON
  name = G4_VITON
  specific = 4
FEATURE [App::DocumentObjectGroupPython] H_element110  label="H_element : 059"  # scripted group (container) (typed FeaturePython)
  n = 2
  ref = H_element
FEATURE [App::DocumentObjectGroupPython] O_element103  label="O_element : 057"  # scripted group (container) (typed FeaturePython)
  n = 1
  ref = O_element
FEATURE [App::DocumentObjectGroupPython] G4_WATER  # scripted group (container) (typed FeaturePython)
  Dunit = g/cm3
  Dvalue = 1
  Group = -> [H_element110,O_element103]
  conduct = 2
  density = 1
  expand = 3
  formula = G4_WATER
  name = G4_WATER
  specific = 4
FEATURE [App::DocumentObjectGroupPython] H_element111  label="H_element : 060"  # scripted group (container) (typed FeaturePython)
  n = 2
  ref = H_element
FEATURE [App::DocumentObjectGroupPython] O_element104  label="O_element : 058"  # scripted group (container) (typed FeaturePython)
  n = 1
  ref = O_element
FEATURE [App::DocumentObjectGroupPython] G4_WATER_VAPOR  # scripted group (container) (typed FeaturePython)
  Dunit = g/cm3
  Dvalue = 0.000756182
  Group = -> [H_element111,O_element104]
  conduct = 2
  density = 1
  expand = 3
  formula = G4_WATER_VAPOR
  name = G4_WATER_VAPOR
  specific = 4
FEATURE [App::DocumentObjectGroupPython] C_element122  label="C_element : 068"  # scripted group (container) (typed FeaturePython)
  n = 8
  ref = C_element
FEATURE [App::DocumentObjectGroupPython] H_element112  label="H_element : 061"  # scripted group (container) (typed FeaturePython)
  n = 10
  ref = H_element
FEATURE [App::DocumentObjectGroupPython] G4_XYLENE  # scripted group (container) (typed FeaturePython)
  Dunit = g/cm3
  Dvalue = 0.87
  Group = -> [C_element122,H_element112]
  conduct = 2
  density = 1
  expand = 3
  formula = G4_XYLENE
  name = G4_XYLENE
  specific = 4
FEATURE [App::DocumentObjectGroupPython] C_element123  label="C_element : 069"  # scripted group (container) (typed FeaturePython)
  n = 1
  ref = C_element
FEATURE [App::DocumentObjectGroupPython] G4_GRAPHITE  # scripted group (container) (typed FeaturePython)
  Dunit = g/cm3
  Dvalue = 2.21
  Group = -> [C_element123]
  conduct = 2
  density = 1
  expand = 3
  formula = G4_GRAPHITE
  name = G4_GRAPHITE
  specific = 4
FEATURE [App::DocumentObjectGroupPython] NIST  # scripted group (container) (typed FeaturePython)
  Group = -> [G4_A_150_TISSUE,G4_ACETONE,G4_ACETYLENE,G4_ADENINE,G4_ADIPOSE_TISSUE_ICRP,G4_AIR,G4_ALANINE,G4_ALUMINUM_OXIDE,G4_AMBER,G4_AMMONIA,G4_ANILINE,G4_ANTHRACENE,G4_B_100_BONE,G4_BAKELITE,G4_BARIUM_FLUORIDE,G4_BARIUM_SULFATE,G4_BENZENE,G4_BERYLLIUM_OXIDE,G4_BGO,G4_BLOOD_ICRP,G4_BONE_COMPACT_ICRU,G4_BONE_CORTICAL_ICRP,G4_BORON_CARBIDE,G4_BORON_OXIDE,G4_BRAIN_ICRP,G4_BUTANE,G4_N_BUTYL_ALCOHOL,G4_C_552,+152 more]
FEATURE [App::DocumentObjectGroupPython] H_element113  label="H_element : 062"  # scripted group (container) (typed FeaturePython)
  n = 1
  ref = H_element
FEATURE [App::DocumentObjectGroupPython] G4_H  # scripted group (container) (typed FeaturePython)
  Dunit = g/cm3
  Dvalue = 8.3748e-05
  Group = -> [H_element113]
  conduct = 2
  density = 1
  expand = 3
  formula = H
  name = G4_H
  specific = 4
FEATURE [App::DocumentObjectGroupPython] He_element001  label="He_element : 1"  # scripted group (container) (typed FeaturePython)
  n = 1
  ref = He_element
FEATURE [App::DocumentObjectGroupPython] G4_He  # scripted group (container) (typed FeaturePython)
  Dunit = g/cm3
  Dvalue = 0.000166322
  Group = -> [He_element001]
  conduct = 2
  density = 1
  expand = 3
  formula = He
  name = G4_He
  specific = 4
FEATURE [App::DocumentObjectGroupPython] Li_element008  label="Li_element : 008"  # scripted group (container) (typed FeaturePython)
  n = 1
  ref = Li_element
FEATURE [App::DocumentObjectGroupPython] G4_Li  # scripted group (container) (typed FeaturePython)
  Dunit = g/cm3
  Dvalue = 0.534
  Group = -> [Li_element008]
  conduct = 2
  density = 1
  expand = 3
  formula = Li
  name = G4_Li
  specific = 4
FEATURE [App::DocumentObjectGroupPython] Be_element002  label="Be_element : 002"  # scripted group (container) (typed FeaturePython)
  n = 1
  ref = Be_element
FEATURE [App::DocumentObjectGroupPython] G4_Be  # scripted group (container) (typed FeaturePython)
  Dunit = g/cm3
  Dvalue = 1.848
  Group = -> [Be_element002]
  conduct = 2
  density = 1
  expand = 3
  formula = Be
  name = G4_Be
  specific = 4
FEATURE [App::DocumentObjectGroupPython] B_element007  label="B_element : 007"  # scripted group (container) (typed FeaturePython)
  n = 1
  ref = B_element
FEATURE [App::DocumentObjectGroupPython] G4_B  # scripted group (container) (typed FeaturePython)
  Dunit = g/cm3
  Dvalue = 2.37
  Group = -> [B_element007]
  conduct = 2
  density = 1
  expand = 3
  formula = B
  name = G4_B
  specific = 4
FEATURE [App::DocumentObjectGroupPython] C_element124  label="C_element : 070"  # scripted group (container) (typed FeaturePython)
  n = 1
  ref = C_element
FEATURE [App::DocumentObjectGroupPython] G4_C  # scripted group (container) (typed FeaturePython)
  Dunit = g/cm3
  Dvalue = 2
  Group = -> [C_element124]
  conduct = 2
  density = 1
  expand = 3
  formula = C
  name = G4_C
  specific = 4
FEATURE [App::DocumentObjectGroupPython] N_element048  label="N_element : 021"  # scripted group (container) (typed FeaturePython)
  n = 1
  ref = N_element
FEATURE [App::DocumentObjectGroupPython] G4_N  # scripted group (container) (typed FeaturePython)
  Dunit = g/cm3
  Dvalue = 0.0011652
  Group = -> [N_element048]
  conduct = 2
  density = 1
  expand = 3
  formula = N
  name = G4_N
  specific = 4
FEATURE [App::DocumentObjectGroupPython] O_element105  label="O_element : 059"  # scripted group (container) (typed FeaturePython)
  n = 1
  ref = O_element
FEATURE [App::DocumentObjectGroupPython] G4_O  # scripted group (container) (typed FeaturePython)
  Dunit = g/cm3
  Dvalue = 0.00133151
  Group = -> [O_element105]
  conduct = 2
  density = 1
  expand = 3
  formula = O
  name = G4_O
  specific = 4
FEATURE [App::DocumentObjectGroupPython] F_element019  label="F_element : 008"  # scripted group (container) (typed FeaturePython)
  n = 1
  ref = F_element
FEATURE [App::DocumentObjectGroupPython] G4_F  # scripted group (container) (typed FeaturePython)
  Dunit = g/cm3
  Dvalue = 0.00158029
  Group = -> [F_element019]
  conduct = 2
  density = 1
  expand = 3
  formula = F
  name = G4_F
  specific = 4
FEATURE [App::DocumentObjectGroupPython] Ne_element001  label="Ne_element : 1"  # scripted group (container) (typed FeaturePython)
  n = 1
  ref = Ne_element
FEATURE [App::DocumentObjectGroupPython] G4_Ne  # scripted group (container) (typed FeaturePython)
  Dunit = g/cm3
  Dvalue = 0.000838505
  Group = -> [Ne_element001]
  conduct = 2
  density = 1
  expand = 3
  formula = Ne
  name = G4_Ne
  specific = 4
FEATURE [App::DocumentObjectGroupPython] Na_element020  label="Na_element : 005"  # scripted group (container) (typed FeaturePython)
  n = 1
  ref = Na_element
FEATURE [App::DocumentObjectGroupPython] G4_Na  # scripted group (container) (typed FeaturePython)
  Dunit = g/cm3
  Dvalue = 0.971
  Group = -> [Na_element020]
  conduct = 2
  density = 1
  expand = 3
  formula = Na
  name = G4_Na
  specific = 4
FEATURE [App::DocumentObjectGroupPython] Mg_element011  label="Mg_element : 005"  # scripted group (container) (typed FeaturePython)
  n = 1
  ref = Mg_element
FEATURE [App::DocumentObjectGroupPython] G4_Mg  # scripted group (container) (typed FeaturePython)
  Dunit = g/cm3
  Dvalue = 1.74
  Group = -> [Mg_element011]
  conduct = 2
  density = 1
  expand = 3
  formula = Mg
  name = G4_Mg
  specific = 4
FEATURE [App::DocumentObjectGroupPython] Al_element004  label="Al_element : 1"  # scripted group (container) (typed FeaturePython)
  n = 1
  ref = Al_element
FEATURE [App::DocumentObjectGroupPython] G4_Al  # scripted group (container) (typed FeaturePython)
  Dunit = g/cm3
  Dvalue = 2.699
  Group = -> [Al_element004]
  conduct = 2
  density = 1
  expand = 3
  formula = Al
  name = G4_Al
  specific = 4
FEATURE [App::DocumentObjectGroupPython] Si_element007  label="Si_element : 002"  # scripted group (container) (typed FeaturePython)
  n = 1
  ref = Si_element
FEATURE [App::DocumentObjectGroupPython] G4_Si  # scripted group (container) (typed FeaturePython)
  Dunit = g/cm3
  Dvalue = 2.33
  Group = -> [Si_element007]
  conduct = 2
  density = 1
  expand = 3
  formula = Si
  name = G4_Si
  specific = 4
FEATURE [App::DocumentObjectGroupPython] P_element013  label="P_element : 002"  # scripted group (container) (typed FeaturePython)
  n = 1
  ref = P_element
FEATURE [App::DocumentObjectGroupPython] G4_P  # scripted group (container) (typed FeaturePython)
  Dunit = g/cm3
  Dvalue = 2.2
  Group = -> [P_element013]
  conduct = 2
  density = 1
  expand = 3
  formula = P
  name = G4_P
  specific = 4
FEATURE [App::DocumentObjectGroupPython] S_element023  label="S_element : 007"  # scripted group (container) (typed FeaturePython)
  n = 1
  ref = S_element
FEATURE [App::DocumentObjectGroupPython] G4_S  # scripted group (container) (typed FeaturePython)
  Dunit = g/cm3
  Dvalue = 2
  Group = -> [S_element023]
  conduct = 2
  density = 1
  expand = 3
  formula = S
  name = G4_S
  specific = 4
FEATURE [App::DocumentObjectGroupPython] Cl_element029  label="Cl_element : 015"  # scripted group (container) (typed FeaturePython)
  n = 1
  ref = Cl_element
FEATURE [App::DocumentObjectGroupPython] G4_Cl  # scripted group (container) (typed FeaturePython)
  Dunit = g/cm3
  Dvalue = 0.00299473
  Group = -> [Cl_element029]
  conduct = 2
  density = 1
  expand = 3
  formula = Cl
  name = G4_Cl
  specific = 4
FEATURE [App::DocumentObjectGroupPython] Ar_element002  label="Ar_element : 1"  # scripted group (container) (typed FeaturePython)
  n = 1
  ref = Ar_element
FEATURE [App::DocumentObjectGroupPython] G4_Ar  # scripted group (container) (typed FeaturePython)
  Dunit = g/cm3
  Dvalue = 0.00166201
  Group = -> [Ar_element002]
  conduct = 2
  density = 1
  expand = 3
  formula = Ar
  name = G4_Ar
  specific = 4
FEATURE [App::DocumentObjectGroupPython] K_element013  label="K_element : 003"  # scripted group (container) (typed FeaturePython)
  n = 1
  ref = K_element
FEATURE [App::DocumentObjectGroupPython] G4_K  # scripted group (container) (typed FeaturePython)
  Dunit = g/cm3
  Dvalue = 0.862
  Group = -> [K_element013]
  conduct = 2
  density = 1
  expand = 3
  formula = K
  name = G4_K
  specific = 4
FEATURE [App::DocumentObjectGroupPython] Ca_element014  label="Ca_element : 007"  # scripted group (container) (typed FeaturePython)
  n = 1
  ref = Ca_element
FEATURE [App::DocumentObjectGroupPython] G4_Ca  # scripted group (container) (typed FeaturePython)
  Dunit = g/cm3
  Dvalue = 1.55
  Group = -> [Ca_element014]
  conduct = 2
  density = 1
  expand = 3
  formula = Ca
  name = G4_Ca
  specific = 4
FEATURE [App::DocumentObjectGroupPython] Sc_element001  label="Sc_element : 1"  # scripted group (container) (typed FeaturePython)
  n = 1
  ref = Sc_element
FEATURE [App::DocumentObjectGroupPython] G4_Sc  # scripted group (container) (typed FeaturePython)
  Dunit = g/cm3
  Dvalue = 2.989
  Group = -> [Sc_element001]
  conduct = 2
  density = 1
  expand = 3
  formula = Sc
  name = G4_Sc
  specific = 4
FEATURE [App::DocumentObjectGroupPython] Ti_element004  label="Ti_element : 002"  # scripted group (container) (typed FeaturePython)
  n = 1
  ref = Ti_element
FEATURE [App::DocumentObjectGroupPython] G4_Ti  # scripted group (container) (typed FeaturePython)
  Dunit = g/cm3
  Dvalue = 4.54
  Group = -> [Ti_element004]
  conduct = 2
  density = 1
  expand = 3
  formula = Ti
  name = G4_Ti
  specific = 4
FEATURE [App::DocumentObjectGroupPython] V_element001  label="V_element : 1"  # scripted group (container) (typed FeaturePython)
  n = 1
  ref = V_element
FEATURE [App::DocumentObjectGroupPython] G4_V  # scripted group (container) (typed FeaturePython)
  Dunit = g/cm3
  Dvalue = 6.11
  Group = -> [V_element001]
  conduct = 2
  density = 1
  expand = 3
  formula = V
  name = G4_V
  specific = 4
FEATURE [App::DocumentObjectGroupPython] Cr_element001  label="Cr_element : 1"  # scripted group (container) (typed FeaturePython)
  n = 1
  ref = Cr_element
FEATURE [App::DocumentObjectGroupPython] G4_Cr  # scripted group (container) (typed FeaturePython)
  Dunit = g/cm3
  Dvalue = 7.18
  Group = -> [Cr_element001]
  conduct = 2
  density = 1
  expand = 3
  formula = Cr
  name = G4_Cr
  specific = 4
FEATURE [App::DocumentObjectGroupPython] Mn_element001  label="Mn_element : 1"  # scripted group (container) (typed FeaturePython)
  n = 1
  ref = Mn_element
FEATURE [App::DocumentObjectGroupPython] G4_Mn  # scripted group (container) (typed FeaturePython)
  Dunit = g/cm3
  Dvalue = 7.44
  Group = -> [Mn_element001]
  conduct = 2
  density = 1
  expand = 3
  formula = Mn
  name = G4_Mn
  specific = 4
FEATURE [App::DocumentObjectGroupPython] Fe_element007  label="Fe_element : 004"  # scripted group (container) (typed FeaturePython)
  n = 1
  ref = Fe_element
FEATURE [App::DocumentObjectGroupPython] G4_Fe  # scripted group (container) (typed FeaturePython)
  Dunit = g/cm3
  Dvalue = 7.874
  Group = -> [Fe_element007]
  conduct = 2
  density = 1
  expand = 3
  formula = Fe
  name = G4_Fe
  specific = 4
FEATURE [App::DocumentObjectGroupPython] Co_element001  label="Co_element : 1"  # scripted group (container) (typed FeaturePython)
  n = 1
  ref = Co_element
FEATURE [App::DocumentObjectGroupPython] G4_Co  # scripted group (container) (typed FeaturePython)
  Dunit = g/cm3
  Dvalue = 8.9
  Group = -> [Co_element001]
  conduct = 2
  density = 1
  expand = 3
  formula = Co
  name = G4_Co
  specific = 4
FEATURE [App::DocumentObjectGroupPython] Ni_element001  label="Ni_element : 1"  # scripted group (container) (typed FeaturePython)
  n = 1
  ref = Ni_element
FEATURE [App::DocumentObjectGroupPython] G4_Ni  # scripted group (container) (typed FeaturePython)
  Dunit = g/cm3
  Dvalue = 8.902
  Group = -> [Ni_element001]
  conduct = 2
  density = 1
  expand = 3
  formula = Ni
  name = G4_Ni
  specific = 4
FEATURE [App::DocumentObjectGroupPython] Cu_element001  label="Cu_element : 1"  # scripted group (container) (typed FeaturePython)
  n = 1
  ref = Cu_element
FEATURE [App::DocumentObjectGroupPython] G4_Cu  # scripted group (container) (typed FeaturePython)
  Dunit = g/cm3
  Dvalue = 8.96
  Group = -> [Cu_element001]
  conduct = 2
  density = 1
  expand = 3
  formula = Cu
  name = G4_Cu
  specific = 4
FEATURE [App::DocumentObjectGroupPython] Zn_element001  label="Zn_element : 1"  # scripted group (container) (typed FeaturePython)
  n = 1
  ref = Zn_element
FEATURE [App::DocumentObjectGroupPython] G4_Zn  # scripted group (container) (typed FeaturePython)
  Dunit = g/cm3
  Dvalue = 7.133
  Group = -> [Zn_element001]
  conduct = 2
  density = 1
  expand = 3
  formula = Zn
  name = G4_Zn
  specific = 4
FEATURE [App::DocumentObjectGroupPython] Ga_element002  label="Ga_element : 002"  # scripted group (container) (typed FeaturePython)
  n = 1
  ref = Ga_element
FEATURE [App::DocumentObjectGroupPython] G4_Ga  # scripted group (container) (typed FeaturePython)
  Dunit = g/cm3
  Dvalue = 5.904
  Group = -> [Ga_element002]
  conduct = 2
  density = 1
  expand = 3
  formula = Ga
  name = G4_Ga
  specific = 4
FEATURE [App::DocumentObjectGroupPython] Ge_element002  label="Ge_element : 1"  # scripted group (container) (typed FeaturePython)
  n = 1
  ref = Ge_element
FEATURE [App::DocumentObjectGroupPython] G4_Ge  # scripted group (container) (typed FeaturePython)
  Dunit = g/cm3
  Dvalue = 5.323
  Group = -> [Ge_element002]
  conduct = 2
  density = 1
  expand = 3
  formula = Ge
  name = G4_Ge
  specific = 4
FEATURE [App::DocumentObjectGroupPython] As_element003  label="As_element : 002"  # scripted group (container) (typed FeaturePython)
  n = 1
  ref = As_element
FEATURE [App::DocumentObjectGroupPython] G4_As  # scripted group (container) (typed FeaturePython)
  Dunit = g/cm3
  Dvalue = 5.73
  Group = -> [As_element003]
  conduct = 2
  density = 1
  expand = 3
  formula = As
  name = G4_As
  specific = 4
FEATURE [App::DocumentObjectGroupPython] Se_element001  label="Se_element : 1"  # scripted group (container) (typed FeaturePython)
  n = 1
  ref = Se_element
FEATURE [App::DocumentObjectGroupPython] G4_Se  # scripted group (container) (typed FeaturePython)
  Dunit = g/cm3
  Dvalue = 4.5
  Group = -> [Se_element001]
  conduct = 2
  density = 1
  expand = 3
  formula = Se
  name = G4_Se
  specific = 4
FEATURE [App::DocumentObjectGroupPython] Br_element007  label="Br_element : 004"  # scripted group (container) (typed FeaturePython)
  n = 1
  ref = Br_element
FEATURE [App::DocumentObjectGroupPython] G4_Br  # scripted group (container) (typed FeaturePython)
  Dunit = g/cm3
  Dvalue = 0.0070721
  Group = -> [Br_element007]
  conduct = 2
  density = 1
  expand = 3
  formula = Br
  name = G4_Br
  specific = 4
FEATURE [App::DocumentObjectGroupPython] Kr_element001  label="Kr_element : 1"  # scripted group (container) (typed FeaturePython)
  n = 1
  ref = Kr_element
FEATURE [App::DocumentObjectGroupPython] G4_Kr  # scripted group (container) (typed FeaturePython)
  Dunit = g/cm3
  Dvalue = 0.00347832
  Group = -> [Kr_element001]
  conduct = 2
  density = 1
  expand = 3
  formula = Kr
  name = G4_Kr
  specific = 4
FEATURE [App::DocumentObjectGroupPython] Rb_element001  label="Rb_element : 1"  # scripted group (container) (typed FeaturePython)
  n = 1
  ref = Rb_element
FEATURE [App::DocumentObjectGroupPython] G4_Rb  # scripted group (container) (typed FeaturePython)
  Dunit = g/cm3
  Dvalue = 1.532
  Group = -> [Rb_element001]
  conduct = 2
  density = 1
  expand = 3
  formula = Rb
  name = G4_Rb
  specific = 4
FEATURE [App::DocumentObjectGroupPython] Sr_element001  label="Sr_element : 1"  # scripted group (container) (typed FeaturePython)
  n = 1
  ref = Sr_element
FEATURE [App::DocumentObjectGroupPython] G4_Sr  # scripted group (container) (typed FeaturePython)
  Dunit = g/cm3
  Dvalue = 2.54
  Group = -> [Sr_element001]
  conduct = 2
  density = 1
  expand = 3
  formula = Sr
  name = G4_Sr
  specific = 4
FEATURE [App::DocumentObjectGroupPython] Y_element001  label="Y_element : 1"  # scripted group (container) (typed FeaturePython)
  n = 1
  ref = Y_element
FEATURE [App::DocumentObjectGroupPython] G4_Y  # scripted group (container) (typed FeaturePython)
  Dunit = g/cm3
  Dvalue = 4.469
  Group = -> [Y_element001]
  conduct = 2
  density = 1
  expand = 3
  formula = Y
  name = G4_Y
  specific = 4
FEATURE [App::DocumentObjectGroupPython] Zr_element001  label="Zr_element : 1"  # scripted group (container) (typed FeaturePython)
  n = 1
  ref = Zr_element
FEATURE [App::DocumentObjectGroupPython] G4_Zr  # scripted group (container) (typed FeaturePython)
  Dunit = g/cm3
  Dvalue = 6.506
  Group = -> [Zr_element001]
  conduct = 2
  density = 1
  expand = 3
  formula = Zr
  name = G4_Zr
  specific = 4
FEATURE [App::DocumentObjectGroupPython] Nb_element001  label="Nb_element : 1"  # scripted group (container) (typed FeaturePython)
  n = 1
  ref = Nb_element
FEATURE [App::DocumentObjectGroupPython] G4_Nb  # scripted group (container) (typed FeaturePython)
  Dunit = g/cm3
  Dvalue = 8.57
  Group = -> [Nb_element001]
  conduct = 2
  density = 1
  expand = 3
  formula = Nb
  name = G4_Nb
  specific = 4
FEATURE [App::DocumentObjectGroupPython] Mo_element001  label="Mo_element : 1"  # scripted group (container) (typed FeaturePython)
  n = 1
  ref = Mo_element
FEATURE [App::DocumentObjectGroupPython] G4_Mo  # scripted group (container) (typed FeaturePython)
  Dunit = g/cm3
  Dvalue = 10.22
  Group = -> [Mo_element001]
  conduct = 2
  density = 1
  expand = 3
  formula = Mo
  name = G4_Mo
  specific = 4
FEATURE [App::DocumentObjectGroupPython] Tc_element001  label="Tc_element : 1"  # scripted group (container) (typed FeaturePython)
  n = 1
  ref = Tc_element
FEATURE [App::DocumentObjectGroupPython] G4_Tc  # scripted group (container) (typed FeaturePython)
  Dunit = g/cm3
  Dvalue = 11.5
  Group = -> [Tc_element001]
  conduct = 2
  density = 1
  expand = 3
  formula = Tc
  name = G4_Tc
  specific = 4
FEATURE [App::DocumentObjectGroupPython] Ru_element001  label="Ru_element : 1"  # scripted group (container) (typed FeaturePython)
  n = 1
  ref = Ru_element
FEATURE [App::DocumentObjectGroupPython] G4_Ru  # scripted group (container) (typed FeaturePython)
  Dunit = g/cm3
  Dvalue = 12.41
  Group = -> [Ru_element001]
  conduct = 2
  density = 1
  expand = 3
  formula = Ru
  name = G4_Ru
  specific = 4
FEATURE [App::DocumentObjectGroupPython] Rh_element001  label="Rh_element : 1"  # scripted group (container) (typed FeaturePython)
  n = 1
  ref = Rh_element
FEATURE [App::DocumentObjectGroupPython] G4_Rh  # scripted group (container) (typed FeaturePython)
  Dunit = g/cm3
  Dvalue = 12.41
  Group = -> [Rh_element001]
  conduct = 2
  density = 1
  expand = 3
  formula = Rh
  name = G4_Rh
  specific = 4
FEATURE [App::DocumentObjectGroupPython] Pd_element001  label="Pd_element : 1"  # scripted group (container) (typed FeaturePython)
  n = 1
  ref = Pd_element
FEATURE [App::DocumentObjectGroupPython] G4_Pd  # scripted group (container) (typed FeaturePython)
  Dunit = g/cm3
  Dvalue = 12.02
  Group = -> [Pd_element001]
  conduct = 2
  density = 1
  expand = 3
  formula = Pd
  name = G4_Pd
  specific = 4
FEATURE [App::DocumentObjectGroupPython] Ag_element006  label="Ag_element : 004"  # scripted group (container) (typed FeaturePython)
  n = 1
  ref = Ag_element
FEATURE [App::DocumentObjectGroupPython] G4_Ag  # scripted group (container) (typed FeaturePython)
  Dunit = g/cm3
  Dvalue = 10.5
  Group = -> [Ag_element006]
  conduct = 2
  density = 1
  expand = 3
  formula = Ag
  name = G4_Ag
  specific = 4
FEATURE [App::DocumentObjectGroupPython] Cd_element003  label="Cd_element : 003"  # scripted group (container) (typed FeaturePython)
  n = 1
  ref = Cd_element
FEATURE [App::DocumentObjectGroupPython] G4_Cd  # scripted group (container) (typed FeaturePython)
  Dunit = g/cm3
  Dvalue = 8.65
  Group = -> [Cd_element003]
  conduct = 2
  density = 1
  expand = 3
  formula = Cd
  name = G4_Cd
  specific = 4
FEATURE [App::DocumentObjectGroupPython] In_element001  label="In_element : 1"  # scripted group (container) (typed FeaturePython)
  n = 1
  ref = In_element
FEATURE [App::DocumentObjectGroupPython] G4_In  # scripted group (container) (typed FeaturePython)
  Dunit = g/cm3
  Dvalue = 7.31
  Group = -> [In_element001]
  conduct = 2
  density = 1
  expand = 3
  formula = In
  name = G4_In
  specific = 4
FEATURE [App::DocumentObjectGroupPython] Sn_element001  label="Sn_element : 1"  # scripted group (container) (typed FeaturePython)
  n = 1
  ref = Sn_element
FEATURE [App::DocumentObjectGroupPython] G4_Sn  # scripted group (container) (typed FeaturePython)
  Dunit = g/cm3
  Dvalue = 7.31
  Group = -> [Sn_element001]
  conduct = 2
  density = 1
  expand = 3
  formula = Sn
  name = G4_Sn
  specific = 4
FEATURE [App::DocumentObjectGroupPython] Sb_element001  label="Sb_element : 1"  # scripted group (container) (typed FeaturePython)
  n = 1
  ref = Sb_element
FEATURE [App::DocumentObjectGroupPython] G4_Sb  # scripted group (container) (typed FeaturePython)
  Dunit = g/cm3
  Dvalue = 6.691
  Group = -> [Sb_element001]
  conduct = 2
  density = 1
  expand = 3
  formula = Sb
  name = G4_Sb
  specific = 4
FEATURE [App::DocumentObjectGroupPython] Te_element002  label="Te_element : 002"  # scripted group (container) (typed FeaturePython)
  n = 1
  ref = Te_element
FEATURE [App::DocumentObjectGroupPython] G4_Te  # scripted group (container) (typed FeaturePython)
  Dunit = g/cm3
  Dvalue = 6.24
  Group = -> [Te_element002]
  conduct = 2
  density = 1
  expand = 3
  formula = Te
  name = G4_Te
  specific = 4
FEATURE [App::DocumentObjectGroupPython] I_element010  label="I_element : 006"  # scripted group (container) (typed FeaturePython)
  n = 1
  ref = I_element
FEATURE [App::DocumentObjectGroupPython] G4_I  # scripted group (container) (typed FeaturePython)
  Dunit = g/cm3
  Dvalue = 4.93
  Group = -> [I_element010]
  conduct = 2
  density = 1
  expand = 3
  formula = I
  name = G4_I
  specific = 4
FEATURE [App::DocumentObjectGroupPython] Xe_element001  label="Xe_element : 1"  # scripted group (container) (typed FeaturePython)
  n = 1
  ref = Xe_element
FEATURE [App::DocumentObjectGroupPython] G4_Xe  # scripted group (container) (typed FeaturePython)
  Dunit = g/cm3
  Dvalue = 0.00548536
  Group = -> [Xe_element001]
  conduct = 2
  density = 1
  expand = 3
  formula = Xe
  name = G4_Xe
  specific = 4
FEATURE [App::DocumentObjectGroupPython] Cs_element003  label="Cs_element : 003"  # scripted group (container) (typed FeaturePython)
  n = 1
  ref = Cs_element
FEATURE [App::DocumentObjectGroupPython] G4_Cs  # scripted group (container) (typed FeaturePython)
  Dunit = g/cm3
  Dvalue = 1.873
  Group = -> [Cs_element003]
  conduct = 2
  density = 1
  expand = 3
  formula = Cs
  name = G4_Cs
  specific = 4
FEATURE [App::DocumentObjectGroupPython] Ba_element003  label="Ba_element : 003"  # scripted group (container) (typed FeaturePython)
  n = 1
  ref = Ba_element
FEATURE [App::DocumentObjectGroupPython] G4_Ba  # scripted group (container) (typed FeaturePython)
  Dunit = g/cm3
  Dvalue = 3.5
  Group = -> [Ba_element003]
  conduct = 2
  density = 1
  expand = 3
  formula = Ba
  name = G4_Ba
  specific = 4
FEATURE [App::DocumentObjectGroupPython] La_element003  label="La_element : 003"  # scripted group (container) (typed FeaturePython)
  n = 1
  ref = La_element
FEATURE [App::DocumentObjectGroupPython] G4_La  # scripted group (container) (typed FeaturePython)
  Dunit = g/cm3
  Dvalue = 6.154
  Group = -> [La_element003]
  conduct = 2
  density = 1
  expand = 3
  formula = La
  name = G4_La
  specific = 4
FEATURE [App::DocumentObjectGroupPython] Ce_element002  label="Ce_element : 1"  # scripted group (container) (typed FeaturePython)
  n = 1
  ref = Ce_element
FEATURE [App::DocumentObjectGroupPython] G4_Ce  # scripted group (container) (typed FeaturePython)
  Dunit = g/cm3
  Dvalue = 6.657
  Group = -> [Ce_element002]
  conduct = 2
  density = 1
  expand = 3
  formula = Ce
  name = G4_Ce
  specific = 4
FEATURE [App::DocumentObjectGroupPython] Pr_element001  label="Pr_element : 1"  # scripted group (container) (typed FeaturePython)
  n = 1
  ref = Pr_element
FEATURE [App::DocumentObjectGroupPython] G4_Pr  # scripted group (container) (typed FeaturePython)
  Dunit = g/cm3
  Dvalue = 6.71
  Group = -> [Pr_element001]
  conduct = 2
  density = 1
  expand = 3
  formula = Pr
  name = G4_Pr
  specific = 4
FEATURE [App::DocumentObjectGroupPython] Nd_element001  label="Nd_element : 1"  # scripted group (container) (typed FeaturePython)
  n = 1
  ref = Nd_element
FEATURE [App::DocumentObjectGroupPython] G4_Nd  # scripted group (container) (typed FeaturePython)
  Dunit = g/cm3
  Dvalue = 6.9
  Group = -> [Nd_element001]
  conduct = 2
  density = 1
  expand = 3
  formula = Nd
  name = G4_Nd
  specific = 4
FEATURE [App::DocumentObjectGroupPython] Pm_element001  label="Pm_element : 1"  # scripted group (container) (typed FeaturePython)
  n = 1
  ref = Pm_element
FEATURE [App::DocumentObjectGroupPython] G4_Pm  # scripted group (container) (typed FeaturePython)
  Dunit = g/cm3
  Dvalue = 7.22
  Group = -> [Pm_element001]
  conduct = 2
  density = 1
  expand = 3
  formula = Pm
  name = G4_Pm
  specific = 4
FEATURE [App::DocumentObjectGroupPython] Sm_element001  label="Sm_element : 1"  # scripted group (container) (typed FeaturePython)
  n = 1
  ref = Sm_element
FEATURE [App::DocumentObjectGroupPython] G4_Sm  # scripted group (container) (typed FeaturePython)
  Dunit = g/cm3
  Dvalue = 7.46
  Group = -> [Sm_element001]
  conduct = 2
  density = 1
  expand = 3
  formula = Sm
  name = G4_Sm
  specific = 4
FEATURE [App::DocumentObjectGroupPython] Eu_element001  label="Eu_element : 1"  # scripted group (container) (typed FeaturePython)
  n = 1
  ref = Eu_element
FEATURE [App::DocumentObjectGroupPython] G4_Eu  # scripted group (container) (typed FeaturePython)
  Dunit = g/cm3
  Dvalue = 5.243
  Group = -> [Eu_element001]
  conduct = 2
  density = 1
  expand = 3
  formula = Eu
  name = G4_Eu
  specific = 4
FEATURE [App::DocumentObjectGroupPython] Gd_element002  label="Gd_element : 1"  # scripted group (container) (typed FeaturePython)
  n = 1
  ref = Gd_element
FEATURE [App::DocumentObjectGroupPython] G4_Gd  # scripted group (container) (typed FeaturePython)
  Dunit = g/cm3
  Dvalue = 7.9004
  Group = -> [Gd_element002]
  conduct = 2
  density = 1
  expand = 3
  formula = Gd
  name = G4_Gd
  specific = 4
FEATURE [App::DocumentObjectGroupPython] Tb_element001  label="Tb_element : 1"  # scripted group (container) (typed FeaturePython)
  n = 1
  ref = Tb_element
FEATURE [App::DocumentObjectGroupPython] G4_Tb  # scripted group (container) (typed FeaturePython)
  Dunit = g/cm3
  Dvalue = 8.229
  Group = -> [Tb_element001]
  conduct = 2
  density = 1
  expand = 3
  formula = Tb
  name = G4_Tb
  specific = 4
FEATURE [App::DocumentObjectGroupPython] Dy_element001  label="Dy_element : 1"  # scripted group (container) (typed FeaturePython)
  n = 1
  ref = Dy_element
FEATURE [App::DocumentObjectGroupPython] G4_Dy  # scripted group (container) (typed FeaturePython)
  Dunit = g/cm3
  Dvalue = 8.55
  Group = -> [Dy_element001]
  conduct = 2
  density = 1
  expand = 3
  formula = Dy
  name = G4_Dy
  specific = 4
FEATURE [App::DocumentObjectGroupPython] Ho_element001  label="Ho_element : 1"  # scripted group (container) (typed FeaturePython)
  n = 1
  ref = Ho_element
FEATURE [App::DocumentObjectGroupPython] G4_Ho  # scripted group (container) (typed FeaturePython)
  Dunit = g/cm3
  Dvalue = 8.795
  Group = -> [Ho_element001]
  conduct = 2
  density = 1
  expand = 3
  formula = Ho
  name = G4_Ho
  specific = 4
FEATURE [App::DocumentObjectGroupPython] Er_element001  label="Er_element : 1"  # scripted group (container) (typed FeaturePython)
  n = 1
  ref = Er_element
FEATURE [App::DocumentObjectGroupPython] G4_Er  # scripted group (container) (typed FeaturePython)
  Dunit = g/cm3
  Dvalue = 9.066
  Group = -> [Er_element001]
  conduct = 2
  density = 1
  expand = 3
  formula = Er
  name = G4_Er
  specific = 4
FEATURE [App::DocumentObjectGroupPython] Tm_element001  label="Tm_element : 1"  # scripted group (container) (typed FeaturePython)
  n = 1
  ref = Tm_element
FEATURE [App::DocumentObjectGroupPython] G4_Tm  # scripted group (container) (typed FeaturePython)
  Dunit = g/cm3
  Dvalue = 9.321
  Group = -> [Tm_element001]
  conduct = 2
  density = 1
  expand = 3
  formula = Tm
  name = G4_Tm
  specific = 4
FEATURE [App::DocumentObjectGroupPython] Yb_element001  label="Yb_element : 1"  # scripted group (container) (typed FeaturePython)
  n = 1
  ref = Yb_element
FEATURE [App::DocumentObjectGroupPython] G4_Yb  # scripted group (container) (typed FeaturePython)
  Dunit = g/cm3
  Dvalue = 6.73
  Group = -> [Yb_element001]
  conduct = 2
  density = 1
  expand = 3
  formula = Yb
  name = G4_Yb
  specific = 4
FEATURE [App::DocumentObjectGroupPython] Lu_element001  label="Lu_element : 1"  # scripted group (container) (typed FeaturePython)
  n = 1
  ref = Lu_element
FEATURE [App::DocumentObjectGroupPython] G4_Lu  # scripted group (container) (typed FeaturePython)
  Dunit = g/cm3
  Dvalue = 9.84
  Group = -> [Lu_element001]
  conduct = 2
  density = 1
  expand = 3
  formula = Lu
  name = G4_Lu
  specific = 4
FEATURE [App::DocumentObjectGroupPython] Hf_element001  label="Hf_element : 1"  # scripted group (container) (typed FeaturePython)
  n = 1
  ref = Hf_element
FEATURE [App::DocumentObjectGroupPython] G4_Hf  # scripted group (container) (typed FeaturePython)
  Dunit = g/cm3
  Dvalue = 13.31
  Group = -> [Hf_element001]
  conduct = 2
  density = 1
  expand = 3
  formula = Hf
  name = G4_Hf
  specific = 4
FEATURE [App::DocumentObjectGroupPython] Ta_element001  label="Ta_element : 1"  # scripted group (container) (typed FeaturePython)
  n = 1
  ref = Ta_element
FEATURE [App::DocumentObjectGroupPython] G4_Ta  # scripted group (container) (typed FeaturePython)
  Dunit = g/cm3
  Dvalue = 16.654
  Group = -> [Ta_element001]
  conduct = 2
  density = 1
  expand = 3
  formula = Ta
  name = G4_Ta
  specific = 4
FEATURE [App::DocumentObjectGroupPython] W_element004  label="W_element : 004"  # scripted group (container) (typed FeaturePython)
  n = 1
  ref = W_element
FEATURE [App::DocumentObjectGroupPython] G4_W  # scripted group (container) (typed FeaturePython)
  Dunit = g/cm3
  Dvalue = 19.3
  Group = -> [W_element004]
  conduct = 2
  density = 1
  expand = 3
  formula = W
  name = G4_W
  specific = 4
FEATURE [App::DocumentObjectGroupPython] Re_element001  label="Re_element : 1"  # scripted group (container) (typed FeaturePython)
  n = 1
  ref = Re_element
FEATURE [App::DocumentObjectGroupPython] G4_Re  # scripted group (container) (typed FeaturePython)
  Dunit = g/cm3
  Dvalue = 21.02
  Group = -> [Re_element001]
  conduct = 2
  density = 1
  expand = 3
  formula = Re
  name = G4_Re
  specific = 4
FEATURE [App::DocumentObjectGroupPython] Os_element001  label="Os_element : 1"  # scripted group (container) (typed FeaturePython)
  n = 1
  ref = Os_element
FEATURE [App::DocumentObjectGroupPython] G4_Os  # scripted group (container) (typed FeaturePython)
  Dunit = g/cm3
  Dvalue = 22.57
  Group = -> [Os_element001]
  conduct = 2
  density = 1
  expand = 3
  formula = Os
  name = G4_Os
  specific = 4
FEATURE [App::DocumentObjectGroupPython] Ir_element001  label="Ir_element : 1"  # scripted group (container) (typed FeaturePython)
  n = 1
  ref = Ir_element
FEATURE [App::DocumentObjectGroupPython] G4_Ir  # scripted group (container) (typed FeaturePython)
  Dunit = g/cm3
  Dvalue = 22.42
  Group = -> [Ir_element001]
  conduct = 2
  density = 1
  expand = 3
  formula = Ir
  name = G4_Ir
  specific = 4
FEATURE [App::DocumentObjectGroupPython] Pt_element001  label="Pt_element : 1"  # scripted group (container) (typed FeaturePython)
  n = 1
  ref = Pt_element
FEATURE [App::DocumentObjectGroupPython] G4_Pt  # scripted group (container) (typed FeaturePython)
  Dunit = g/cm3
  Dvalue = 21.45
  Group = -> [Pt_element001]
  conduct = 2
  density = 1
  expand = 3
  formula = Pt
  name = G4_Pt
  specific = 4
FEATURE [App::DocumentObjectGroupPython] Au_element001  label="Au_element : 1"  # scripted group (container) (typed FeaturePython)
  n = 1
  ref = Au_element
FEATURE [App::DocumentObjectGroupPython] G4_Au  # scripted group (container) (typed FeaturePython)
  Dunit = g/cm3
  Dvalue = 19.32
  Group = -> [Au_element001]
  conduct = 2
  density = 1
  expand = 3
  formula = Au
  name = G4_Au
  specific = 4
FEATURE [App::DocumentObjectGroupPython] Hg_element002  label="Hg_element : 002"  # scripted group (container) (typed FeaturePython)
  n = 1
  ref = Hg_element
FEATURE [App::DocumentObjectGroupPython] G4_Hg  # scripted group (container) (typed FeaturePython)
  Dunit = g/cm3
  Dvalue = 13.546
  Group = -> [Hg_element002]
  conduct = 2
  density = 1
  expand = 3
  formula = Hg
  name = G4_Hg
  specific = 4
FEATURE [App::DocumentObjectGroupPython] Tl_element002  label="Tl_element : 002"  # scripted group (container) (typed FeaturePython)
  n = 1
  ref = Tl_element
FEATURE [App::DocumentObjectGroupPython] G4_Tl  # scripted group (container) (typed FeaturePython)
  Dunit = g/cm3
  Dvalue = 11.72
  Group = -> [Tl_element002]
  conduct = 2
  density = 1
  expand = 3
  formula = Tl
  name = G4_Tl
  specific = 4
FEATURE [App::DocumentObjectGroupPython] Pb_element003  label="Pb_element : 1"  # scripted group (container) (typed FeaturePython)
  n = 1
  ref = Pb_element
FEATURE [App::DocumentObjectGroupPython] G4_Pb  # scripted group (container) (typed FeaturePython)
  Dunit = g/cm3
  Dvalue = 11.35
  Group = -> [Pb_element003]
  conduct = 2
  density = 1
  expand = 3
  formula = Pb
  name = G4_Pb
  specific = 4
FEATURE [App::DocumentObjectGroupPython] Bi_element002  label="Bi_element : 1"  # scripted group (container) (typed FeaturePython)
  n = 1
  ref = Bi_element
FEATURE [App::DocumentObjectGroupPython] G4_Bi  # scripted group (container) (typed FeaturePython)
  Dunit = g/cm3
  Dvalue = 9.747
  Group = -> [Bi_element002]
  conduct = 2
  density = 1
  expand = 3
  formula = Bi
  name = G4_Bi
  specific = 4
FEATURE [App::DocumentObjectGroupPython] Po_element001  label="Po_element : 1"  # scripted group (container) (typed FeaturePython)
  n = 1
  ref = Po_element
FEATURE [App::DocumentObjectGroupPython] G4_Po  # scripted group (container) (typed FeaturePython)
  Dunit = g/cm3
  Dvalue = 9.32
  Group = -> [Po_element001]
  conduct = 2
  density = 1
  expand = 3
  formula = Po
  name = G4_Po
  specific = 4
FEATURE [App::DocumentObjectGroupPython] At_element001  label="At_element : 1"  # scripted group (container) (typed FeaturePython)
  n = 1
  ref = At_element
FEATURE [App::DocumentObjectGroupPython] G4_At  # scripted group (container) (typed FeaturePython)
  Dunit = g/cm3
  Dvalue = 9.32
  Group = -> [At_element001]
  conduct = 2
  density = 1
  expand = 3
  formula = At
  name = G4_At
  specific = 4
FEATURE [App::DocumentObjectGroupPython] Rn_element001  label="Rn_element : 1"  # scripted group (container) (typed FeaturePython)
  n = 1
  ref = Rn_element
FEATURE [App::DocumentObjectGroupPython] G4_Rn  # scripted group (container) (typed FeaturePython)
  Dunit = g/cm3
  Dvalue = 0.00900662
  Group = -> [Rn_element001]
  conduct = 2
  density = 1
  expand = 3
  formula = Rn
  name = G4_Rn
  specific = 4
FEATURE [App::DocumentObjectGroupPython] Fr_element001  label="Fr_element : 1"  # scripted group (container) (typed FeaturePython)
  n = 1
  ref = Fr_element
FEATURE [App::DocumentObjectGroupPython] G4_Fr  # scripted group (container) (typed FeaturePython)
  Dunit = g/cm3
  Dvalue = 1
  Group = -> [Fr_element001]
  conduct = 2
  density = 1
  expand = 3
  formula = Fr
  name = G4_Fr
  specific = 4
FEATURE [App::DocumentObjectGroupPython] Ra_element001  label="Ra_element : 1"  # scripted group (container) (typed FeaturePython)
  n = 1
  ref = Ra_element
FEATURE [App::DocumentObjectGroupPython] G4_Ra  # scripted group (container) (typed FeaturePython)
  Dunit = g/cm3
  Dvalue = 5
  Group = -> [Ra_element001]
  conduct = 2
  density = 1
  expand = 3
  formula = Ra
  name = G4_Ra
  specific = 4
FEATURE [App::DocumentObjectGroupPython] Ac_element001  label="Ac_element : 1"  # scripted group (container) (typed FeaturePython)
  n = 1
  ref = Ac_element
FEATURE [App::DocumentObjectGroupPython] G4_Ac  # scripted group (container) (typed FeaturePython)
  Dunit = g/cm3
  Dvalue = 10.07
  Group = -> [Ac_element001]
  conduct = 2
  density = 1
  expand = 3
  formula = Ac
  name = G4_Ac
  specific = 4
FEATURE [App::DocumentObjectGroupPython] Th_element001  label="Th_element : 1"  # scripted group (container) (typed FeaturePython)
  n = 1
  ref = Th_element
FEATURE [App::DocumentObjectGroupPython] G4_Th  # scripted group (container) (typed FeaturePython)
  Dunit = g/cm3
  Dvalue = 11.72
  Group = -> [Th_element001]
  conduct = 2
  density = 1
  expand = 3
  formula = Th
  name = G4_Th
  specific = 4
FEATURE [App::DocumentObjectGroupPython] Pa_element001  label="Pa_element : 1"  # scripted group (container) (typed FeaturePython)
  n = 1
  ref = Pa_element
FEATURE [App::DocumentObjectGroupPython] G4_Pa  # scripted group (container) (typed FeaturePython)
  Dunit = g/cm3
  Dvalue = 15.37
  Group = -> [Pa_element001]
  conduct = 2
  density = 1
  expand = 3
  formula = Pa
  name = G4_Pa
  specific = 4
FEATURE [App::DocumentObjectGroupPython] U_element004  label="U_element : 004"  # scripted group (container) (typed FeaturePython)
  n = 1
  ref = U_element
FEATURE [App::DocumentObjectGroupPython] G4_U  # scripted group (container) (typed FeaturePython)
  Dunit = g/cm3
  Dvalue = 18.95
  Group = -> [U_element004]
  conduct = 2
  density = 1
  expand = 3
  formula = U
  name = G4_U
  specific = 4
FEATURE [App::DocumentObjectGroupPython] Np_element001  label="Np_element : 1"  # scripted group (container) (typed FeaturePython)
  n = 1
  ref = Np_element
FEATURE [App::DocumentObjectGroupPython] G4_Np  # scripted group (container) (typed FeaturePython)
  Dunit = g/cm3
  Dvalue = 20.25
  Group = -> [Np_element001]
  conduct = 2
  density = 1
  expand = 3
  formula = Np
  name = G4_Np
  specific = 4
FEATURE [App::DocumentObjectGroupPython] Pu_element002  label="Pu_element : 002"  # scripted group (container) (typed FeaturePython)
  n = 1
  ref = Pu_element
FEATURE [App::DocumentObjectGroupPython] G4_Pu  # scripted group (container) (typed FeaturePython)
  Dunit = g/cm3
  Dvalue = 19.84
  Group = -> [Pu_element002]
  conduct = 2
  density = 1
  expand = 3
  formula = Pu
  name = G4_Pu
  specific = 4
FEATURE [App::DocumentObjectGroupPython] Am_element001  label="Am_element : 1"  # scripted group (container) (typed FeaturePython)
  n = 1
  ref = Am_element
FEATURE [App::DocumentObjectGroupPython] G4_Am  # scripted group (container) (typed FeaturePython)
  Dunit = g/cm3
  Dvalue = 13.67
  Group = -> [Am_element001]
  conduct = 2
  density = 1
  expand = 3
  formula = Am
  name = G4_Am
  specific = 4
FEATURE [App::DocumentObjectGroupPython] Cm_element001  label="Cm_element : 1"  # scripted group (container) (typed FeaturePython)
  n = 1
  ref = Cm_element
FEATURE [App::DocumentObjectGroupPython] G4_Cm  # scripted group (container) (typed FeaturePython)
  Dunit = g/cm3
  Dvalue = 13.51
  Group = -> [Cm_element001]
  conduct = 2
  density = 1
  expand = 3
  formula = Cm
  name = G4_Cm
  specific = 4
FEATURE [App::DocumentObjectGroupPython] Bk_element001  label="Bk_element : 1"  # scripted group (container) (typed FeaturePython)
  n = 1
  ref = Bk_element
FEATURE [App::DocumentObjectGroupPython] G4_Bk  # scripted group (container) (typed FeaturePython)
  Dunit = g/cm3
  Dvalue = 14
  Group = -> [Bk_element001]
  conduct = 2
  density = 1
  expand = 3
  formula = Bk
  name = G4_Bk
  specific = 4
FEATURE [App::DocumentObjectGroupPython] Cf_element001  label="Cf_element : 1"  # scripted group (container) (typed FeaturePython)
  n = 1
  ref = Cf_element
FEATURE [App::DocumentObjectGroupPython] G4_Cf  # scripted group (container) (typed FeaturePython)
  Dunit = g/cm3
  Dvalue = 10
  Group = -> [Cf_element001]
  conduct = 2
  density = 1
  expand = 3
  formula = Cf
  name = G4_Cf
  specific = 4
FEATURE [App::DocumentObjectGroupPython] Element  # scripted group (container) (typed FeaturePython)
  Group = -> [G4_H,G4_He,G4_Li,G4_Be,G4_B,G4_C,G4_N,G4_O,G4_F,G4_Ne,G4_Na,G4_Mg,G4_Al,G4_Si,G4_P,G4_S,G4_Cl,G4_Ar,G4_K,G4_Ca,G4_Sc,G4_Ti,G4_V,G4_Cr,G4_Mn,G4_Fe,G4_Co,G4_Ni,G4_Cu,G4_Zn,G4_Ga,G4_Ge,G4_As,G4_Se,G4_Br,G4_Kr,G4_Rb,G4_Sr,G4_Y,G4_Zr,G4_Nb,G4_Mo,G4_Tc,G4_Ru,G4_Rh,G4_Pd,G4_Ag,G4_Cd,G4_In,G4_Sn,G4_Sb,G4_Te,G4_I,G4_Xe,G4_Cs,G4_Ba,G4_La,G4_Ce,G4_Pr,G4_Nd,G4_Pm,G4_Sm,G4_Eu,G4_Gd,G4_Tb,G4_Dy,G4_Ho,G4_Er,+30 more]
FEATURE [App::DocumentObjectGroupPython] H_element114  label="H_element : 063"  # scripted group (container) (typed FeaturePython)
  n = 2
  ref = H_element
FEATURE [App::DocumentObjectGroupPython] G4_lH2  # scripted group (container) (typed FeaturePython)
  Dunit = g/cm3
  Dvalue = 0.0708
  Group = -> [H_element114]
  conduct = 2
  density = 1
  expand = 3
  formula = G4_lH2
  name = G4_lH2
  specific = 4
FEATURE [App::DocumentObjectGroupPython] N_element049  label="N_element : 022"  # scripted group (container) (typed FeaturePython)
  n = 2
  ref = N_element
FEATURE [App::DocumentObjectGroupPython] G4_lN2  # scripted group (container) (typed FeaturePython)
  Dunit = g/cm3
  Dvalue = 0.807
  Group = -> [N_element049]
  conduct = 2
  density = 1
  expand = 3
  formula = G4_lN2
  name = G4_lN2
  specific = 4
FEATURE [App::DocumentObjectGroupPython] O_element106  label="O_element : 060"  # scripted group (container) (typed FeaturePython)
  n = 2
  ref = O_element
FEATURE [App::DocumentObjectGroupPython] G4_lO2  # scripted group (container) (typed FeaturePython)
  Dunit = g/cm3
  Dvalue = 1.141
  Group = -> [O_element106]
  conduct = 2
  density = 1
  expand = 3
  formula = G4_lO2
  name = G4_lO2
  specific = 4
FEATURE [App::DocumentObjectGroupPython] Ar_element003  label="Ar_element : 002"  # scripted group (container) (typed FeaturePython)
  n = 1
  ref = Ar_element
FEATURE [App::DocumentObjectGroupPython] G4_lAr  # scripted group (container) (typed FeaturePython)
  Dunit = g/cm3
  Dvalue = 1.396
  Group = -> [Ar_element003]
  conduct = 2
  density = 1
  expand = 3
  formula = G4_lAr
  name = G4_lAr
  specific = 4
FEATURE [App::DocumentObjectGroupPython] Br_element008  label="Br_element : 005"  # scripted group (container) (typed FeaturePython)
  n = 1
  ref = Br_element
FEATURE [App::DocumentObjectGroupPython] G4_lBr  # scripted group (container) (typed FeaturePython)
  Dunit = g/cm3
  Dvalue = 3.1028
  Group = -> [Br_element008]
  conduct = 2
  density = 1
  expand = 3
  formula = G4_lBr
  name = G4_lBr
  specific = 4
FEATURE [App::DocumentObjectGroupPython] Kr_element002  label="Kr_element : 002"  # scripted group (container) (typed FeaturePython)
  n = 1
  ref = Kr_element
FEATURE [App::DocumentObjectGroupPython] G4_lKr  # scripted group (container) (typed FeaturePython)
  Dunit = g/cm3
  Dvalue = 2.418
  Group = -> [Kr_element002]
  conduct = 2
  density = 1
  expand = 3
  formula = G4_lKr
  name = G4_lKr
  specific = 4
FEATURE [App::DocumentObjectGroupPython] Xe_element002  label="Xe_element : 002"  # scripted group (container) (typed FeaturePython)
  n = 1
  ref = Xe_element
FEATURE [App::DocumentObjectGroupPython] G4_lXe  # scripted group (container) (typed FeaturePython)
  Dunit = g/cm3
  Dvalue = 2.953
  Group = -> [Xe_element002]
  conduct = 2
  density = 1
  expand = 3
  formula = G4_lXe
  name = G4_lXe
  specific = 4
FEATURE [App::DocumentObjectGroupPython] O_element107  label="O_element : 061"  # scripted group (container) (typed FeaturePython)
  n = 4
  ref = O_element
FEATURE [App::DocumentObjectGroupPython] Pb_element004  label="Pb_element : 002"  # scripted group (container) (typed FeaturePython)
  n = 1
  ref = Pb_element
FEATURE [App::DocumentObjectGroupPython] W_element005  label="W_element : 005"  # scripted group (container) (typed FeaturePython)
  n = 1
  ref = W_element
FEATURE [App::DocumentObjectGroupPython] G4_PbWO4  # scripted group (container) (typed FeaturePython)
  Dunit = g/cm3
  Dvalue = 8.28
  Group = -> [O_element107,Pb_element004,W_element005]
  conduct = 2
  density = 1
  expand = 3
  formula = G4_PbWO4
  name = G4_PbWO4
  specific = 4
FEATURE [App::DocumentObjectGroupPython] H_element115  label="H_element : 064"  # scripted group (container) (typed FeaturePython)
  n = 1
  ref = H_element
FEATURE [App::DocumentObjectGroupPython] G4_Galactic  # scripted group (container) (typed FeaturePython)
  Dunit = g/cm3
  Dvalue = 0
  Group = -> [H_element115]
  conduct = 2
  density = 1
  expand = 3
  formula = G4_Galactic
  name = G4_Galactic
  specific = 4
FEATURE [App::DocumentObjectGroupPython] C_element125  label="C_element : 071"  # scripted group (container) (typed FeaturePython)
  n = 1
  ref = C_element
FEATURE [App::DocumentObjectGroupPython] G4_GRAPHITE_POROUS  # scripted group (container) (typed FeaturePython)
  Dunit = g/cm3
  Dvalue = 1.7
  Group = -> [C_element125]
  conduct = 2
  density = 1
  expand = 3
  formula = G4_GRAPHITE_POROUS
  name = G4_GRAPHITE_POROUS
  specific = 4
FEATURE [App::DocumentObjectGroupPython] H_element116  label="H_element : 0.150"  # scripted group (container) (typed FeaturePython)
  n = 0.080538
FEATURE [App::DocumentObjectGroupPython] C_element126  label="C_element : 0.600"  # scripted group (container) (typed FeaturePython)
  n = 0.599848
FEATURE [App::DocumentObjectGroupPython] O_element108  label="O_element : 0.320"  # scripted group (container) (typed FeaturePython)
  n = 0.319614
FEATURE [App::DocumentObjectGroupPython] G4_LUCITE  # scripted group (container) (typed FeaturePython)
  Dunit = g/cm3
  Dvalue = 1.19
  Group = -> [H_element116,C_element126,O_element108]
  conduct = 2
  density = 1
  expand = 3
  formula = G4_LUCITE
  name = G4_LUCITE
  specific = 4
FEATURE [App::DocumentObjectGroupPython] Cu_element002  label="Cu_element : 62"  # scripted group (container) (typed FeaturePython)
  n = 62
  ref = Cu_element
FEATURE [App::DocumentObjectGroupPython] Zn_element002  label="Zn_element : 35"  # scripted group (container) (typed FeaturePython)
  n = 35
  ref = Zn_element
FEATURE [App::DocumentObjectGroupPython] Pb_element005  label="Pb_element : 3"  # scripted group (container) (typed FeaturePython)
  n = 3
  ref = Pb_element
FEATURE [App::DocumentObjectGroupPython] G4_BRASS  # scripted group (container) (typed FeaturePython)
  Dunit = g/cm3
  Dvalue = 8.52
  Group = -> [Cu_element002,Zn_element002,Pb_element005]
  conduct = 2
  density = 1
  expand = 3
  formula = G4_BRASS
  name = G4_BRASS
  specific = 4
FEATURE [App::DocumentObjectGroupPython] Cu_element003  label="Cu_element : 89"  # scripted group (container) (typed FeaturePython)
  n = 89
  ref = Cu_element
FEATURE [App::DocumentObjectGroupPython] Zn_element003  label="Zn_element : 9"  # scripted group (container) (typed FeaturePython)
  n = 9
  ref = Zn_element
FEATURE [App::DocumentObjectGroupPython] Pb_element006  label="Pb_element : 2"  # scripted group (container) (typed FeaturePython)
  n = 2
  ref = Pb_element
FEATURE [App::DocumentObjectGroupPython] G4_BRONZE  # scripted group (container) (typed FeaturePython)
  Dunit = g/cm3
  Dvalue = 8.82
  Group = -> [Cu_element003,Zn_element003,Pb_element006]
  conduct = 2
  density = 1
  expand = 3
  formula = G4_BRONZE
  name = G4_BRONZE
  specific = 4
FEATURE [App::DocumentObjectGroupPython] Fe_element008  label="Fe_element : 74"  # scripted group (container) (typed FeaturePython)
  n = 74
  ref = Fe_element
FEATURE [App::DocumentObjectGroupPython] Cr_element002  label="Cr_element : 18"  # scripted group (container) (typed FeaturePython)
  n = 18
  ref = Cr_element
FEATURE [App::DocumentObjectGroupPython] Ni_element002  label="Ni_element : 8"  # scripted group (container) (typed FeaturePython)
  n = 8
  ref = Ni_element
FEATURE [App::DocumentObjectGroupPython] G4_STAINLESS_STEEL  label="G4_STAINLESS-STEEL"  # scripted group (container) (typed FeaturePython)
  Dunit = g/cm3
  Dvalue = 8
  Group = -> [Fe_element008,Cr_element002,Ni_element002]
  conduct = 2
  density = 1
  expand = 3
  formula = G4_STAINLESS-STEEL
  name = G4_STAINLESS-STEEL
  specific = 4
FEATURE [App::DocumentObjectGroupPython] H_element117  label="H_element : 065"  # scripted group (container) (typed FeaturePython)
  n = 18
  ref = H_element
FEATURE [App::DocumentObjectGroupPython] C_element127  label="C_element : 072"  # scripted group (container) (typed FeaturePython)
  n = 12
  ref = C_element
FEATURE [App::DocumentObjectGroupPython] O_element109  label="O_element : 062"  # scripted group (container) (typed FeaturePython)
  n = 7
  ref = O_element
FEATURE [App::DocumentObjectGroupPython] G4_CR39  # scripted group (container) (typed FeaturePython)
  Dunit = g/cm3
  Dvalue = 1.32
  Group = -> [H_element117,C_element127,O_element109]
  conduct = 2
  density = 1
  expand = 3
  formula = G4_CR39
  name = G4_CR39
  specific = 4
FEATURE [App::DocumentObjectGroupPython] H_element118  label="H_element : 38"  # scripted group (container) (typed FeaturePython)
  n = 38
  ref = H_element
FEATURE [App::DocumentObjectGroupPython] C_element128  label="C_element : 073"  # scripted group (container) (typed FeaturePython)
  n = 18
  ref = C_element
FEATURE [App::DocumentObjectGroupPython] O_element110  label="O_element : 063"  # scripted group (container) (typed FeaturePython)
  n = 1
  ref = O_element
FEATURE [App::DocumentObjectGroupPython] G4_OCTADECANOL  # scripted group (container) (typed FeaturePython)
  Dunit = g/cm3
  Dvalue = 0.812
  Group = -> [H_element118,C_element128,O_element110]
  conduct = 2
  density = 1
  expand = 3
  formula = G4_OCTADECANOL
  name = G4_OCTADECANOL
  specific = 4
FEATURE [App::DocumentObjectGroupPython] HEP  # scripted group (container) (typed FeaturePython)
  Group = -> [G4_lH2,G4_lN2,G4_lO2,G4_lAr,G4_lBr,G4_lKr,G4_lXe,G4_PbWO4,G4_Galactic,G4_GRAPHITE_POROUS,G4_LUCITE,G4_BRASS,G4_BRONZE,G4_STAINLESS_STEEL,G4_CR39,G4_OCTADECANOL]
FEATURE [App::DocumentObjectGroupPython] C_element129  label="C_element : 074"  # scripted group (container) (typed FeaturePython)
  n = 14
  ref = C_element
FEATURE [App::DocumentObjectGroupPython] H_element119  label="H_element : 066"  # scripted group (container) (typed FeaturePython)
  n = 10
  ref = H_element
FEATURE [App::DocumentObjectGroupPython] O_element111  label="O_element : 064"  # scripted group (container) (typed FeaturePython)
  n = 2
  ref = O_element
FEATURE [App::DocumentObjectGroupPython] N_element050  label="N_element : 023"  # scripted group (container) (typed FeaturePython)
  n = 2
  ref = N_element
FEATURE [App::DocumentObjectGroupPython] G4_KEVLAR  # scripted group (container) (typed FeaturePython)
  Dunit = g/cm3
  Dvalue = 1.44
  Group = -> [C_element129,H_element119,O_element111,N_element050]
  conduct = 2
  density = 1
  expand = 3
  formula = G4_KEVLAR
  name = G4_KEVLAR
  specific = 4
FEATURE [App::DocumentObjectGroupPython] C_element130  label="C_element : 075"  # scripted group (container) (typed FeaturePython)
  n = 10
  ref = C_element
FEATURE [App::DocumentObjectGroupPython] H_element120  label="H_element : 067"  # scripted group (container) (typed FeaturePython)
  n = 8
  ref = H_element
FEATURE [App::DocumentObjectGroupPython] O_element112  label="O_element : 065"  # scripted group (container) (typed FeaturePython)
  n = 4
  ref = O_element
FEATURE [App::DocumentObjectGroupPython] G4_DACRON  # scripted group (container) (typed FeaturePython)
  Dunit = g/cm3
  Dvalue = 1.4
  Group = -> [C_element130,H_element120,O_element112]
  conduct = 2
  density = 1
  expand = 3
  formula = G4_DACRON
  name = G4_DACRON
  specific = 4
FEATURE [App::DocumentObjectGroupPython] C_element131  label="C_element : 076"  # scripted group (container) (typed FeaturePython)
  n = 4
  ref = C_element
FEATURE [App::DocumentObjectGroupPython] H_element121  label="H_element : 068"  # scripted group (container) (typed FeaturePython)
  n = 5
  ref = H_element
FEATURE [App::DocumentObjectGroupPython] Cl_element030  label="Cl_element : 016"  # scripted group (container) (typed FeaturePython)
  n = 1
  ref = Cl_element
FEATURE [App::DocumentObjectGroupPython] G4_NEOPRENE  # scripted group (container) (typed FeaturePython)
  Dunit = g/cm3
  Dvalue = 1.23
  Group = -> [C_element131,H_element121,Cl_element030]
  conduct = 2
  density = 1
  expand = 3
  formula = G4_NEOPRENE
  name = G4_NEOPRENE
  specific = 4
FEATURE [App::DocumentObjectGroupPython] Space  # scripted group (container) (typed FeaturePython)
  Group = -> [G4_KEVLAR,G4_DACRON,G4_NEOPRENE]
FEATURE [App::DocumentObjectGroupPython] H_element122  label="H_element : 069"  # scripted group (container) (typed FeaturePython)
  n = 5
  ref = H_element
FEATURE [App::DocumentObjectGroupPython] C_element132  label="C_element : 077"  # scripted group (container) (typed FeaturePython)
  n = 4
  ref = C_element
FEATURE [App::DocumentObjectGroupPython] N_element051  label="N_element : 3"  # scripted group (container) (typed FeaturePython)
  n = 3
  ref = N_element
FEATURE [App::DocumentObjectGroupPython] O_element113  label="O_element : 066"  # scripted group (container) (typed FeaturePython)
  n = 1
  ref = O_element
FEATURE [App::DocumentObjectGroupPython] G4_CYTOSINE  # scripted group (container) (typed FeaturePython)
  Dunit = g/cm3
  Dvalue = 1.55
  Group = -> [H_element122,C_element132,N_element051,O_element113]
  conduct = 2
  density = 1
  expand = 3
  formula = G4_CYTOSINE
  name = G4_CYTOSINE
  specific = 4
FEATURE [App::DocumentObjectGroupPython] H_element123  label="H_element : 070"  # scripted group (container) (typed FeaturePython)
  n = 6
  ref = H_element
FEATURE [App::DocumentObjectGroupPython] C_element133  label="C_element : 078"  # scripted group (container) (typed FeaturePython)
  n = 5
  ref = C_element
FEATURE [App::DocumentObjectGroupPython] N_element052  label="N_element : 024"  # scripted group (container) (typed FeaturePython)
  n = 2
  ref = N_element
FEATURE [App::DocumentObjectGroupPython] O_element114  label="O_element : 067"  # scripted group (container) (typed FeaturePython)
  n = 2
  ref = O_element
FEATURE [App::DocumentObjectGroupPython] G4_THYMINE  # scripted group (container) (typed FeaturePython)
  Dunit = g/cm3
  Dvalue = 1.23
  Group = -> [H_element123,C_element133,N_element052,O_element114]
  conduct = 2
  density = 1
  expand = 3
  formula = G4_THYMINE
  name = G4_THYMINE
  specific = 4
FEATURE [App::DocumentObjectGroupPython] H_element124  label="H_element : 071"  # scripted group (container) (typed FeaturePython)
  n = 4
  ref = H_element
FEATURE [App::DocumentObjectGroupPython] C_element134  label="C_element : 079"  # scripted group (container) (typed FeaturePython)
  n = 4
  ref = C_element
FEATURE [App::DocumentObjectGroupPython] N_element053  label="N_element : 025"  # scripted group (container) (typed FeaturePython)
  n = 2
  ref = N_element
FEATURE [App::DocumentObjectGroupPython] O_element115  label="O_element : 068"  # scripted group (container) (typed FeaturePython)
  n = 2
  ref = O_element
FEATURE [App::DocumentObjectGroupPython] G4_URACIL  # scripted group (container) (typed FeaturePython)
  Dunit = g/cm3
  Dvalue = 1.32
  Group = -> [H_element124,C_element134,N_element053,O_element115]
  conduct = 2
  density = 1
  expand = 3
  formula = G4_URACIL
  name = G4_URACIL
  specific = 4
FEATURE [App::DocumentObjectGroupPython] H_element125  label="H_element : 072"  # scripted group (container) (typed FeaturePython)
  n = 4
  ref = H_element
FEATURE [App::DocumentObjectGroupPython] C_element135  label="C_element : 080"  # scripted group (container) (typed FeaturePython)
  n = 5
  ref = C_element
FEATURE [App::DocumentObjectGroupPython] N_element054  label="N_element : 026"  # scripted group (container) (typed FeaturePython)
  n = 5
  ref = N_element
FEATURE [App::DocumentObjectGroupPython] G4_DNA_ADENINE  # scripted group (container) (typed FeaturePython)
  Dunit = g/cm3
  Dvalue = 1
  Group = -> [H_element125,C_element135,N_element054]
  conduct = 2
  density = 1
  expand = 3
  formula = G4_DNA_ADENINE
  name = G4_DNA_ADENINE
  specific = 4
FEATURE [App::DocumentObjectGroupPython] H_element126  label="H_element : 073"  # scripted group (container) (typed FeaturePython)
  n = 4
  ref = H_element
FEATURE [App::DocumentObjectGroupPython] C_element136  label="C_element : 081"  # scripted group (container) (typed FeaturePython)
  n = 5
  ref = C_element
FEATURE [App::DocumentObjectGroupPython] N_element055  label="N_element : 027"  # scripted group (container) (typed FeaturePython)
  n = 5
  ref = N_element
FEATURE [App::DocumentObjectGroupPython] O_element116  label="O_element : 069"  # scripted group (container) (typed FeaturePython)
  n = 1
  ref = O_element
FEATURE [App::DocumentObjectGroupPython] G4_DNA_GUANINE  # scripted group (container) (typed FeaturePython)
  Dunit = g/cm3
  Dvalue = 1
  Group = -> [H_element126,C_element136,N_element055,O_element116]
  conduct = 2
  density = 1
  expand = 3
  formula = G4_DNA_GUANINE
  name = G4_DNA_GUANINE
  specific = 4
FEATURE [App::DocumentObjectGroupPython] H_element127  label="H_element : 074"  # scripted group (container) (typed FeaturePython)
  n = 4
  ref = H_element
FEATURE [App::DocumentObjectGroupPython] C_element137  label="C_element : 082"  # scripted group (container) (typed FeaturePython)
  n = 4
  ref = C_element
FEATURE [App::DocumentObjectGroupPython] N_element056  label="N_element : 028"  # scripted group (container) (typed FeaturePython)
  n = 3
  ref = N_element
FEATURE [App::DocumentObjectGroupPython] O_element117  label="O_element : 070"  # scripted group (container) (typed FeaturePython)
  n = 1
  ref = O_element
FEATURE [App::DocumentObjectGroupPython] G4_DNA_CYTOSINE  # scripted group (container) (typed FeaturePython)
  Dunit = g/cm3
  Dvalue = 1
  Group = -> [H_element127,C_element137,N_element056,O_element117]
  conduct = 2
  density = 1
  expand = 3
  formula = G4_DNA_CYTOSINE
  name = G4_DNA_CYTOSINE
  specific = 4
FEATURE [App::DocumentObjectGroupPython] H_element128  label="H_element : 075"  # scripted group (container) (typed FeaturePython)
  n = 5
  ref = H_element
FEATURE [App::DocumentObjectGroupPython] C_element138  label="C_element : 083"  # scripted group (container) (typed FeaturePython)
  n = 5
  ref = C_element
FEATURE [App::DocumentObjectGroupPython] N_element057  label="N_element : 029"  # scripted group (container) (typed FeaturePython)
  n = 2
  ref = N_element
FEATURE [App::DocumentObjectGroupPython] O_element118  label="O_element : 071"  # scripted group (container) (typed FeaturePython)
  n = 2
  ref = O_element
FEATURE [App::DocumentObjectGroupPython] G4_DNA_THYMINE  # scripted group (container) (typed FeaturePython)
  Dunit = g/cm3
  Dvalue = 1
  Group = -> [H_element128,C_element138,N_element057,O_element118]
  conduct = 2
  density = 1
  expand = 3
  formula = G4_DNA_THYMINE
  name = G4_DNA_THYMINE
  specific = 4
FEATURE [App::DocumentObjectGroupPython] H_element129  label="H_element : 076"  # scripted group (container) (typed FeaturePython)
  n = 3
  ref = H_element
FEATURE [App::DocumentObjectGroupPython] C_element139  label="C_element : 084"  # scripted group (container) (typed FeaturePython)
  n = 4
  ref = C_element
FEATURE [App::DocumentObjectGroupPython] N_element058  label="N_element : 030"  # scripted group (container) (typed FeaturePython)
  n = 2
  ref = N_element
FEATURE [App::DocumentObjectGroupPython] O_element119  label="O_element : 072"  # scripted group (container) (typed FeaturePython)
  n = 2
  ref = O_element
FEATURE [App::DocumentObjectGroupPython] G4_DNA_URACIL  # scripted group (container) (typed FeaturePython)
  Dunit = g/cm3
  Dvalue = 1
  Group = -> [H_element129,C_element139,N_element058,O_element119]
  conduct = 2
  density = 1
  expand = 3
  formula = G4_DNA_URACIL
  name = G4_DNA_URACIL
  specific = 4
FEATURE [App::DocumentObjectGroupPython] H_element130  label="H_element : 077"  # scripted group (container) (typed FeaturePython)
  n = 10
  ref = H_element
FEATURE [App::DocumentObjectGroupPython] C_element140  label="C_element : 085"  # scripted group (container) (typed FeaturePython)
  n = 10
  ref = C_element
FEATURE [App::DocumentObjectGroupPython] N_element059  label="N_element : 031"  # scripted group (container) (typed FeaturePython)
  n = 5
  ref = N_element
FEATURE [App::DocumentObjectGroupPython] O_element120  label="O_element : 073"  # scripted group (container) (typed FeaturePython)
  n = 4
  ref = O_element
FEATURE [App::DocumentObjectGroupPython] G4_DNA_ADENOSINE  # scripted group (container) (typed FeaturePython)
  Dunit = g/cm3
  Dvalue = 1
  Group = -> [H_element130,C_element140,N_element059,O_element120]
  conduct = 2
  density = 1
  expand = 3
  formula = G4_DNA_ADENOSINE
  name = G4_DNA_ADENOSINE
  specific = 4
FEATURE [App::DocumentObjectGroupPython] H_element131  label="H_element : 078"  # scripted group (container) (typed FeaturePython)
  n = 10
  ref = H_element
FEATURE [App::DocumentObjectGroupPython] C_element141  label="C_element : 086"  # scripted group (container) (typed FeaturePython)
  n = 10
  ref = C_element
FEATURE [App::DocumentObjectGroupPython] N_element060  label="N_element : 032"  # scripted group (container) (typed FeaturePython)
  n = 5
  ref = N_element
FEATURE [App::DocumentObjectGroupPython] O_element121  label="O_element : 074"  # scripted group (container) (typed FeaturePython)
  n = 5
  ref = O_element
FEATURE [App::DocumentObjectGroupPython] G4_DNA_GUANOSINE  # scripted group (container) (typed FeaturePython)
  Dunit = g/cm3
  Dvalue = 1
  Group = -> [H_element131,C_element141,N_element060,O_element121]
  conduct = 2
  density = 1
  expand = 3
  formula = G4_DNA_GUANOSINE
  name = G4_DNA_GUANOSINE
  specific = 4
FEATURE [App::DocumentObjectGroupPython] H_element132  label="H_element : 079"  # scripted group (container) (typed FeaturePython)
  n = 10
  ref = H_element
FEATURE [App::DocumentObjectGroupPython] C_element142  label="C_element : 087"  # scripted group (container) (typed FeaturePython)
  n = 9
  ref = C_element
FEATURE [App::DocumentObjectGroupPython] N_element061  label="N_element : 033"  # scripted group (container) (typed FeaturePython)
  n = 3
  ref = N_element
FEATURE [App::DocumentObjectGroupPython] O_element122  label="O_element : 075"  # scripted group (container) (typed FeaturePython)
  n = 5
  ref = O_element
FEATURE [App::DocumentObjectGroupPython] G4_DNA_CYTIDINE  # scripted group (container) (typed FeaturePython)
  Dunit = g/cm3
  Dvalue = 1
  Group = -> [H_element132,C_element142,N_element061,O_element122]
  conduct = 2
  density = 1
  expand = 3
  formula = G4_DNA_CYTIDINE
  name = G4_DNA_CYTIDINE
  specific = 4
FEATURE [App::DocumentObjectGroupPython] H_element133  label="H_element : 080"  # scripted group (container) (typed FeaturePython)
  n = 9
  ref = H_element
FEATURE [App::DocumentObjectGroupPython] C_element143  label="C_element : 088"  # scripted group (container) (typed FeaturePython)
  n = 9
  ref = C_element
FEATURE [App::DocumentObjectGroupPython] N_element062  label="N_element : 034"  # scripted group (container) (typed FeaturePython)
  n = 2
  ref = N_element
FEATURE [App::DocumentObjectGroupPython] O_element123  label="O_element : 076"  # scripted group (container) (typed FeaturePython)
  n = 6
  ref = O_element
FEATURE [App::DocumentObjectGroupPython] G4_DNA_URIDINE  # scripted group (container) (typed FeaturePython)
  Dunit = g/cm3
  Dvalue = 1
  Group = -> [H_element133,C_element143,N_element062,O_element123]
  conduct = 2
  density = 1
  expand = 3
  formula = G4_DNA_URIDINE
  name = G4_DNA_URIDINE
  specific = 4
FEATURE [App::DocumentObjectGroupPython] H_element134  label="H_element : 081"  # scripted group (container) (typed FeaturePython)
  n = 11
  ref = H_element
FEATURE [App::DocumentObjectGroupPython] C_element144  label="C_element : 089"  # scripted group (container) (typed FeaturePython)
  n = 10
  ref = C_element
FEATURE [App::DocumentObjectGroupPython] N_element063  label="N_element : 035"  # scripted group (container) (typed FeaturePython)
  n = 2
  ref = N_element
FEATURE [App::DocumentObjectGroupPython] O_element124  label="O_element : 077"  # scripted group (container) (typed FeaturePython)
  n = 6
  ref = O_element
FEATURE [App::DocumentObjectGroupPython] G4_DNA_METHYLURIDINE  # scripted group (container) (typed FeaturePython)
  Dunit = g/cm3
  Dvalue = 1
  Group = -> [H_element134,C_element144,N_element063,O_element124]
  conduct = 2
  density = 1
  expand = 3
  formula = G4_DNA_METHYLURIDINE
  name = G4_DNA_METHYLURIDINE
  specific = 4
FEATURE [App::DocumentObjectGroupPython] P_element014  label="P_element : 003"  # scripted group (container) (typed FeaturePython)
  n = 1
  ref = P_element
FEATURE [App::DocumentObjectGroupPython] O_element125  label="O_element : 078"  # scripted group (container) (typed FeaturePython)
  n = 3
  ref = O_element
FEATURE [App::DocumentObjectGroupPython] G4_DNA_MONOPHOSPHATE  # scripted group (container) (typed FeaturePython)
  Dunit = g/cm3
  Dvalue = 1
  Group = -> [P_element014,O_element125]
  conduct = 2
  density = 1
  expand = 3
  formula = G4_DNA_MONOPHOSPHATE
  name = G4_DNA_MONOPHOSPHATE
  specific = 4
FEATURE [App::DocumentObjectGroupPython] H_element135  label="H_element : 082"  # scripted group (container) (typed FeaturePython)
  n = 10
  ref = H_element
FEATURE [App::DocumentObjectGroupPython] C_element145  label="C_element : 090"  # scripted group (container) (typed FeaturePython)
  n = 10
  ref = C_element
FEATURE [App::DocumentObjectGroupPython] N_element064  label="N_element : 036"  # scripted group (container) (typed FeaturePython)
  n = 5
  ref = N_element
FEATURE [App::DocumentObjectGroupPython] O_element126  label="O_element : 079"  # scripted group (container) (typed FeaturePython)
  n = 7
  ref = O_element
FEATURE [App::DocumentObjectGroupPython] P_element015  label="P_element : 004"  # scripted group (container) (typed FeaturePython)
  n = 1
  ref = P_element
FEATURE [App::DocumentObjectGroupPython] G4_DNA_A  # scripted group (container) (typed FeaturePython)
  Dunit = g/cm3
  Dvalue = 1
  Group = -> [H_element135,C_element145,N_element064,O_element126,P_element015]
  conduct = 2
  density = 1
  expand = 3
  formula = G4_DNA_A
  name = G4_DNA_A
  specific = 4
FEATURE [App::DocumentObjectGroupPython] H_element136  label="H_element : 083"  # scripted group (container) (typed FeaturePython)
  n = 10
  ref = H_element
FEATURE [App::DocumentObjectGroupPython] C_element146  label="C_element : 091"  # scripted group (container) (typed FeaturePython)
  n = 10
  ref = C_element
FEATURE [App::DocumentObjectGroupPython] N_element065  label="N_element : 037"  # scripted group (container) (typed FeaturePython)
  n = 5
  ref = N_element
FEATURE [App::DocumentObjectGroupPython] O_element127  label="O_element : 8"  # scripted group (container) (typed FeaturePython)
  n = 8
  ref = O_element
FEATURE [App::DocumentObjectGroupPython] P_element016  label="P_element : 005"  # scripted group (container) (typed FeaturePython)
  n = 1
  ref = P_element
FEATURE [App::DocumentObjectGroupPython] G4_DNA_G  # scripted group (container) (typed FeaturePython)
  Dunit = g/cm3
  Dvalue = 1
  Group = -> [H_element136,C_element146,N_element065,O_element127,P_element016]
  conduct = 2
  density = 1
  expand = 3
  formula = G4_DNA_G
  name = G4_DNA_G
  specific = 4
FEATURE [App::DocumentObjectGroupPython] H_element137  label="H_element : 084"  # scripted group (container) (typed FeaturePython)
  n = 10
  ref = H_element
FEATURE [App::DocumentObjectGroupPython] C_element147  label="C_element : 092"  # scripted group (container) (typed FeaturePython)
  n = 9
  ref = C_element
FEATURE [App::DocumentObjectGroupPython] N_element066  label="N_element : 038"  # scripted group (container) (typed FeaturePython)
  n = 3
  ref = N_element
FEATURE [App::DocumentObjectGroupPython] O_element128  label="O_element : 080"  # scripted group (container) (typed FeaturePython)
  n = 8
  ref = O_element
FEATURE [App::DocumentObjectGroupPython] P_element017  label="P_element : 006"  # scripted group (container) (typed FeaturePython)
  n = 1
  ref = P_element
FEATURE [App::DocumentObjectGroupPython] G4_DNA_C  # scripted group (container) (typed FeaturePython)
  Dunit = g/cm3
  Dvalue = 1
  Group = -> [H_element137,C_element147,N_element066,O_element128,P_element017]
  conduct = 2
  density = 1
  expand = 3
  formula = G4_DNA_C
  name = G4_DNA_C
  specific = 4
FEATURE [App::DocumentObjectGroupPython] H_element138  label="H_element : 085"  # scripted group (container) (typed FeaturePython)
  n = 9
  ref = H_element
FEATURE [App::DocumentObjectGroupPython] C_element148  label="C_element : 093"  # scripted group (container) (typed FeaturePython)
  n = 9
  ref = C_element
FEATURE [App::DocumentObjectGroupPython] N_element067  label="N_element : 039"  # scripted group (container) (typed FeaturePython)
  n = 2
  ref = N_element
FEATURE [App::DocumentObjectGroupPython] O_element129  label="O_element : 9"  # scripted group (container) (typed FeaturePython)
  n = 9
  ref = O_element
FEATURE [App::DocumentObjectGroupPython] P_element018  label="P_element : 007"  # scripted group (container) (typed FeaturePython)
  n = 1
  ref = P_element
FEATURE [App::DocumentObjectGroupPython] G4_DNA_U  # scripted group (container) (typed FeaturePython)
  Dunit = g/cm3
  Dvalue = 1
  Group = -> [H_element138,C_element148,N_element067,O_element129,P_element018]
  conduct = 2
  density = 1
  expand = 3
  formula = G4_DNA_U
  name = G4_DNA_U
  specific = 4
FEATURE [App::DocumentObjectGroupPython] H_element139  label="H_element : 086"  # scripted group (container) (typed FeaturePython)
  n = 11
  ref = H_element
FEATURE [App::DocumentObjectGroupPython] C_element149  label="C_element : 094"  # scripted group (container) (typed FeaturePython)
  n = 10
  ref = C_element
FEATURE [App::DocumentObjectGroupPython] N_element068  label="N_element : 040"  # scripted group (container) (typed FeaturePython)
  n = 2
  ref = N_element
FEATURE [App::DocumentObjectGroupPython] O_element130  label="O_element : 081"  # scripted group (container) (typed FeaturePython)
  n = 9
  ref = O_element
FEATURE [App::DocumentObjectGroupPython] P_element019  label="P_element : 008"  # scripted group (container) (typed FeaturePython)
  n = 1
  ref = P_element
FEATURE [App::DocumentObjectGroupPython] G4_DNA_MU  # scripted group (container) (typed FeaturePython)
  Dunit = g/cm3
  Dvalue = 1
  Group = -> [H_element139,C_element149,N_element068,O_element130,P_element019]
  conduct = 2
  density = 1
  expand = 3
  formula = G4_DNA_MU
  name = G4_DNA_MU
  specific = 4
FEATURE [App::DocumentObjectGroupPython] BioChemical  # scripted group (container) (typed FeaturePython)
  Group = -> [G4_CYTOSINE,G4_THYMINE,G4_URACIL,G4_DNA_ADENINE,G4_DNA_GUANINE,G4_DNA_CYTOSINE,G4_DNA_THYMINE,G4_DNA_URACIL,G4_DNA_ADENOSINE,G4_DNA_GUANOSINE,G4_DNA_CYTIDINE,G4_DNA_URIDINE,G4_DNA_METHYLURIDINE,G4_DNA_MONOPHOSPHATE,G4_DNA_A,G4_DNA_G,G4_DNA_C,G4_DNA_U,G4_DNA_MU]
FEATURE [App::DocumentObjectGroupPython] G4Materials  # scripted group (container) (typed FeaturePython)
  Group = -> [NIST,Element,HEP,Space,BioChemical]
  version = 1
FEATURE [App::DocumentObjectGroupPython] Geant4  # scripted group (container) (typed FeaturePython)
  Group = -> [G4Isotopes,G4Elements,G4Materials]
FEATURE [App::DocumentObjectGroupPython] Materials  # scripted group (container) (typed FeaturePython)
  Group = -> [Geant4]
FEATURE [Part::FeaturePython] GDMLBox_WorldBox  # WARN: FeaturePython — macro-defined, semantics opaque (R4)
  lunit = 2
  material = 5
  x = 145.922
  y = 145.922
  z = 130
FEATURE [Part::FeaturePython] GDMLBox_Box  # WARN: FeaturePython — macro-defined, semantics opaque (R4)
  Placement = pos=(0,0,0) rot=(0,0,1;0.261799rad)
  lunit = 2
  material = 0
  x = 10
  y = 10
  z = 10
FEATURE [Part::FeaturePython] Array  # Draft array (typed FeaturePython)
  AlwaysSyncPlacement = false
  Angle = 360
  ArrayType = 0
  Axis = (0,0,1)
  Base = -> GDMLBox_Box
  Center = (0,0,0)
  Count = 4
  ExpandArray = false
  Fuse = false
  IntervalAxis = (0,0,0)
  IntervalX = (50,0,0)
  IntervalY = (0,50,0)
  IntervalZ = (0,0,100)
  NumberCircles = 3
  NumberPolar = 5
  NumberX = 2
  NumberY = 2
  NumberZ = 1
  PlacementList = 4 placements: [(0,0,0),(0,50,0),(50,0,0),(50,50,0)]
  RadialDistance = 50
  ScaleList = (4) [(1,1,1),(1,1,1),(1,1,1),(1,1,1)]
  Symmetry = 1
  TangentialDistance = 25
FEATURE [App::Part] Part
  Group = -> [Array]
  Origin = -> Origin002
FEATURE [App::Part] worldVOL
  Group = -> [GDMLBox_WorldBox,Part]
  Origin = -> Origin
